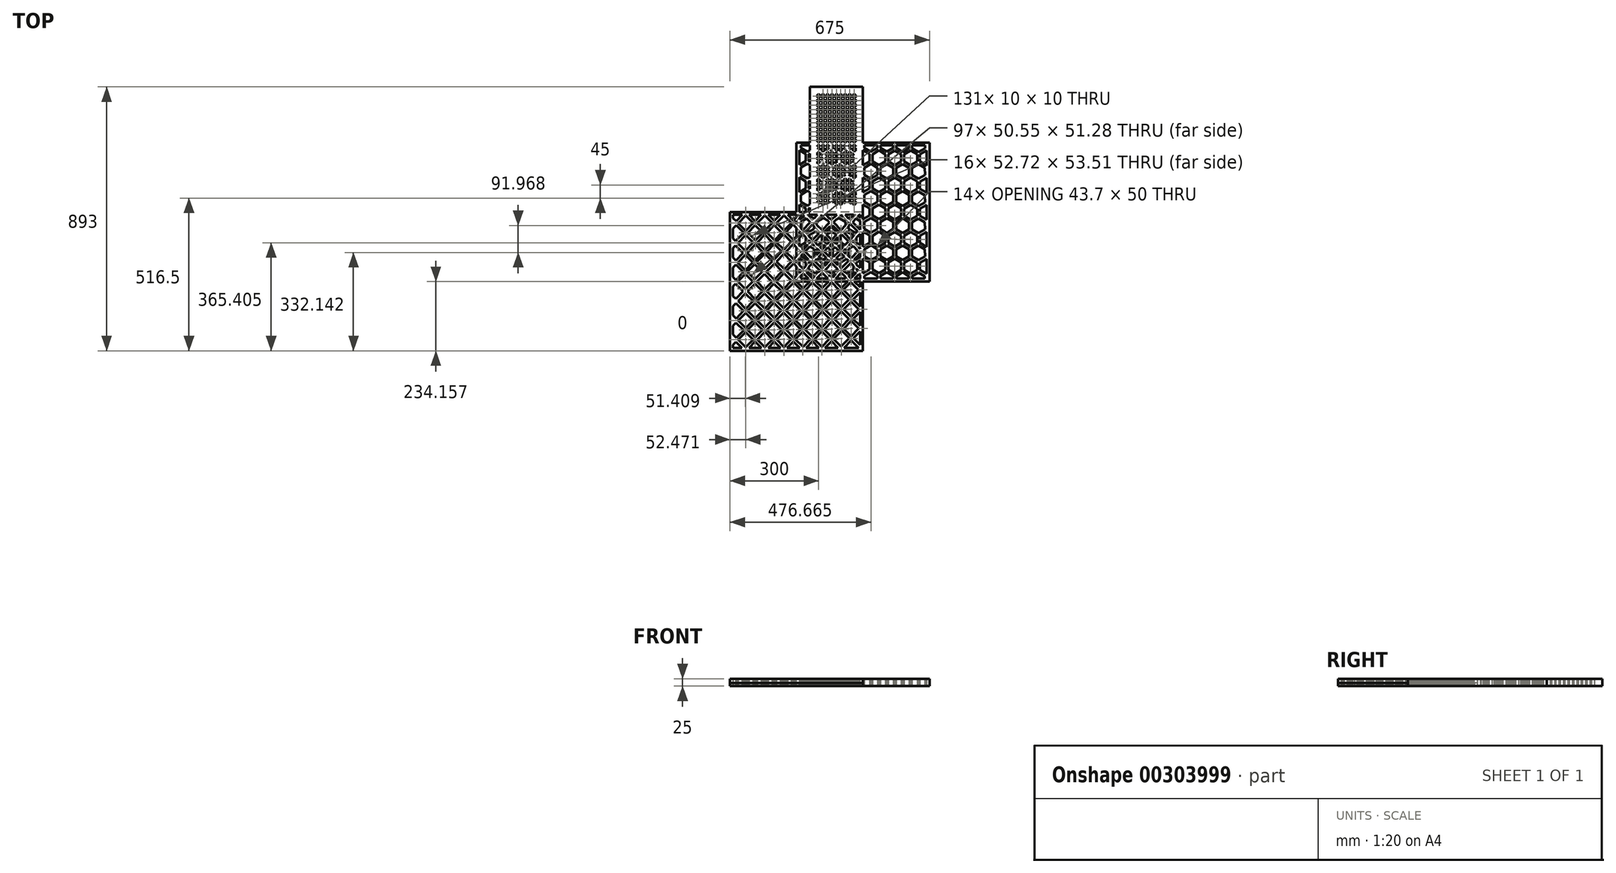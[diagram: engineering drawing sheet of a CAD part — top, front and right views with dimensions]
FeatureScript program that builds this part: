
annotation { "Feature Type Name" : "Feature", "Feature Type Description" : "" }
export const myFeature = defineFeature(function(context is Context, id is Id, definition is map)
    precondition{}
    {
        {
            var Q0;
            Q0=qCreatedBy(makeId("Top.planeOp"),FACE);
            var sketch = newSketch(context, id + "F0", { "sketchPlane" : qUnion([Q0])});
            skLineSegment(sketch, "E0.bottom", {"start": v(-180, 423) * mm, "end": v(0, 423) * mm});
            skLineSegment(sketch, "E0.top", {"start": v(-180, 0) * mm, "end": v(0, 0) * mm});
            skLineSegment(sketch, "E0.left", {"start": v(-180, 423) * mm, "end": v(-180, 0) * mm});
            skLineSegment(sketch, "E0.right", {"start": v(0, 423) * mm, "end": v(0, 0) * mm});
            skLineSegment(sketch, "E1", {"start": v(-153.5, 396.5) * mm, "end": v(-146.5, 396.5) * mm});
            skLineSegment(sketch, "E2", {"start": v(-155, 386.5) * mm, "end": v(-145, 386.5) * mm});
            skLineSegment(sketch, "E3", {"start": v(-145, 386.5) * mm, "end": v(-145, 395) * mm});
            skLineSegment(sketch, "E4.trimOffspring", {"start": v(-155, 386.5) * mm, "end": v(-155, 395) * mm});
            skLineSegment(sketch, "E5.0.1.0", {"start": v(-155, 371.5) * mm, "end": v(-155, 381.5) * mm});
            skLineSegment(sketch, "E5.0.1.1", {"start": v(-145, 371.5) * mm, "end": v(-145, 381.5) * mm});
            skLineSegment(sketch, "E5.0.1.2", {"start": v(-155, 371.5) * mm, "end": v(-145, 371.5) * mm});
            skLineSegment(sketch, "E5.0.1.3", {"start": v(-155, 381.5) * mm, "end": v(-145, 381.5) * mm});
            skLineSegment(sketch, "E5.0.2.0", {"start": v(-155, 356.5) * mm, "end": v(-155, 366.5) * mm});
            skLineSegment(sketch, "E5.0.2.1", {"start": v(-145, 356.5) * mm, "end": v(-145, 366.5) * mm});
            skLineSegment(sketch, "E5.0.2.2", {"start": v(-155, 356.5) * mm, "end": v(-145, 356.5) * mm});
            skLineSegment(sketch, "E5.0.2.3", {"start": v(-155, 366.5) * mm, "end": v(-145, 366.5) * mm});
            skLineSegment(sketch, "E5.0.3.0", {"start": v(-155, 341.5) * mm, "end": v(-155, 351.5) * mm});
            skLineSegment(sketch, "E5.0.3.1", {"start": v(-145, 341.5) * mm, "end": v(-145, 351.5) * mm});
            skLineSegment(sketch, "E5.0.3.2", {"start": v(-155, 341.5) * mm, "end": v(-145, 341.5) * mm});
            skLineSegment(sketch, "E5.0.3.3", {"start": v(-155, 351.5) * mm, "end": v(-145, 351.5) * mm});
            skLineSegment(sketch, "E5.0.4.0", {"start": v(-155, 326.5) * mm, "end": v(-155, 336.5) * mm});
            skLineSegment(sketch, "E5.0.4.1", {"start": v(-145, 326.5) * mm, "end": v(-145, 336.5) * mm});
            skLineSegment(sketch, "E5.0.4.2", {"start": v(-155, 326.5) * mm, "end": v(-145, 326.5) * mm});
            skLineSegment(sketch, "E5.0.4.3", {"start": v(-155, 336.5) * mm, "end": v(-145, 336.5) * mm});
            skLineSegment(sketch, "E5.0.5.0", {"start": v(-155, 311.5) * mm, "end": v(-155, 321.5) * mm});
            skLineSegment(sketch, "E5.0.5.1", {"start": v(-145, 311.5) * mm, "end": v(-145, 321.5) * mm});
            skLineSegment(sketch, "E5.0.5.2", {"start": v(-155, 311.5) * mm, "end": v(-145, 311.5) * mm});
            skLineSegment(sketch, "E5.0.5.3", {"start": v(-155, 321.5) * mm, "end": v(-145, 321.5) * mm});
            skLineSegment(sketch, "E5.0.6.0", {"start": v(-155, 296.5) * mm, "end": v(-155, 306.5) * mm});
            skLineSegment(sketch, "E5.0.6.1", {"start": v(-145, 296.5) * mm, "end": v(-145, 306.5) * mm});
            skLineSegment(sketch, "E5.0.6.2", {"start": v(-155, 296.5) * mm, "end": v(-145, 296.5) * mm});
            skLineSegment(sketch, "E5.0.6.3", {"start": v(-155, 306.5) * mm, "end": v(-145, 306.5) * mm});
            skLineSegment(sketch, "E5.0.7.0", {"start": v(-155, 281.5) * mm, "end": v(-155, 291.5) * mm});
            skLineSegment(sketch, "E5.0.7.1", {"start": v(-145, 281.5) * mm, "end": v(-145, 291.5) * mm});
            skLineSegment(sketch, "E5.0.7.2", {"start": v(-155, 281.5) * mm, "end": v(-145, 281.5) * mm});
            skLineSegment(sketch, "E5.0.7.3", {"start": v(-155, 291.5) * mm, "end": v(-145, 291.5) * mm});
            skLineSegment(sketch, "E5.0.8.0", {"start": v(-155, 266.5) * mm, "end": v(-155, 276.5) * mm});
            skLineSegment(sketch, "E5.0.8.1", {"start": v(-145, 266.5) * mm, "end": v(-145, 276.5) * mm});
            skLineSegment(sketch, "E5.0.8.2", {"start": v(-155, 266.5) * mm, "end": v(-145, 266.5) * mm});
            skLineSegment(sketch, "E5.0.8.3", {"start": v(-155, 276.5) * mm, "end": v(-145, 276.5) * mm});
            skLineSegment(sketch, "E5.0.9.0", {"start": v(-155, 251.5) * mm, "end": v(-155, 261.5) * mm});
            skLineSegment(sketch, "E5.0.9.1", {"start": v(-145, 251.5) * mm, "end": v(-145, 261.5) * mm});
            skLineSegment(sketch, "E5.0.9.2", {"start": v(-155, 251.5) * mm, "end": v(-145, 251.5) * mm});
            skLineSegment(sketch, "E5.0.9.3", {"start": v(-155, 261.5) * mm, "end": v(-145, 261.5) * mm});
            skLineSegment(sketch, "E5.0.10.0", {"start": v(-155, 236.5) * mm, "end": v(-155, 246.5) * mm});
            skLineSegment(sketch, "E5.0.10.1", {"start": v(-145, 236.5) * mm, "end": v(-145, 246.5) * mm});
            skLineSegment(sketch, "E5.0.10.2", {"start": v(-155, 236.5) * mm, "end": v(-145, 236.5) * mm});
            skLineSegment(sketch, "E5.0.10.3", {"start": v(-155, 246.5) * mm, "end": v(-145, 246.5) * mm});
            skLineSegment(sketch, "E5.0.11.0", {"start": v(-155, 221.5) * mm, "end": v(-155, 231.5) * mm});
            skLineSegment(sketch, "E5.0.11.1", {"start": v(-145, 221.5) * mm, "end": v(-145, 231.5) * mm});
            skLineSegment(sketch, "E5.0.11.2", {"start": v(-155, 221.5) * mm, "end": v(-145, 221.5) * mm});
            skLineSegment(sketch, "E5.0.11.3", {"start": v(-155, 231.5) * mm, "end": v(-145, 231.5) * mm});
            skLineSegment(sketch, "E5.0.12.0", {"start": v(-155, 206.5) * mm, "end": v(-155, 216.5) * mm});
            skLineSegment(sketch, "E5.0.12.1", {"start": v(-145, 206.5) * mm, "end": v(-145, 216.5) * mm});
            skLineSegment(sketch, "E5.0.12.2", {"start": v(-155, 206.5) * mm, "end": v(-145, 206.5) * mm});
            skLineSegment(sketch, "E5.0.12.3", {"start": v(-155, 216.5) * mm, "end": v(-145, 216.5) * mm});
            skLineSegment(sketch, "E5.0.13.0", {"start": v(-155, 191.5) * mm, "end": v(-155, 201.5) * mm});
            skLineSegment(sketch, "E5.0.13.1", {"start": v(-145, 191.5) * mm, "end": v(-145, 201.5) * mm});
            skLineSegment(sketch, "E5.0.13.2", {"start": v(-155, 191.5) * mm, "end": v(-145, 191.5) * mm});
            skLineSegment(sketch, "E5.0.13.3", {"start": v(-155, 201.5) * mm, "end": v(-145, 201.5) * mm});
            skLineSegment(sketch, "E5.0.14.0", {"start": v(-155, 176.5) * mm, "end": v(-155, 186.5) * mm});
            skLineSegment(sketch, "E5.0.14.1", {"start": v(-145, 176.5) * mm, "end": v(-145, 186.5) * mm});
            skLineSegment(sketch, "E5.0.14.2", {"start": v(-155, 176.5) * mm, "end": v(-145, 176.5) * mm});
            skLineSegment(sketch, "E5.0.14.3", {"start": v(-155, 186.5) * mm, "end": v(-145, 186.5) * mm});
            skLineSegment(sketch, "E5.0.15.0", {"start": v(-155, 161.5) * mm, "end": v(-155, 171.5) * mm});
            skLineSegment(sketch, "E5.0.15.1", {"start": v(-145, 161.5) * mm, "end": v(-145, 171.5) * mm});
            skLineSegment(sketch, "E5.0.15.2", {"start": v(-155, 161.5) * mm, "end": v(-145, 161.5) * mm});
            skLineSegment(sketch, "E5.0.15.3", {"start": v(-155, 171.5) * mm, "end": v(-145, 171.5) * mm});
            skLineSegment(sketch, "E5.0.16.0", {"start": v(-155, 146.5) * mm, "end": v(-155, 156.5) * mm});
            skLineSegment(sketch, "E5.0.16.1", {"start": v(-145, 146.5) * mm, "end": v(-145, 156.5) * mm});
            skLineSegment(sketch, "E5.0.16.2", {"start": v(-155, 146.5) * mm, "end": v(-145, 146.5) * mm});
            skLineSegment(sketch, "E5.0.16.3", {"start": v(-155, 156.5) * mm, "end": v(-145, 156.5) * mm});
            skLineSegment(sketch, "E5.0.17.0", {"start": v(-155, 131.5) * mm, "end": v(-155, 141.5) * mm});
            skLineSegment(sketch, "E5.0.17.1", {"start": v(-145, 131.5) * mm, "end": v(-145, 141.5) * mm});
            skLineSegment(sketch, "E5.0.17.2", {"start": v(-155, 131.5) * mm, "end": v(-145, 131.5) * mm});
            skLineSegment(sketch, "E5.0.17.3", {"start": v(-155, 141.5) * mm, "end": v(-145, 141.5) * mm});
            skLineSegment(sketch, "E5.0.18.0", {"start": v(-155, 116.5) * mm, "end": v(-155, 126.5) * mm});
            skLineSegment(sketch, "E5.0.18.1", {"start": v(-145, 116.5) * mm, "end": v(-145, 126.5) * mm});
            skLineSegment(sketch, "E5.0.18.2", {"start": v(-155, 116.5) * mm, "end": v(-145, 116.5) * mm});
            skLineSegment(sketch, "E5.0.18.3", {"start": v(-155, 126.5) * mm, "end": v(-145, 126.5) * mm});
            skLineSegment(sketch, "E5.0.19.0", {"start": v(-155, 101.5) * mm, "end": v(-155, 111.5) * mm});
            skLineSegment(sketch, "E5.0.19.1", {"start": v(-145, 101.5) * mm, "end": v(-145, 111.5) * mm});
            skLineSegment(sketch, "E5.0.19.2", {"start": v(-155, 101.5) * mm, "end": v(-145, 101.5) * mm});
            skLineSegment(sketch, "E5.0.19.3", {"start": v(-155, 111.5) * mm, "end": v(-145, 111.5) * mm});
            skLineSegment(sketch, "E5.0.20.0", {"start": v(-155, 86.5) * mm, "end": v(-155, 96.5) * mm});
            skLineSegment(sketch, "E5.0.20.1", {"start": v(-145, 86.5) * mm, "end": v(-145, 96.5) * mm});
            skLineSegment(sketch, "E5.0.20.2", {"start": v(-155, 86.5) * mm, "end": v(-145, 86.5) * mm});
            skLineSegment(sketch, "E5.0.20.3", {"start": v(-155, 96.5) * mm, "end": v(-145, 96.5) * mm});
            skLineSegment(sketch, "E5.0.21.0", {"start": v(-155, 71.5) * mm, "end": v(-155, 81.5) * mm});
            skLineSegment(sketch, "E5.0.21.1", {"start": v(-145, 71.5) * mm, "end": v(-145, 81.5) * mm});
            skLineSegment(sketch, "E5.0.21.2", {"start": v(-155, 71.5) * mm, "end": v(-145, 71.5) * mm});
            skLineSegment(sketch, "E5.0.21.3", {"start": v(-155, 81.5) * mm, "end": v(-145, 81.5) * mm});
            skLineSegment(sketch, "E5.0.22.0", {"start": v(-155, 56.5) * mm, "end": v(-155, 66.5) * mm});
            skLineSegment(sketch, "E5.0.22.1", {"start": v(-145, 56.5) * mm, "end": v(-145, 66.5) * mm});
            skLineSegment(sketch, "E5.0.22.2", {"start": v(-155, 56.5) * mm, "end": v(-145, 56.5) * mm});
            skLineSegment(sketch, "E5.0.22.3", {"start": v(-155, 66.5) * mm, "end": v(-145, 66.5) * mm});
            skLineSegment(sketch, "E5.0.23.0", {"start": v(-155, 41.5) * mm, "end": v(-155, 51.5) * mm});
            skLineSegment(sketch, "E5.0.23.1", {"start": v(-145, 41.5) * mm, "end": v(-145, 51.5) * mm});
            skLineSegment(sketch, "E5.0.23.2", {"start": v(-155, 41.5) * mm, "end": v(-145, 41.5) * mm});
            skLineSegment(sketch, "E5.0.23.3", {"start": v(-155, 51.5) * mm, "end": v(-145, 51.5) * mm});
            skLineSegment(sketch, "E5.0.24.0", {"start": v(-155, 26.5) * mm, "end": v(-155, 36.5) * mm});
            skLineSegment(sketch, "E5.0.24.1", {"start": v(-145, 26.5) * mm, "end": v(-145, 36.5) * mm});
            skLineSegment(sketch, "E5.0.24.2", {"start": v(-155, 26.5) * mm, "end": v(-145, 26.5) * mm});
            skLineSegment(sketch, "E5.0.24.3", {"start": v(-155, 36.5) * mm, "end": v(-145, 36.5) * mm});
            skLineSegment(sketch, "E5.1.0.0", {"start": v(-140, 386.5) * mm, "end": v(-140, 396.5) * mm});
            skLineSegment(sketch, "E5.1.0.1", {"start": v(-130, 386.5) * mm, "end": v(-130, 396.5) * mm});
            skLineSegment(sketch, "E5.1.0.2", {"start": v(-140, 386.5) * mm, "end": v(-130, 386.5) * mm});
            skLineSegment(sketch, "E5.1.0.3", {"start": v(-140, 396.5) * mm, "end": v(-130, 396.5) * mm});
            skLineSegment(sketch, "E5.1.1.0", {"start": v(-140, 371.5) * mm, "end": v(-140, 381.5) * mm});
            skLineSegment(sketch, "E5.1.1.1", {"start": v(-130, 371.5) * mm, "end": v(-130, 381.5) * mm});
            skLineSegment(sketch, "E5.1.1.2", {"start": v(-140, 371.5) * mm, "end": v(-130, 371.5) * mm});
            skLineSegment(sketch, "E5.1.1.3", {"start": v(-140, 381.5) * mm, "end": v(-130, 381.5) * mm});
            skLineSegment(sketch, "E5.1.2.0", {"start": v(-140, 356.5) * mm, "end": v(-140, 366.5) * mm});
            skLineSegment(sketch, "E5.1.2.1", {"start": v(-130, 356.5) * mm, "end": v(-130, 366.5) * mm});
            skLineSegment(sketch, "E5.1.2.2", {"start": v(-140, 356.5) * mm, "end": v(-130, 356.5) * mm});
            skLineSegment(sketch, "E5.1.2.3", {"start": v(-140, 366.5) * mm, "end": v(-130, 366.5) * mm});
            skLineSegment(sketch, "E5.1.3.0", {"start": v(-140, 341.5) * mm, "end": v(-140, 351.5) * mm});
            skLineSegment(sketch, "E5.1.3.1", {"start": v(-130, 341.5) * mm, "end": v(-130, 351.5) * mm});
            skLineSegment(sketch, "E5.1.3.2", {"start": v(-140, 341.5) * mm, "end": v(-130, 341.5) * mm});
            skLineSegment(sketch, "E5.1.3.3", {"start": v(-140, 351.5) * mm, "end": v(-130, 351.5) * mm});
            skLineSegment(sketch, "E5.1.4.0", {"start": v(-140, 326.5) * mm, "end": v(-140, 336.5) * mm});
            skLineSegment(sketch, "E5.1.4.1", {"start": v(-130, 326.5) * mm, "end": v(-130, 336.5) * mm});
            skLineSegment(sketch, "E5.1.4.2", {"start": v(-140, 326.5) * mm, "end": v(-130, 326.5) * mm});
            skLineSegment(sketch, "E5.1.4.3", {"start": v(-140, 336.5) * mm, "end": v(-130, 336.5) * mm});
            skLineSegment(sketch, "E5.1.5.0", {"start": v(-140, 311.5) * mm, "end": v(-140, 321.5) * mm});
            skLineSegment(sketch, "E5.1.5.1", {"start": v(-130, 311.5) * mm, "end": v(-130, 321.5) * mm});
            skLineSegment(sketch, "E5.1.5.2", {"start": v(-140, 311.5) * mm, "end": v(-130, 311.5) * mm});
            skLineSegment(sketch, "E5.1.5.3", {"start": v(-140, 321.5) * mm, "end": v(-130, 321.5) * mm});
            skLineSegment(sketch, "E5.1.6.0", {"start": v(-140, 296.5) * mm, "end": v(-140, 306.5) * mm});
            skLineSegment(sketch, "E5.1.6.1", {"start": v(-130, 296.5) * mm, "end": v(-130, 306.5) * mm});
            skLineSegment(sketch, "E5.1.6.2", {"start": v(-140, 296.5) * mm, "end": v(-130, 296.5) * mm});
            skLineSegment(sketch, "E5.1.6.3", {"start": v(-140, 306.5) * mm, "end": v(-130, 306.5) * mm});
            skLineSegment(sketch, "E5.1.7.0", {"start": v(-140, 281.5) * mm, "end": v(-140, 291.5) * mm});
            skLineSegment(sketch, "E5.1.7.1", {"start": v(-130, 281.5) * mm, "end": v(-130, 291.5) * mm});
            skLineSegment(sketch, "E5.1.7.2", {"start": v(-140, 281.5) * mm, "end": v(-130, 281.5) * mm});
            skLineSegment(sketch, "E5.1.7.3", {"start": v(-140, 291.5) * mm, "end": v(-130, 291.5) * mm});
            skLineSegment(sketch, "E5.1.8.0", {"start": v(-140, 266.5) * mm, "end": v(-140, 276.5) * mm});
            skLineSegment(sketch, "E5.1.8.1", {"start": v(-130, 266.5) * mm, "end": v(-130, 276.5) * mm});
            skLineSegment(sketch, "E5.1.8.2", {"start": v(-140, 266.5) * mm, "end": v(-130, 266.5) * mm});
            skLineSegment(sketch, "E5.1.8.3", {"start": v(-140, 276.5) * mm, "end": v(-130, 276.5) * mm});
            skLineSegment(sketch, "E5.1.9.0", {"start": v(-140, 251.5) * mm, "end": v(-140, 261.5) * mm});
            skLineSegment(sketch, "E5.1.9.1", {"start": v(-130, 251.5) * mm, "end": v(-130, 261.5) * mm});
            skLineSegment(sketch, "E5.1.9.2", {"start": v(-140, 251.5) * mm, "end": v(-130, 251.5) * mm});
            skLineSegment(sketch, "E5.1.9.3", {"start": v(-140, 261.5) * mm, "end": v(-130, 261.5) * mm});
            skLineSegment(sketch, "E5.1.10.0", {"start": v(-140, 236.5) * mm, "end": v(-140, 246.5) * mm});
            skLineSegment(sketch, "E5.1.10.1", {"start": v(-130, 236.5) * mm, "end": v(-130, 246.5) * mm});
            skLineSegment(sketch, "E5.1.10.2", {"start": v(-140, 236.5) * mm, "end": v(-130, 236.5) * mm});
            skLineSegment(sketch, "E5.1.10.3", {"start": v(-140, 246.5) * mm, "end": v(-130, 246.5) * mm});
            skLineSegment(sketch, "E5.1.11.0", {"start": v(-140, 221.5) * mm, "end": v(-140, 231.5) * mm});
            skLineSegment(sketch, "E5.1.11.1", {"start": v(-130, 221.5) * mm, "end": v(-130, 231.5) * mm});
            skLineSegment(sketch, "E5.1.11.2", {"start": v(-140, 221.5) * mm, "end": v(-130, 221.5) * mm});
            skLineSegment(sketch, "E5.1.11.3", {"start": v(-140, 231.5) * mm, "end": v(-130, 231.5) * mm});
            skLineSegment(sketch, "E5.1.12.0", {"start": v(-140, 206.5) * mm, "end": v(-140, 216.5) * mm});
            skLineSegment(sketch, "E5.1.12.1", {"start": v(-130, 206.5) * mm, "end": v(-130, 216.5) * mm});
            skLineSegment(sketch, "E5.1.12.2", {"start": v(-140, 206.5) * mm, "end": v(-130, 206.5) * mm});
            skLineSegment(sketch, "E5.1.12.3", {"start": v(-140, 216.5) * mm, "end": v(-130, 216.5) * mm});
            skLineSegment(sketch, "E5.1.13.0", {"start": v(-140, 191.5) * mm, "end": v(-140, 201.5) * mm});
            skLineSegment(sketch, "E5.1.13.1", {"start": v(-130, 191.5) * mm, "end": v(-130, 201.5) * mm});
            skLineSegment(sketch, "E5.1.13.2", {"start": v(-140, 191.5) * mm, "end": v(-130, 191.5) * mm});
            skLineSegment(sketch, "E5.1.13.3", {"start": v(-140, 201.5) * mm, "end": v(-130, 201.5) * mm});
            skLineSegment(sketch, "E5.1.14.0", {"start": v(-140, 176.5) * mm, "end": v(-140, 186.5) * mm});
            skLineSegment(sketch, "E5.1.14.1", {"start": v(-130, 176.5) * mm, "end": v(-130, 186.5) * mm});
            skLineSegment(sketch, "E5.1.14.2", {"start": v(-140, 176.5) * mm, "end": v(-130, 176.5) * mm});
            skLineSegment(sketch, "E5.1.14.3", {"start": v(-140, 186.5) * mm, "end": v(-130, 186.5) * mm});
            skLineSegment(sketch, "E5.1.15.0", {"start": v(-140, 161.5) * mm, "end": v(-140, 171.5) * mm});
            skLineSegment(sketch, "E5.1.15.1", {"start": v(-130, 161.5) * mm, "end": v(-130, 171.5) * mm});
            skLineSegment(sketch, "E5.1.15.2", {"start": v(-140, 161.5) * mm, "end": v(-130, 161.5) * mm});
            skLineSegment(sketch, "E5.1.15.3", {"start": v(-140, 171.5) * mm, "end": v(-130, 171.5) * mm});
            skLineSegment(sketch, "E5.1.16.0", {"start": v(-140, 146.5) * mm, "end": v(-140, 156.5) * mm});
            skLineSegment(sketch, "E5.1.16.1", {"start": v(-130, 146.5) * mm, "end": v(-130, 156.5) * mm});
            skLineSegment(sketch, "E5.1.16.2", {"start": v(-140, 146.5) * mm, "end": v(-130, 146.5) * mm});
            skLineSegment(sketch, "E5.1.16.3", {"start": v(-140, 156.5) * mm, "end": v(-130, 156.5) * mm});
            skLineSegment(sketch, "E5.1.17.0", {"start": v(-140, 131.5) * mm, "end": v(-140, 141.5) * mm});
            skLineSegment(sketch, "E5.1.17.1", {"start": v(-130, 131.5) * mm, "end": v(-130, 141.5) * mm});
            skLineSegment(sketch, "E5.1.17.2", {"start": v(-140, 131.5) * mm, "end": v(-130, 131.5) * mm});
            skLineSegment(sketch, "E5.1.17.3", {"start": v(-140, 141.5) * mm, "end": v(-130, 141.5) * mm});
            skLineSegment(sketch, "E5.1.18.0", {"start": v(-140, 116.5) * mm, "end": v(-140, 126.5) * mm});
            skLineSegment(sketch, "E5.1.18.1", {"start": v(-130, 116.5) * mm, "end": v(-130, 126.5) * mm});
            skLineSegment(sketch, "E5.1.18.2", {"start": v(-140, 116.5) * mm, "end": v(-130, 116.5) * mm});
            skLineSegment(sketch, "E5.1.18.3", {"start": v(-140, 126.5) * mm, "end": v(-130, 126.5) * mm});
            skLineSegment(sketch, "E5.1.19.0", {"start": v(-140, 101.5) * mm, "end": v(-140, 111.5) * mm});
            skLineSegment(sketch, "E5.1.19.1", {"start": v(-130, 101.5) * mm, "end": v(-130, 111.5) * mm});
            skLineSegment(sketch, "E5.1.19.2", {"start": v(-140, 101.5) * mm, "end": v(-130, 101.5) * mm});
            skLineSegment(sketch, "E5.1.19.3", {"start": v(-140, 111.5) * mm, "end": v(-130, 111.5) * mm});
            skLineSegment(sketch, "E5.1.20.0", {"start": v(-140, 86.5) * mm, "end": v(-140, 96.5) * mm});
            skLineSegment(sketch, "E5.1.20.1", {"start": v(-130, 86.5) * mm, "end": v(-130, 96.5) * mm});
            skLineSegment(sketch, "E5.1.20.2", {"start": v(-140, 86.5) * mm, "end": v(-130, 86.5) * mm});
            skLineSegment(sketch, "E5.1.20.3", {"start": v(-140, 96.5) * mm, "end": v(-130, 96.5) * mm});
            skLineSegment(sketch, "E5.1.21.0", {"start": v(-140, 71.5) * mm, "end": v(-140, 81.5) * mm});
            skLineSegment(sketch, "E5.1.21.1", {"start": v(-130, 71.5) * mm, "end": v(-130, 81.5) * mm});
            skLineSegment(sketch, "E5.1.21.2", {"start": v(-140, 71.5) * mm, "end": v(-130, 71.5) * mm});
            skLineSegment(sketch, "E5.1.21.3", {"start": v(-140, 81.5) * mm, "end": v(-130, 81.5) * mm});
            skLineSegment(sketch, "E5.1.22.0", {"start": v(-140, 56.5) * mm, "end": v(-140, 66.5) * mm});
            skLineSegment(sketch, "E5.1.22.1", {"start": v(-130, 56.5) * mm, "end": v(-130, 66.5) * mm});
            skLineSegment(sketch, "E5.1.22.2", {"start": v(-140, 56.5) * mm, "end": v(-130, 56.5) * mm});
            skLineSegment(sketch, "E5.1.22.3", {"start": v(-140, 66.5) * mm, "end": v(-130, 66.5) * mm});
            skLineSegment(sketch, "E5.1.23.0", {"start": v(-140, 41.5) * mm, "end": v(-140, 51.5) * mm});
            skLineSegment(sketch, "E5.1.23.1", {"start": v(-130, 41.5) * mm, "end": v(-130, 51.5) * mm});
            skLineSegment(sketch, "E5.1.23.2", {"start": v(-140, 41.5) * mm, "end": v(-130, 41.5) * mm});
            skLineSegment(sketch, "E5.1.23.3", {"start": v(-140, 51.5) * mm, "end": v(-130, 51.5) * mm});
            skLineSegment(sketch, "E5.1.24.0", {"start": v(-140, 26.5) * mm, "end": v(-140, 36.5) * mm});
            skLineSegment(sketch, "E5.1.24.1", {"start": v(-130, 26.5) * mm, "end": v(-130, 36.5) * mm});
            skLineSegment(sketch, "E5.1.24.2", {"start": v(-140, 26.5) * mm, "end": v(-130, 26.5) * mm});
            skLineSegment(sketch, "E5.1.24.3", {"start": v(-140, 36.5) * mm, "end": v(-130, 36.5) * mm});
            skLineSegment(sketch, "E5.2.0.0", {"start": v(-125, 386.5) * mm, "end": v(-125, 396.5) * mm});
            skLineSegment(sketch, "E5.2.0.1", {"start": v(-115, 386.5) * mm, "end": v(-115, 396.5) * mm});
            skLineSegment(sketch, "E5.2.0.2", {"start": v(-125, 386.5) * mm, "end": v(-115, 386.5) * mm});
            skLineSegment(sketch, "E5.2.0.3", {"start": v(-125, 396.5) * mm, "end": v(-115, 396.5) * mm});
            skLineSegment(sketch, "E5.2.1.0", {"start": v(-125, 371.5) * mm, "end": v(-125, 381.5) * mm});
            skLineSegment(sketch, "E5.2.1.1", {"start": v(-115, 371.5) * mm, "end": v(-115, 381.5) * mm});
            skLineSegment(sketch, "E5.2.1.2", {"start": v(-125, 371.5) * mm, "end": v(-115, 371.5) * mm});
            skLineSegment(sketch, "E5.2.1.3", {"start": v(-125, 381.5) * mm, "end": v(-115, 381.5) * mm});
            skLineSegment(sketch, "E5.2.2.0", {"start": v(-125, 356.5) * mm, "end": v(-125, 366.5) * mm});
            skLineSegment(sketch, "E5.2.2.1", {"start": v(-115, 356.5) * mm, "end": v(-115, 366.5) * mm});
            skLineSegment(sketch, "E5.2.2.2", {"start": v(-125, 356.5) * mm, "end": v(-115, 356.5) * mm});
            skLineSegment(sketch, "E5.2.2.3", {"start": v(-125, 366.5) * mm, "end": v(-115, 366.5) * mm});
            skLineSegment(sketch, "E5.2.3.0", {"start": v(-125, 341.5) * mm, "end": v(-125, 351.5) * mm});
            skLineSegment(sketch, "E5.2.3.1", {"start": v(-115, 341.5) * mm, "end": v(-115, 351.5) * mm});
            skLineSegment(sketch, "E5.2.3.2", {"start": v(-125, 341.5) * mm, "end": v(-115, 341.5) * mm});
            skLineSegment(sketch, "E5.2.3.3", {"start": v(-125, 351.5) * mm, "end": v(-115, 351.5) * mm});
            skLineSegment(sketch, "E5.2.4.0", {"start": v(-125, 326.5) * mm, "end": v(-125, 336.5) * mm});
            skLineSegment(sketch, "E5.2.4.1", {"start": v(-115, 326.5) * mm, "end": v(-115, 336.5) * mm});
            skLineSegment(sketch, "E5.2.4.2", {"start": v(-125, 326.5) * mm, "end": v(-115, 326.5) * mm});
            skLineSegment(sketch, "E5.2.4.3", {"start": v(-125, 336.5) * mm, "end": v(-115, 336.5) * mm});
            skLineSegment(sketch, "E5.2.5.0", {"start": v(-125, 311.5) * mm, "end": v(-125, 321.5) * mm});
            skLineSegment(sketch, "E5.2.5.1", {"start": v(-115, 311.5) * mm, "end": v(-115, 321.5) * mm});
            skLineSegment(sketch, "E5.2.5.2", {"start": v(-125, 311.5) * mm, "end": v(-115, 311.5) * mm});
            skLineSegment(sketch, "E5.2.5.3", {"start": v(-125, 321.5) * mm, "end": v(-115, 321.5) * mm});
            skLineSegment(sketch, "E5.2.6.0", {"start": v(-125, 296.5) * mm, "end": v(-125, 306.5) * mm});
            skLineSegment(sketch, "E5.2.6.1", {"start": v(-115, 296.5) * mm, "end": v(-115, 306.5) * mm});
            skLineSegment(sketch, "E5.2.6.2", {"start": v(-125, 296.5) * mm, "end": v(-115, 296.5) * mm});
            skLineSegment(sketch, "E5.2.6.3", {"start": v(-125, 306.5) * mm, "end": v(-115, 306.5) * mm});
            skLineSegment(sketch, "E5.2.7.0", {"start": v(-125, 281.5) * mm, "end": v(-125, 291.5) * mm});
            skLineSegment(sketch, "E5.2.7.1", {"start": v(-115, 281.5) * mm, "end": v(-115, 291.5) * mm});
            skLineSegment(sketch, "E5.2.7.2", {"start": v(-125, 281.5) * mm, "end": v(-115, 281.5) * mm});
            skLineSegment(sketch, "E5.2.7.3", {"start": v(-125, 291.5) * mm, "end": v(-115, 291.5) * mm});
            skLineSegment(sketch, "E5.2.8.0", {"start": v(-125, 266.5) * mm, "end": v(-125, 276.5) * mm});
            skLineSegment(sketch, "E5.2.8.1", {"start": v(-115, 266.5) * mm, "end": v(-115, 276.5) * mm});
            skLineSegment(sketch, "E5.2.8.2", {"start": v(-125, 266.5) * mm, "end": v(-115, 266.5) * mm});
            skLineSegment(sketch, "E5.2.8.3", {"start": v(-125, 276.5) * mm, "end": v(-115, 276.5) * mm});
            skLineSegment(sketch, "E5.2.9.0", {"start": v(-125, 251.5) * mm, "end": v(-125, 261.5) * mm});
            skLineSegment(sketch, "E5.2.9.1", {"start": v(-115, 251.5) * mm, "end": v(-115, 261.5) * mm});
            skLineSegment(sketch, "E5.2.9.2", {"start": v(-125, 251.5) * mm, "end": v(-115, 251.5) * mm});
            skLineSegment(sketch, "E5.2.9.3", {"start": v(-125, 261.5) * mm, "end": v(-115, 261.5) * mm});
            skLineSegment(sketch, "E5.2.10.0", {"start": v(-125, 236.5) * mm, "end": v(-125, 246.5) * mm});
            skLineSegment(sketch, "E5.2.10.1", {"start": v(-115, 236.5) * mm, "end": v(-115, 246.5) * mm});
            skLineSegment(sketch, "E5.2.10.2", {"start": v(-125, 236.5) * mm, "end": v(-115, 236.5) * mm});
            skLineSegment(sketch, "E5.2.10.3", {"start": v(-125, 246.5) * mm, "end": v(-115, 246.5) * mm});
            skLineSegment(sketch, "E5.2.11.0", {"start": v(-125, 221.5) * mm, "end": v(-125, 231.5) * mm});
            skLineSegment(sketch, "E5.2.11.1", {"start": v(-115, 221.5) * mm, "end": v(-115, 231.5) * mm});
            skLineSegment(sketch, "E5.2.11.2", {"start": v(-125, 221.5) * mm, "end": v(-115, 221.5) * mm});
            skLineSegment(sketch, "E5.2.11.3", {"start": v(-125, 231.5) * mm, "end": v(-115, 231.5) * mm});
            skLineSegment(sketch, "E5.2.12.0", {"start": v(-125, 206.5) * mm, "end": v(-125, 216.5) * mm});
            skLineSegment(sketch, "E5.2.12.1", {"start": v(-115, 206.5) * mm, "end": v(-115, 216.5) * mm});
            skLineSegment(sketch, "E5.2.12.2", {"start": v(-125, 206.5) * mm, "end": v(-115, 206.5) * mm});
            skLineSegment(sketch, "E5.2.12.3", {"start": v(-125, 216.5) * mm, "end": v(-115, 216.5) * mm});
            skLineSegment(sketch, "E5.2.13.0", {"start": v(-125, 191.5) * mm, "end": v(-125, 201.5) * mm});
            skLineSegment(sketch, "E5.2.13.1", {"start": v(-115, 191.5) * mm, "end": v(-115, 201.5) * mm});
            skLineSegment(sketch, "E5.2.13.2", {"start": v(-125, 191.5) * mm, "end": v(-115, 191.5) * mm});
            skLineSegment(sketch, "E5.2.13.3", {"start": v(-125, 201.5) * mm, "end": v(-115, 201.5) * mm});
            skLineSegment(sketch, "E5.2.14.0", {"start": v(-125, 176.5) * mm, "end": v(-125, 186.5) * mm});
            skLineSegment(sketch, "E5.2.14.1", {"start": v(-115, 176.5) * mm, "end": v(-115, 186.5) * mm});
            skLineSegment(sketch, "E5.2.14.2", {"start": v(-125, 176.5) * mm, "end": v(-115, 176.5) * mm});
            skLineSegment(sketch, "E5.2.14.3", {"start": v(-125, 186.5) * mm, "end": v(-115, 186.5) * mm});
            skLineSegment(sketch, "E5.2.15.0", {"start": v(-125, 161.5) * mm, "end": v(-125, 171.5) * mm});
            skLineSegment(sketch, "E5.2.15.1", {"start": v(-115, 161.5) * mm, "end": v(-115, 171.5) * mm});
            skLineSegment(sketch, "E5.2.15.2", {"start": v(-125, 161.5) * mm, "end": v(-115, 161.5) * mm});
            skLineSegment(sketch, "E5.2.15.3", {"start": v(-125, 171.5) * mm, "end": v(-115, 171.5) * mm});
            skLineSegment(sketch, "E5.2.16.0", {"start": v(-125, 146.5) * mm, "end": v(-125, 156.5) * mm});
            skLineSegment(sketch, "E5.2.16.1", {"start": v(-115, 146.5) * mm, "end": v(-115, 156.5) * mm});
            skLineSegment(sketch, "E5.2.16.2", {"start": v(-125, 146.5) * mm, "end": v(-115, 146.5) * mm});
            skLineSegment(sketch, "E5.2.16.3", {"start": v(-125, 156.5) * mm, "end": v(-115, 156.5) * mm});
            skLineSegment(sketch, "E5.2.17.0", {"start": v(-125, 131.5) * mm, "end": v(-125, 141.5) * mm});
            skLineSegment(sketch, "E5.2.17.1", {"start": v(-115, 131.5) * mm, "end": v(-115, 141.5) * mm});
            skLineSegment(sketch, "E5.2.17.2", {"start": v(-125, 131.5) * mm, "end": v(-115, 131.5) * mm});
            skLineSegment(sketch, "E5.2.17.3", {"start": v(-125, 141.5) * mm, "end": v(-115, 141.5) * mm});
            skLineSegment(sketch, "E5.2.18.0", {"start": v(-125, 116.5) * mm, "end": v(-125, 126.5) * mm});
            skLineSegment(sketch, "E5.2.18.1", {"start": v(-115, 116.5) * mm, "end": v(-115, 126.5) * mm});
            skLineSegment(sketch, "E5.2.18.2", {"start": v(-125, 116.5) * mm, "end": v(-115, 116.5) * mm});
            skLineSegment(sketch, "E5.2.18.3", {"start": v(-125, 126.5) * mm, "end": v(-115, 126.5) * mm});
            skLineSegment(sketch, "E5.2.19.0", {"start": v(-125, 101.5) * mm, "end": v(-125, 111.5) * mm});
            skLineSegment(sketch, "E5.2.19.1", {"start": v(-115, 101.5) * mm, "end": v(-115, 111.5) * mm});
            skLineSegment(sketch, "E5.2.19.2", {"start": v(-125, 101.5) * mm, "end": v(-115, 101.5) * mm});
            skLineSegment(sketch, "E5.2.19.3", {"start": v(-125, 111.5) * mm, "end": v(-115, 111.5) * mm});
            skLineSegment(sketch, "E5.2.20.0", {"start": v(-125, 86.5) * mm, "end": v(-125, 96.5) * mm});
            skLineSegment(sketch, "E5.2.20.1", {"start": v(-115, 86.5) * mm, "end": v(-115, 96.5) * mm});
            skLineSegment(sketch, "E5.2.20.2", {"start": v(-125, 86.5) * mm, "end": v(-115, 86.5) * mm});
            skLineSegment(sketch, "E5.2.20.3", {"start": v(-125, 96.5) * mm, "end": v(-115, 96.5) * mm});
            skLineSegment(sketch, "E5.2.21.0", {"start": v(-125, 71.5) * mm, "end": v(-125, 81.5) * mm});
            skLineSegment(sketch, "E5.2.21.1", {"start": v(-115, 71.5) * mm, "end": v(-115, 81.5) * mm});
            skLineSegment(sketch, "E5.2.21.2", {"start": v(-125, 71.5) * mm, "end": v(-115, 71.5) * mm});
            skLineSegment(sketch, "E5.2.21.3", {"start": v(-125, 81.5) * mm, "end": v(-115, 81.5) * mm});
            skLineSegment(sketch, "E5.2.22.0", {"start": v(-125, 56.5) * mm, "end": v(-125, 66.5) * mm});
            skLineSegment(sketch, "E5.2.22.1", {"start": v(-115, 56.5) * mm, "end": v(-115, 66.5) * mm});
            skLineSegment(sketch, "E5.2.22.2", {"start": v(-125, 56.5) * mm, "end": v(-115, 56.5) * mm});
            skLineSegment(sketch, "E5.2.22.3", {"start": v(-125, 66.5) * mm, "end": v(-115, 66.5) * mm});
            skLineSegment(sketch, "E5.2.23.0", {"start": v(-125, 41.5) * mm, "end": v(-125, 51.5) * mm});
            skLineSegment(sketch, "E5.2.23.1", {"start": v(-115, 41.5) * mm, "end": v(-115, 51.5) * mm});
            skLineSegment(sketch, "E5.2.23.2", {"start": v(-125, 41.5) * mm, "end": v(-115, 41.5) * mm});
            skLineSegment(sketch, "E5.2.23.3", {"start": v(-125, 51.5) * mm, "end": v(-115, 51.5) * mm});
            skLineSegment(sketch, "E5.2.24.0", {"start": v(-125, 26.5) * mm, "end": v(-125, 36.5) * mm});
            skLineSegment(sketch, "E5.2.24.1", {"start": v(-115, 26.5) * mm, "end": v(-115, 36.5) * mm});
            skLineSegment(sketch, "E5.2.24.2", {"start": v(-125, 26.5) * mm, "end": v(-115, 26.5) * mm});
            skLineSegment(sketch, "E5.2.24.3", {"start": v(-125, 36.5) * mm, "end": v(-115, 36.5) * mm});
            skLineSegment(sketch, "E5.3.0.0", {"start": v(-110, 386.5) * mm, "end": v(-110, 396.5) * mm});
            skLineSegment(sketch, "E5.3.0.1", {"start": v(-100, 386.5) * mm, "end": v(-100, 396.5) * mm});
            skLineSegment(sketch, "E5.3.0.2", {"start": v(-110, 386.5) * mm, "end": v(-100, 386.5) * mm});
            skLineSegment(sketch, "E5.3.0.3", {"start": v(-110, 396.5) * mm, "end": v(-100, 396.5) * mm});
            skLineSegment(sketch, "E5.3.1.0", {"start": v(-110, 371.5) * mm, "end": v(-110, 381.5) * mm});
            skLineSegment(sketch, "E5.3.1.1", {"start": v(-100, 371.5) * mm, "end": v(-100, 381.5) * mm});
            skLineSegment(sketch, "E5.3.1.2", {"start": v(-110, 371.5) * mm, "end": v(-100, 371.5) * mm});
            skLineSegment(sketch, "E5.3.1.3", {"start": v(-110, 381.5) * mm, "end": v(-100, 381.5) * mm});
            skLineSegment(sketch, "E5.3.2.0", {"start": v(-110, 356.5) * mm, "end": v(-110, 366.5) * mm});
            skLineSegment(sketch, "E5.3.2.1", {"start": v(-100, 356.5) * mm, "end": v(-100, 366.5) * mm});
            skLineSegment(sketch, "E5.3.2.2", {"start": v(-110, 356.5) * mm, "end": v(-100, 356.5) * mm});
            skLineSegment(sketch, "E5.3.2.3", {"start": v(-110, 366.5) * mm, "end": v(-100, 366.5) * mm});
            skLineSegment(sketch, "E5.3.3.0", {"start": v(-110, 341.5) * mm, "end": v(-110, 351.5) * mm});
            skLineSegment(sketch, "E5.3.3.1", {"start": v(-100, 341.5) * mm, "end": v(-100, 351.5) * mm});
            skLineSegment(sketch, "E5.3.3.2", {"start": v(-110, 341.5) * mm, "end": v(-100, 341.5) * mm});
            skLineSegment(sketch, "E5.3.3.3", {"start": v(-110, 351.5) * mm, "end": v(-100, 351.5) * mm});
            skLineSegment(sketch, "E5.3.4.0", {"start": v(-110, 326.5) * mm, "end": v(-110, 336.5) * mm});
            skLineSegment(sketch, "E5.3.4.1", {"start": v(-100, 326.5) * mm, "end": v(-100, 336.5) * mm});
            skLineSegment(sketch, "E5.3.4.2", {"start": v(-110, 326.5) * mm, "end": v(-100, 326.5) * mm});
            skLineSegment(sketch, "E5.3.4.3", {"start": v(-110, 336.5) * mm, "end": v(-100, 336.5) * mm});
            skLineSegment(sketch, "E5.3.5.0", {"start": v(-110, 311.5) * mm, "end": v(-110, 321.5) * mm});
            skLineSegment(sketch, "E5.3.5.1", {"start": v(-100, 311.5) * mm, "end": v(-100, 321.5) * mm});
            skLineSegment(sketch, "E5.3.5.2", {"start": v(-110, 311.5) * mm, "end": v(-100, 311.5) * mm});
            skLineSegment(sketch, "E5.3.5.3", {"start": v(-110, 321.5) * mm, "end": v(-100, 321.5) * mm});
            skLineSegment(sketch, "E5.3.6.0", {"start": v(-110, 296.5) * mm, "end": v(-110, 306.5) * mm});
            skLineSegment(sketch, "E5.3.6.1", {"start": v(-100, 296.5) * mm, "end": v(-100, 306.5) * mm});
            skLineSegment(sketch, "E5.3.6.2", {"start": v(-110, 296.5) * mm, "end": v(-100, 296.5) * mm});
            skLineSegment(sketch, "E5.3.6.3", {"start": v(-110, 306.5) * mm, "end": v(-100, 306.5) * mm});
            skLineSegment(sketch, "E5.3.7.0", {"start": v(-110, 281.5) * mm, "end": v(-110, 291.5) * mm});
            skLineSegment(sketch, "E5.3.7.1", {"start": v(-100, 281.5) * mm, "end": v(-100, 291.5) * mm});
            skLineSegment(sketch, "E5.3.7.2", {"start": v(-110, 281.5) * mm, "end": v(-100, 281.5) * mm});
            skLineSegment(sketch, "E5.3.7.3", {"start": v(-110, 291.5) * mm, "end": v(-100, 291.5) * mm});
            skLineSegment(sketch, "E5.3.8.0", {"start": v(-110, 266.5) * mm, "end": v(-110, 276.5) * mm});
            skLineSegment(sketch, "E5.3.8.1", {"start": v(-100, 266.5) * mm, "end": v(-100, 276.5) * mm});
            skLineSegment(sketch, "E5.3.8.2", {"start": v(-110, 266.5) * mm, "end": v(-100, 266.5) * mm});
            skLineSegment(sketch, "E5.3.8.3", {"start": v(-110, 276.5) * mm, "end": v(-100, 276.5) * mm});
            skLineSegment(sketch, "E5.3.9.0", {"start": v(-110, 251.5) * mm, "end": v(-110, 261.5) * mm});
            skLineSegment(sketch, "E5.3.9.1", {"start": v(-100, 251.5) * mm, "end": v(-100, 261.5) * mm});
            skLineSegment(sketch, "E5.3.9.2", {"start": v(-110, 251.5) * mm, "end": v(-100, 251.5) * mm});
            skLineSegment(sketch, "E5.3.9.3", {"start": v(-110, 261.5) * mm, "end": v(-100, 261.5) * mm});
            skLineSegment(sketch, "E5.3.10.0", {"start": v(-110, 236.5) * mm, "end": v(-110, 246.5) * mm});
            skLineSegment(sketch, "E5.3.10.1", {"start": v(-100, 236.5) * mm, "end": v(-100, 246.5) * mm});
            skLineSegment(sketch, "E5.3.10.2", {"start": v(-110, 236.5) * mm, "end": v(-100, 236.5) * mm});
            skLineSegment(sketch, "E5.3.10.3", {"start": v(-110, 246.5) * mm, "end": v(-100, 246.5) * mm});
            skLineSegment(sketch, "E5.3.11.0", {"start": v(-110, 221.5) * mm, "end": v(-110, 231.5) * mm});
            skLineSegment(sketch, "E5.3.11.1", {"start": v(-100, 221.5) * mm, "end": v(-100, 231.5) * mm});
            skLineSegment(sketch, "E5.3.11.2", {"start": v(-110, 221.5) * mm, "end": v(-100, 221.5) * mm});
            skLineSegment(sketch, "E5.3.11.3", {"start": v(-110, 231.5) * mm, "end": v(-100, 231.5) * mm});
            skLineSegment(sketch, "E5.3.12.0", {"start": v(-110, 206.5) * mm, "end": v(-110, 216.5) * mm});
            skLineSegment(sketch, "E5.3.12.1", {"start": v(-100, 206.5) * mm, "end": v(-100, 216.5) * mm});
            skLineSegment(sketch, "E5.3.12.2", {"start": v(-110, 206.5) * mm, "end": v(-100, 206.5) * mm});
            skLineSegment(sketch, "E5.3.12.3", {"start": v(-110, 216.5) * mm, "end": v(-100, 216.5) * mm});
            skLineSegment(sketch, "E5.3.13.0", {"start": v(-110, 191.5) * mm, "end": v(-110, 201.5) * mm});
            skLineSegment(sketch, "E5.3.13.1", {"start": v(-100, 191.5) * mm, "end": v(-100, 201.5) * mm});
            skLineSegment(sketch, "E5.3.13.2", {"start": v(-110, 191.5) * mm, "end": v(-100, 191.5) * mm});
            skLineSegment(sketch, "E5.3.13.3", {"start": v(-110, 201.5) * mm, "end": v(-100, 201.5) * mm});
            skLineSegment(sketch, "E5.3.14.0", {"start": v(-110, 176.5) * mm, "end": v(-110, 186.5) * mm});
            skLineSegment(sketch, "E5.3.14.1", {"start": v(-100, 176.5) * mm, "end": v(-100, 186.5) * mm});
            skLineSegment(sketch, "E5.3.14.2", {"start": v(-110, 176.5) * mm, "end": v(-100, 176.5) * mm});
            skLineSegment(sketch, "E5.3.14.3", {"start": v(-110, 186.5) * mm, "end": v(-100, 186.5) * mm});
            skLineSegment(sketch, "E5.3.15.0", {"start": v(-110, 161.5) * mm, "end": v(-110, 171.5) * mm});
            skLineSegment(sketch, "E5.3.15.1", {"start": v(-100, 161.5) * mm, "end": v(-100, 171.5) * mm});
            skLineSegment(sketch, "E5.3.15.2", {"start": v(-110, 161.5) * mm, "end": v(-100, 161.5) * mm});
            skLineSegment(sketch, "E5.3.15.3", {"start": v(-110, 171.5) * mm, "end": v(-100, 171.5) * mm});
            skLineSegment(sketch, "E5.3.16.0", {"start": v(-110, 146.5) * mm, "end": v(-110, 156.5) * mm});
            skLineSegment(sketch, "E5.3.16.1", {"start": v(-100, 146.5) * mm, "end": v(-100, 156.5) * mm});
            skLineSegment(sketch, "E5.3.16.2", {"start": v(-110, 146.5) * mm, "end": v(-100, 146.5) * mm});
            skLineSegment(sketch, "E5.3.16.3", {"start": v(-110, 156.5) * mm, "end": v(-100, 156.5) * mm});
            skLineSegment(sketch, "E5.3.17.0", {"start": v(-110, 131.5) * mm, "end": v(-110, 141.5) * mm});
            skLineSegment(sketch, "E5.3.17.1", {"start": v(-100, 131.5) * mm, "end": v(-100, 141.5) * mm});
            skLineSegment(sketch, "E5.3.17.2", {"start": v(-110, 131.5) * mm, "end": v(-100, 131.5) * mm});
            skLineSegment(sketch, "E5.3.17.3", {"start": v(-110, 141.5) * mm, "end": v(-100, 141.5) * mm});
            skLineSegment(sketch, "E5.3.18.0", {"start": v(-110, 116.5) * mm, "end": v(-110, 126.5) * mm});
            skLineSegment(sketch, "E5.3.18.1", {"start": v(-100, 116.5) * mm, "end": v(-100, 126.5) * mm});
            skLineSegment(sketch, "E5.3.18.2", {"start": v(-110, 116.5) * mm, "end": v(-100, 116.5) * mm});
            skLineSegment(sketch, "E5.3.18.3", {"start": v(-110, 126.5) * mm, "end": v(-100, 126.5) * mm});
            skLineSegment(sketch, "E5.3.19.0", {"start": v(-110, 101.5) * mm, "end": v(-110, 111.5) * mm});
            skLineSegment(sketch, "E5.3.19.1", {"start": v(-100, 101.5) * mm, "end": v(-100, 111.5) * mm});
            skLineSegment(sketch, "E5.3.19.2", {"start": v(-110, 101.5) * mm, "end": v(-100, 101.5) * mm});
            skLineSegment(sketch, "E5.3.19.3", {"start": v(-110, 111.5) * mm, "end": v(-100, 111.5) * mm});
            skLineSegment(sketch, "E5.3.20.0", {"start": v(-110, 86.5) * mm, "end": v(-110, 96.5) * mm});
            skLineSegment(sketch, "E5.3.20.1", {"start": v(-100, 86.5) * mm, "end": v(-100, 96.5) * mm});
            skLineSegment(sketch, "E5.3.20.2", {"start": v(-110, 86.5) * mm, "end": v(-100, 86.5) * mm});
            skLineSegment(sketch, "E5.3.20.3", {"start": v(-110, 96.5) * mm, "end": v(-100, 96.5) * mm});
            skLineSegment(sketch, "E5.3.21.0", {"start": v(-110, 71.5) * mm, "end": v(-110, 81.5) * mm});
            skLineSegment(sketch, "E5.3.21.1", {"start": v(-100, 71.5) * mm, "end": v(-100, 81.5) * mm});
            skLineSegment(sketch, "E5.3.21.2", {"start": v(-110, 71.5) * mm, "end": v(-100, 71.5) * mm});
            skLineSegment(sketch, "E5.3.21.3", {"start": v(-110, 81.5) * mm, "end": v(-100, 81.5) * mm});
            skLineSegment(sketch, "E5.3.22.0", {"start": v(-110, 56.5) * mm, "end": v(-110, 66.5) * mm});
            skLineSegment(sketch, "E5.3.22.1", {"start": v(-100, 56.5) * mm, "end": v(-100, 66.5) * mm});
            skLineSegment(sketch, "E5.3.22.2", {"start": v(-110, 56.5) * mm, "end": v(-100, 56.5) * mm});
            skLineSegment(sketch, "E5.3.22.3", {"start": v(-110, 66.5) * mm, "end": v(-100, 66.5) * mm});
            skLineSegment(sketch, "E5.3.23.0", {"start": v(-110, 41.5) * mm, "end": v(-110, 51.5) * mm});
            skLineSegment(sketch, "E5.3.23.1", {"start": v(-100, 41.5) * mm, "end": v(-100, 51.5) * mm});
            skLineSegment(sketch, "E5.3.23.2", {"start": v(-110, 41.5) * mm, "end": v(-100, 41.5) * mm});
            skLineSegment(sketch, "E5.3.23.3", {"start": v(-110, 51.5) * mm, "end": v(-100, 51.5) * mm});
            skLineSegment(sketch, "E5.3.24.0", {"start": v(-110, 26.5) * mm, "end": v(-110, 36.5) * mm});
            skLineSegment(sketch, "E5.3.24.1", {"start": v(-100, 26.5) * mm, "end": v(-100, 36.5) * mm});
            skLineSegment(sketch, "E5.3.24.2", {"start": v(-110, 26.5) * mm, "end": v(-100, 26.5) * mm});
            skLineSegment(sketch, "E5.3.24.3", {"start": v(-110, 36.5) * mm, "end": v(-100, 36.5) * mm});
            skLineSegment(sketch, "E5.4.0.0", {"start": v(-95, 386.5) * mm, "end": v(-95, 396.5) * mm});
            skLineSegment(sketch, "E5.4.0.1", {"start": v(-85, 386.5) * mm, "end": v(-85, 396.5) * mm});
            skLineSegment(sketch, "E5.4.0.2", {"start": v(-95, 386.5) * mm, "end": v(-85, 386.5) * mm});
            skLineSegment(sketch, "E5.4.0.3", {"start": v(-95, 396.5) * mm, "end": v(-85, 396.5) * mm});
            skLineSegment(sketch, "E5.4.1.0", {"start": v(-95, 371.5) * mm, "end": v(-95, 381.5) * mm});
            skLineSegment(sketch, "E5.4.1.1", {"start": v(-85, 371.5) * mm, "end": v(-85, 381.5) * mm});
            skLineSegment(sketch, "E5.4.1.2", {"start": v(-95, 371.5) * mm, "end": v(-85, 371.5) * mm});
            skLineSegment(sketch, "E5.4.1.3", {"start": v(-95, 381.5) * mm, "end": v(-85, 381.5) * mm});
            skLineSegment(sketch, "E5.4.2.0", {"start": v(-95, 356.5) * mm, "end": v(-95, 366.5) * mm});
            skLineSegment(sketch, "E5.4.2.1", {"start": v(-85, 356.5) * mm, "end": v(-85, 366.5) * mm});
            skLineSegment(sketch, "E5.4.2.2", {"start": v(-95, 356.5) * mm, "end": v(-85, 356.5) * mm});
            skLineSegment(sketch, "E5.4.2.3", {"start": v(-95, 366.5) * mm, "end": v(-85, 366.5) * mm});
            skLineSegment(sketch, "E5.4.3.0", {"start": v(-95, 341.5) * mm, "end": v(-95, 351.5) * mm});
            skLineSegment(sketch, "E5.4.3.1", {"start": v(-85, 341.5) * mm, "end": v(-85, 351.5) * mm});
            skLineSegment(sketch, "E5.4.3.2", {"start": v(-95, 341.5) * mm, "end": v(-85, 341.5) * mm});
            skLineSegment(sketch, "E5.4.3.3", {"start": v(-95, 351.5) * mm, "end": v(-85, 351.5) * mm});
            skLineSegment(sketch, "E5.4.4.0", {"start": v(-95, 326.5) * mm, "end": v(-95, 336.5) * mm});
            skLineSegment(sketch, "E5.4.4.1", {"start": v(-85, 326.5) * mm, "end": v(-85, 336.5) * mm});
            skLineSegment(sketch, "E5.4.4.2", {"start": v(-95, 326.5) * mm, "end": v(-85, 326.5) * mm});
            skLineSegment(sketch, "E5.4.4.3", {"start": v(-95, 336.5) * mm, "end": v(-85, 336.5) * mm});
            skLineSegment(sketch, "E5.4.5.0", {"start": v(-95, 311.5) * mm, "end": v(-95, 321.5) * mm});
            skLineSegment(sketch, "E5.4.5.1", {"start": v(-85, 311.5) * mm, "end": v(-85, 321.5) * mm});
            skLineSegment(sketch, "E5.4.5.2", {"start": v(-95, 311.5) * mm, "end": v(-85, 311.5) * mm});
            skLineSegment(sketch, "E5.4.5.3", {"start": v(-95, 321.5) * mm, "end": v(-85, 321.5) * mm});
            skLineSegment(sketch, "E5.4.6.0", {"start": v(-95, 296.5) * mm, "end": v(-95, 306.5) * mm});
            skLineSegment(sketch, "E5.4.6.1", {"start": v(-85, 296.5) * mm, "end": v(-85, 306.5) * mm});
            skLineSegment(sketch, "E5.4.6.2", {"start": v(-95, 296.5) * mm, "end": v(-85, 296.5) * mm});
            skLineSegment(sketch, "E5.4.6.3", {"start": v(-95, 306.5) * mm, "end": v(-85, 306.5) * mm});
            skLineSegment(sketch, "E5.4.7.0", {"start": v(-95, 281.5) * mm, "end": v(-95, 291.5) * mm});
            skLineSegment(sketch, "E5.4.7.1", {"start": v(-85, 281.5) * mm, "end": v(-85, 291.5) * mm});
            skLineSegment(sketch, "E5.4.7.2", {"start": v(-95, 281.5) * mm, "end": v(-85, 281.5) * mm});
            skLineSegment(sketch, "E5.4.7.3", {"start": v(-95, 291.5) * mm, "end": v(-85, 291.5) * mm});
            skLineSegment(sketch, "E5.4.8.0", {"start": v(-95, 266.5) * mm, "end": v(-95, 276.5) * mm});
            skLineSegment(sketch, "E5.4.8.1", {"start": v(-85, 266.5) * mm, "end": v(-85, 276.5) * mm});
            skLineSegment(sketch, "E5.4.8.2", {"start": v(-95, 266.5) * mm, "end": v(-85, 266.5) * mm});
            skLineSegment(sketch, "E5.4.8.3", {"start": v(-95, 276.5) * mm, "end": v(-85, 276.5) * mm});
            skLineSegment(sketch, "E5.4.9.0", {"start": v(-95, 251.5) * mm, "end": v(-95, 261.5) * mm});
            skLineSegment(sketch, "E5.4.9.1", {"start": v(-85, 251.5) * mm, "end": v(-85, 261.5) * mm});
            skLineSegment(sketch, "E5.4.9.2", {"start": v(-95, 251.5) * mm, "end": v(-85, 251.5) * mm});
            skLineSegment(sketch, "E5.4.9.3", {"start": v(-95, 261.5) * mm, "end": v(-85, 261.5) * mm});
            skLineSegment(sketch, "E5.4.10.0", {"start": v(-95, 236.5) * mm, "end": v(-95, 246.5) * mm});
            skLineSegment(sketch, "E5.4.10.1", {"start": v(-85, 236.5) * mm, "end": v(-85, 246.5) * mm});
            skLineSegment(sketch, "E5.4.10.2", {"start": v(-95, 236.5) * mm, "end": v(-85, 236.5) * mm});
            skLineSegment(sketch, "E5.4.10.3", {"start": v(-95, 246.5) * mm, "end": v(-85, 246.5) * mm});
            skLineSegment(sketch, "E5.4.11.0", {"start": v(-95, 221.5) * mm, "end": v(-95, 231.5) * mm});
            skLineSegment(sketch, "E5.4.11.1", {"start": v(-85, 221.5) * mm, "end": v(-85, 231.5) * mm});
            skLineSegment(sketch, "E5.4.11.2", {"start": v(-95, 221.5) * mm, "end": v(-85, 221.5) * mm});
            skLineSegment(sketch, "E5.4.11.3", {"start": v(-95, 231.5) * mm, "end": v(-85, 231.5) * mm});
            skLineSegment(sketch, "E5.4.12.0", {"start": v(-95, 206.5) * mm, "end": v(-95, 216.5) * mm});
            skLineSegment(sketch, "E5.4.12.1", {"start": v(-85, 206.5) * mm, "end": v(-85, 216.5) * mm});
            skLineSegment(sketch, "E5.4.12.2", {"start": v(-95, 206.5) * mm, "end": v(-85, 206.5) * mm});
            skLineSegment(sketch, "E5.4.12.3", {"start": v(-95, 216.5) * mm, "end": v(-85, 216.5) * mm});
            skLineSegment(sketch, "E5.4.13.0", {"start": v(-95, 191.5) * mm, "end": v(-95, 201.5) * mm});
            skLineSegment(sketch, "E5.4.13.1", {"start": v(-85, 191.5) * mm, "end": v(-85, 201.5) * mm});
            skLineSegment(sketch, "E5.4.13.2", {"start": v(-95, 191.5) * mm, "end": v(-85, 191.5) * mm});
            skLineSegment(sketch, "E5.4.13.3", {"start": v(-95, 201.5) * mm, "end": v(-85, 201.5) * mm});
            skLineSegment(sketch, "E5.4.14.0", {"start": v(-95, 176.5) * mm, "end": v(-95, 186.5) * mm});
            skLineSegment(sketch, "E5.4.14.1", {"start": v(-85, 176.5) * mm, "end": v(-85, 186.5) * mm});
            skLineSegment(sketch, "E5.4.14.2", {"start": v(-95, 176.5) * mm, "end": v(-85, 176.5) * mm});
            skLineSegment(sketch, "E5.4.14.3", {"start": v(-95, 186.5) * mm, "end": v(-85, 186.5) * mm});
            skLineSegment(sketch, "E5.4.15.0", {"start": v(-95, 161.5) * mm, "end": v(-95, 171.5) * mm});
            skLineSegment(sketch, "E5.4.15.1", {"start": v(-85, 161.5) * mm, "end": v(-85, 171.5) * mm});
            skLineSegment(sketch, "E5.4.15.2", {"start": v(-95, 161.5) * mm, "end": v(-85, 161.5) * mm});
            skLineSegment(sketch, "E5.4.15.3", {"start": v(-95, 171.5) * mm, "end": v(-85, 171.5) * mm});
            skLineSegment(sketch, "E5.4.16.0", {"start": v(-95, 146.5) * mm, "end": v(-95, 156.5) * mm});
            skLineSegment(sketch, "E5.4.16.1", {"start": v(-85, 146.5) * mm, "end": v(-85, 156.5) * mm});
            skLineSegment(sketch, "E5.4.16.2", {"start": v(-95, 146.5) * mm, "end": v(-85, 146.5) * mm});
            skLineSegment(sketch, "E5.4.16.3", {"start": v(-95, 156.5) * mm, "end": v(-85, 156.5) * mm});
            skLineSegment(sketch, "E5.4.17.0", {"start": v(-95, 131.5) * mm, "end": v(-95, 141.5) * mm});
            skLineSegment(sketch, "E5.4.17.1", {"start": v(-85, 131.5) * mm, "end": v(-85, 141.5) * mm});
            skLineSegment(sketch, "E5.4.17.2", {"start": v(-95, 131.5) * mm, "end": v(-85, 131.5) * mm});
            skLineSegment(sketch, "E5.4.17.3", {"start": v(-95, 141.5) * mm, "end": v(-85, 141.5) * mm});
            skLineSegment(sketch, "E5.4.18.0", {"start": v(-95, 116.5) * mm, "end": v(-95, 126.5) * mm});
            skLineSegment(sketch, "E5.4.18.1", {"start": v(-85, 116.5) * mm, "end": v(-85, 126.5) * mm});
            skLineSegment(sketch, "E5.4.18.2", {"start": v(-95, 116.5) * mm, "end": v(-85, 116.5) * mm});
            skLineSegment(sketch, "E5.4.18.3", {"start": v(-95, 126.5) * mm, "end": v(-85, 126.5) * mm});
            skLineSegment(sketch, "E5.4.19.0", {"start": v(-95, 101.5) * mm, "end": v(-95, 111.5) * mm});
            skLineSegment(sketch, "E5.4.19.1", {"start": v(-85, 101.5) * mm, "end": v(-85, 111.5) * mm});
            skLineSegment(sketch, "E5.4.19.2", {"start": v(-95, 101.5) * mm, "end": v(-85, 101.5) * mm});
            skLineSegment(sketch, "E5.4.19.3", {"start": v(-95, 111.5) * mm, "end": v(-85, 111.5) * mm});
            skLineSegment(sketch, "E5.4.20.0", {"start": v(-95, 86.5) * mm, "end": v(-95, 96.5) * mm});
            skLineSegment(sketch, "E5.4.20.1", {"start": v(-85, 86.5) * mm, "end": v(-85, 96.5) * mm});
            skLineSegment(sketch, "E5.4.20.2", {"start": v(-95, 86.5) * mm, "end": v(-85, 86.5) * mm});
            skLineSegment(sketch, "E5.4.20.3", {"start": v(-95, 96.5) * mm, "end": v(-85, 96.5) * mm});
            skLineSegment(sketch, "E5.4.21.0", {"start": v(-95, 71.5) * mm, "end": v(-95, 81.5) * mm});
            skLineSegment(sketch, "E5.4.21.1", {"start": v(-85, 71.5) * mm, "end": v(-85, 81.5) * mm});
            skLineSegment(sketch, "E5.4.21.2", {"start": v(-95, 71.5) * mm, "end": v(-85, 71.5) * mm});
            skLineSegment(sketch, "E5.4.21.3", {"start": v(-95, 81.5) * mm, "end": v(-85, 81.5) * mm});
            skLineSegment(sketch, "E5.4.22.0", {"start": v(-95, 56.5) * mm, "end": v(-95, 66.5) * mm});
            skLineSegment(sketch, "E5.4.22.1", {"start": v(-85, 56.5) * mm, "end": v(-85, 66.5) * mm});
            skLineSegment(sketch, "E5.4.22.2", {"start": v(-95, 56.5) * mm, "end": v(-85, 56.5) * mm});
            skLineSegment(sketch, "E5.4.22.3", {"start": v(-95, 66.5) * mm, "end": v(-85, 66.5) * mm});
            skLineSegment(sketch, "E5.4.23.0", {"start": v(-95, 41.5) * mm, "end": v(-95, 51.5) * mm});
            skLineSegment(sketch, "E5.4.23.1", {"start": v(-85, 41.5) * mm, "end": v(-85, 51.5) * mm});
            skLineSegment(sketch, "E5.4.23.2", {"start": v(-95, 41.5) * mm, "end": v(-85, 41.5) * mm});
            skLineSegment(sketch, "E5.4.23.3", {"start": v(-95, 51.5) * mm, "end": v(-85, 51.5) * mm});
            skLineSegment(sketch, "E5.4.24.0", {"start": v(-95, 26.5) * mm, "end": v(-95, 36.5) * mm});
            skLineSegment(sketch, "E5.4.24.1", {"start": v(-85, 26.5) * mm, "end": v(-85, 36.5) * mm});
            skLineSegment(sketch, "E5.4.24.2", {"start": v(-95, 26.5) * mm, "end": v(-85, 26.5) * mm});
            skLineSegment(sketch, "E5.4.24.3", {"start": v(-95, 36.5) * mm, "end": v(-85, 36.5) * mm});
            skLineSegment(sketch, "E5.5.0.0", {"start": v(-80, 386.5) * mm, "end": v(-80, 396.5) * mm});
            skLineSegment(sketch, "E5.5.0.1", {"start": v(-70, 386.5) * mm, "end": v(-70, 396.5) * mm});
            skLineSegment(sketch, "E5.5.0.2", {"start": v(-80, 386.5) * mm, "end": v(-70, 386.5) * mm});
            skLineSegment(sketch, "E5.5.0.3", {"start": v(-80, 396.5) * mm, "end": v(-70, 396.5) * mm});
            skLineSegment(sketch, "E5.5.1.0", {"start": v(-80, 371.5) * mm, "end": v(-80, 381.5) * mm});
            skLineSegment(sketch, "E5.5.1.1", {"start": v(-70, 371.5) * mm, "end": v(-70, 381.5) * mm});
            skLineSegment(sketch, "E5.5.1.2", {"start": v(-80, 371.5) * mm, "end": v(-70, 371.5) * mm});
            skLineSegment(sketch, "E5.5.1.3", {"start": v(-80, 381.5) * mm, "end": v(-70, 381.5) * mm});
            skLineSegment(sketch, "E5.5.2.0", {"start": v(-80, 356.5) * mm, "end": v(-80, 366.5) * mm});
            skLineSegment(sketch, "E5.5.2.1", {"start": v(-70, 356.5) * mm, "end": v(-70, 366.5) * mm});
            skLineSegment(sketch, "E5.5.2.2", {"start": v(-80, 356.5) * mm, "end": v(-70, 356.5) * mm});
            skLineSegment(sketch, "E5.5.2.3", {"start": v(-80, 366.5) * mm, "end": v(-70, 366.5) * mm});
            skLineSegment(sketch, "E5.5.3.0", {"start": v(-80, 341.5) * mm, "end": v(-80, 351.5) * mm});
            skLineSegment(sketch, "E5.5.3.1", {"start": v(-70, 341.5) * mm, "end": v(-70, 351.5) * mm});
            skLineSegment(sketch, "E5.5.3.2", {"start": v(-80, 341.5) * mm, "end": v(-70, 341.5) * mm});
            skLineSegment(sketch, "E5.5.3.3", {"start": v(-80, 351.5) * mm, "end": v(-70, 351.5) * mm});
            skLineSegment(sketch, "E5.5.4.0", {"start": v(-80, 326.5) * mm, "end": v(-80, 336.5) * mm});
            skLineSegment(sketch, "E5.5.4.1", {"start": v(-70, 326.5) * mm, "end": v(-70, 336.5) * mm});
            skLineSegment(sketch, "E5.5.4.2", {"start": v(-80, 326.5) * mm, "end": v(-70, 326.5) * mm});
            skLineSegment(sketch, "E5.5.4.3", {"start": v(-80, 336.5) * mm, "end": v(-70, 336.5) * mm});
            skLineSegment(sketch, "E5.5.5.0", {"start": v(-80, 311.5) * mm, "end": v(-80, 321.5) * mm});
            skLineSegment(sketch, "E5.5.5.1", {"start": v(-70, 311.5) * mm, "end": v(-70, 321.5) * mm});
            skLineSegment(sketch, "E5.5.5.2", {"start": v(-80, 311.5) * mm, "end": v(-70, 311.5) * mm});
            skLineSegment(sketch, "E5.5.5.3", {"start": v(-80, 321.5) * mm, "end": v(-70, 321.5) * mm});
            skLineSegment(sketch, "E5.5.6.0", {"start": v(-80, 296.5) * mm, "end": v(-80, 306.5) * mm});
            skLineSegment(sketch, "E5.5.6.1", {"start": v(-70, 296.5) * mm, "end": v(-70, 306.5) * mm});
            skLineSegment(sketch, "E5.5.6.2", {"start": v(-80, 296.5) * mm, "end": v(-70, 296.5) * mm});
            skLineSegment(sketch, "E5.5.6.3", {"start": v(-80, 306.5) * mm, "end": v(-70, 306.5) * mm});
            skLineSegment(sketch, "E5.5.7.0", {"start": v(-80, 281.5) * mm, "end": v(-80, 291.5) * mm});
            skLineSegment(sketch, "E5.5.7.1", {"start": v(-70, 281.5) * mm, "end": v(-70, 291.5) * mm});
            skLineSegment(sketch, "E5.5.7.2", {"start": v(-80, 281.5) * mm, "end": v(-70, 281.5) * mm});
            skLineSegment(sketch, "E5.5.7.3", {"start": v(-80, 291.5) * mm, "end": v(-70, 291.5) * mm});
            skLineSegment(sketch, "E5.5.8.0", {"start": v(-80, 266.5) * mm, "end": v(-80, 276.5) * mm});
            skLineSegment(sketch, "E5.5.8.1", {"start": v(-70, 266.5) * mm, "end": v(-70, 276.5) * mm});
            skLineSegment(sketch, "E5.5.8.2", {"start": v(-80, 266.5) * mm, "end": v(-70, 266.5) * mm});
            skLineSegment(sketch, "E5.5.8.3", {"start": v(-80, 276.5) * mm, "end": v(-70, 276.5) * mm});
            skLineSegment(sketch, "E5.5.9.0", {"start": v(-80, 251.5) * mm, "end": v(-80, 261.5) * mm});
            skLineSegment(sketch, "E5.5.9.1", {"start": v(-70, 251.5) * mm, "end": v(-70, 261.5) * mm});
            skLineSegment(sketch, "E5.5.9.2", {"start": v(-80, 251.5) * mm, "end": v(-70, 251.5) * mm});
            skLineSegment(sketch, "E5.5.9.3", {"start": v(-80, 261.5) * mm, "end": v(-70, 261.5) * mm});
            skLineSegment(sketch, "E5.5.10.0", {"start": v(-80, 236.5) * mm, "end": v(-80, 246.5) * mm});
            skLineSegment(sketch, "E5.5.10.1", {"start": v(-70, 236.5) * mm, "end": v(-70, 246.5) * mm});
            skLineSegment(sketch, "E5.5.10.2", {"start": v(-80, 236.5) * mm, "end": v(-70, 236.5) * mm});
            skLineSegment(sketch, "E5.5.10.3", {"start": v(-80, 246.5) * mm, "end": v(-70, 246.5) * mm});
            skLineSegment(sketch, "E5.5.11.0", {"start": v(-80, 221.5) * mm, "end": v(-80, 231.5) * mm});
            skLineSegment(sketch, "E5.5.11.1", {"start": v(-70, 221.5) * mm, "end": v(-70, 231.5) * mm});
            skLineSegment(sketch, "E5.5.11.2", {"start": v(-80, 221.5) * mm, "end": v(-70, 221.5) * mm});
            skLineSegment(sketch, "E5.5.11.3", {"start": v(-80, 231.5) * mm, "end": v(-70, 231.5) * mm});
            skLineSegment(sketch, "E5.5.12.0", {"start": v(-80, 206.5) * mm, "end": v(-80, 216.5) * mm});
            skLineSegment(sketch, "E5.5.12.1", {"start": v(-70, 206.5) * mm, "end": v(-70, 216.5) * mm});
            skLineSegment(sketch, "E5.5.12.2", {"start": v(-80, 206.5) * mm, "end": v(-70, 206.5) * mm});
            skLineSegment(sketch, "E5.5.12.3", {"start": v(-80, 216.5) * mm, "end": v(-70, 216.5) * mm});
            skLineSegment(sketch, "E5.5.13.0", {"start": v(-80, 191.5) * mm, "end": v(-80, 201.5) * mm});
            skLineSegment(sketch, "E5.5.13.1", {"start": v(-70, 191.5) * mm, "end": v(-70, 201.5) * mm});
            skLineSegment(sketch, "E5.5.13.2", {"start": v(-80, 191.5) * mm, "end": v(-70, 191.5) * mm});
            skLineSegment(sketch, "E5.5.13.3", {"start": v(-80, 201.5) * mm, "end": v(-70, 201.5) * mm});
            skLineSegment(sketch, "E5.5.14.0", {"start": v(-80, 176.5) * mm, "end": v(-80, 186.5) * mm});
            skLineSegment(sketch, "E5.5.14.1", {"start": v(-70, 176.5) * mm, "end": v(-70, 186.5) * mm});
            skLineSegment(sketch, "E5.5.14.2", {"start": v(-80, 176.5) * mm, "end": v(-70, 176.5) * mm});
            skLineSegment(sketch, "E5.5.14.3", {"start": v(-80, 186.5) * mm, "end": v(-70, 186.5) * mm});
            skLineSegment(sketch, "E5.5.15.0", {"start": v(-80, 161.5) * mm, "end": v(-80, 171.5) * mm});
            skLineSegment(sketch, "E5.5.15.1", {"start": v(-70, 161.5) * mm, "end": v(-70, 171.5) * mm});
            skLineSegment(sketch, "E5.5.15.2", {"start": v(-80, 161.5) * mm, "end": v(-70, 161.5) * mm});
            skLineSegment(sketch, "E5.5.15.3", {"start": v(-80, 171.5) * mm, "end": v(-70, 171.5) * mm});
            skLineSegment(sketch, "E5.5.16.0", {"start": v(-80, 146.5) * mm, "end": v(-80, 156.5) * mm});
            skLineSegment(sketch, "E5.5.16.1", {"start": v(-70, 146.5) * mm, "end": v(-70, 156.5) * mm});
            skLineSegment(sketch, "E5.5.16.2", {"start": v(-80, 146.5) * mm, "end": v(-70, 146.5) * mm});
            skLineSegment(sketch, "E5.5.16.3", {"start": v(-80, 156.5) * mm, "end": v(-70, 156.5) * mm});
            skLineSegment(sketch, "E5.5.17.0", {"start": v(-80, 131.5) * mm, "end": v(-80, 141.5) * mm});
            skLineSegment(sketch, "E5.5.17.1", {"start": v(-70, 131.5) * mm, "end": v(-70, 141.5) * mm});
            skLineSegment(sketch, "E5.5.17.2", {"start": v(-80, 131.5) * mm, "end": v(-70, 131.5) * mm});
            skLineSegment(sketch, "E5.5.17.3", {"start": v(-80, 141.5) * mm, "end": v(-70, 141.5) * mm});
            skLineSegment(sketch, "E5.5.18.0", {"start": v(-80, 116.5) * mm, "end": v(-80, 126.5) * mm});
            skLineSegment(sketch, "E5.5.18.1", {"start": v(-70, 116.5) * mm, "end": v(-70, 126.5) * mm});
            skLineSegment(sketch, "E5.5.18.2", {"start": v(-80, 116.5) * mm, "end": v(-70, 116.5) * mm});
            skLineSegment(sketch, "E5.5.18.3", {"start": v(-80, 126.5) * mm, "end": v(-70, 126.5) * mm});
            skLineSegment(sketch, "E5.5.19.0", {"start": v(-80, 101.5) * mm, "end": v(-80, 111.5) * mm});
            skLineSegment(sketch, "E5.5.19.1", {"start": v(-70, 101.5) * mm, "end": v(-70, 111.5) * mm});
            skLineSegment(sketch, "E5.5.19.2", {"start": v(-80, 101.5) * mm, "end": v(-70, 101.5) * mm});
            skLineSegment(sketch, "E5.5.19.3", {"start": v(-80, 111.5) * mm, "end": v(-70, 111.5) * mm});
            skLineSegment(sketch, "E5.5.20.0", {"start": v(-80, 86.5) * mm, "end": v(-80, 96.5) * mm});
            skLineSegment(sketch, "E5.5.20.1", {"start": v(-70, 86.5) * mm, "end": v(-70, 96.5) * mm});
            skLineSegment(sketch, "E5.5.20.2", {"start": v(-80, 86.5) * mm, "end": v(-70, 86.5) * mm});
            skLineSegment(sketch, "E5.5.20.3", {"start": v(-80, 96.5) * mm, "end": v(-70, 96.5) * mm});
            skLineSegment(sketch, "E5.5.21.0", {"start": v(-80, 71.5) * mm, "end": v(-80, 81.5) * mm});
            skLineSegment(sketch, "E5.5.21.1", {"start": v(-70, 71.5) * mm, "end": v(-70, 81.5) * mm});
            skLineSegment(sketch, "E5.5.21.2", {"start": v(-80, 71.5) * mm, "end": v(-70, 71.5) * mm});
            skLineSegment(sketch, "E5.5.21.3", {"start": v(-80, 81.5) * mm, "end": v(-70, 81.5) * mm});
            skLineSegment(sketch, "E5.5.22.0", {"start": v(-80, 56.5) * mm, "end": v(-80, 66.5) * mm});
            skLineSegment(sketch, "E5.5.22.1", {"start": v(-70, 56.5) * mm, "end": v(-70, 66.5) * mm});
            skLineSegment(sketch, "E5.5.22.2", {"start": v(-80, 56.5) * mm, "end": v(-70, 56.5) * mm});
            skLineSegment(sketch, "E5.5.22.3", {"start": v(-80, 66.5) * mm, "end": v(-70, 66.5) * mm});
            skLineSegment(sketch, "E5.5.23.0", {"start": v(-80, 41.5) * mm, "end": v(-80, 51.5) * mm});
            skLineSegment(sketch, "E5.5.23.1", {"start": v(-70, 41.5) * mm, "end": v(-70, 51.5) * mm});
            skLineSegment(sketch, "E5.5.23.2", {"start": v(-80, 41.5) * mm, "end": v(-70, 41.5) * mm});
            skLineSegment(sketch, "E5.5.23.3", {"start": v(-80, 51.5) * mm, "end": v(-70, 51.5) * mm});
            skLineSegment(sketch, "E5.5.24.0", {"start": v(-80, 26.5) * mm, "end": v(-80, 36.5) * mm});
            skLineSegment(sketch, "E5.5.24.1", {"start": v(-70, 26.5) * mm, "end": v(-70, 36.5) * mm});
            skLineSegment(sketch, "E5.5.24.2", {"start": v(-80, 26.5) * mm, "end": v(-70, 26.5) * mm});
            skLineSegment(sketch, "E5.5.24.3", {"start": v(-80, 36.5) * mm, "end": v(-70, 36.5) * mm});
            skLineSegment(sketch, "E5.6.0.0", {"start": v(-65, 386.5) * mm, "end": v(-65, 396.5) * mm});
            skLineSegment(sketch, "E5.6.0.1", {"start": v(-55, 386.5) * mm, "end": v(-55, 396.5) * mm});
            skLineSegment(sketch, "E5.6.0.2", {"start": v(-65, 386.5) * mm, "end": v(-55, 386.5) * mm});
            skLineSegment(sketch, "E5.6.0.3", {"start": v(-65, 396.5) * mm, "end": v(-55, 396.5) * mm});
            skLineSegment(sketch, "E5.6.1.0", {"start": v(-65, 371.5) * mm, "end": v(-65, 381.5) * mm});
            skLineSegment(sketch, "E5.6.1.1", {"start": v(-55, 371.5) * mm, "end": v(-55, 381.5) * mm});
            skLineSegment(sketch, "E5.6.1.2", {"start": v(-65, 371.5) * mm, "end": v(-55, 371.5) * mm});
            skLineSegment(sketch, "E5.6.1.3", {"start": v(-65, 381.5) * mm, "end": v(-55, 381.5) * mm});
            skLineSegment(sketch, "E5.6.2.0", {"start": v(-65, 356.5) * mm, "end": v(-65, 366.5) * mm});
            skLineSegment(sketch, "E5.6.2.1", {"start": v(-55, 356.5) * mm, "end": v(-55, 366.5) * mm});
            skLineSegment(sketch, "E5.6.2.2", {"start": v(-65, 356.5) * mm, "end": v(-55, 356.5) * mm});
            skLineSegment(sketch, "E5.6.2.3", {"start": v(-65, 366.5) * mm, "end": v(-55, 366.5) * mm});
            skLineSegment(sketch, "E5.6.3.0", {"start": v(-65, 341.5) * mm, "end": v(-65, 351.5) * mm});
            skLineSegment(sketch, "E5.6.3.1", {"start": v(-55, 341.5) * mm, "end": v(-55, 351.5) * mm});
            skLineSegment(sketch, "E5.6.3.2", {"start": v(-65, 341.5) * mm, "end": v(-55, 341.5) * mm});
            skLineSegment(sketch, "E5.6.3.3", {"start": v(-65, 351.5) * mm, "end": v(-55, 351.5) * mm});
            skLineSegment(sketch, "E5.6.4.0", {"start": v(-65, 326.5) * mm, "end": v(-65, 336.5) * mm});
            skLineSegment(sketch, "E5.6.4.1", {"start": v(-55, 326.5) * mm, "end": v(-55, 336.5) * mm});
            skLineSegment(sketch, "E5.6.4.2", {"start": v(-65, 326.5) * mm, "end": v(-55, 326.5) * mm});
            skLineSegment(sketch, "E5.6.4.3", {"start": v(-65, 336.5) * mm, "end": v(-55, 336.5) * mm});
            skLineSegment(sketch, "E5.6.5.0", {"start": v(-65, 311.5) * mm, "end": v(-65, 321.5) * mm});
            skLineSegment(sketch, "E5.6.5.1", {"start": v(-55, 311.5) * mm, "end": v(-55, 321.5) * mm});
            skLineSegment(sketch, "E5.6.5.2", {"start": v(-65, 311.5) * mm, "end": v(-55, 311.5) * mm});
            skLineSegment(sketch, "E5.6.5.3", {"start": v(-65, 321.5) * mm, "end": v(-55, 321.5) * mm});
            skLineSegment(sketch, "E5.6.6.0", {"start": v(-65, 296.5) * mm, "end": v(-65, 306.5) * mm});
            skLineSegment(sketch, "E5.6.6.1", {"start": v(-55, 296.5) * mm, "end": v(-55, 306.5) * mm});
            skLineSegment(sketch, "E5.6.6.2", {"start": v(-65, 296.5) * mm, "end": v(-55, 296.5) * mm});
            skLineSegment(sketch, "E5.6.6.3", {"start": v(-65, 306.5) * mm, "end": v(-55, 306.5) * mm});
            skLineSegment(sketch, "E5.6.7.0", {"start": v(-65, 281.5) * mm, "end": v(-65, 291.5) * mm});
            skLineSegment(sketch, "E5.6.7.1", {"start": v(-55, 281.5) * mm, "end": v(-55, 291.5) * mm});
            skLineSegment(sketch, "E5.6.7.2", {"start": v(-65, 281.5) * mm, "end": v(-55, 281.5) * mm});
            skLineSegment(sketch, "E5.6.7.3", {"start": v(-65, 291.5) * mm, "end": v(-55, 291.5) * mm});
            skLineSegment(sketch, "E5.6.8.0", {"start": v(-65, 266.5) * mm, "end": v(-65, 276.5) * mm});
            skLineSegment(sketch, "E5.6.8.1", {"start": v(-55, 266.5) * mm, "end": v(-55, 276.5) * mm});
            skLineSegment(sketch, "E5.6.8.2", {"start": v(-65, 266.5) * mm, "end": v(-55, 266.5) * mm});
            skLineSegment(sketch, "E5.6.8.3", {"start": v(-65, 276.5) * mm, "end": v(-55, 276.5) * mm});
            skLineSegment(sketch, "E5.6.9.0", {"start": v(-65, 251.5) * mm, "end": v(-65, 261.5) * mm});
            skLineSegment(sketch, "E5.6.9.1", {"start": v(-55, 251.5) * mm, "end": v(-55, 261.5) * mm});
            skLineSegment(sketch, "E5.6.9.2", {"start": v(-65, 251.5) * mm, "end": v(-55, 251.5) * mm});
            skLineSegment(sketch, "E5.6.9.3", {"start": v(-65, 261.5) * mm, "end": v(-55, 261.5) * mm});
            skLineSegment(sketch, "E5.6.10.0", {"start": v(-65, 236.5) * mm, "end": v(-65, 246.5) * mm});
            skLineSegment(sketch, "E5.6.10.1", {"start": v(-55, 236.5) * mm, "end": v(-55, 246.5) * mm});
            skLineSegment(sketch, "E5.6.10.2", {"start": v(-65, 236.5) * mm, "end": v(-55, 236.5) * mm});
            skLineSegment(sketch, "E5.6.10.3", {"start": v(-65, 246.5) * mm, "end": v(-55, 246.5) * mm});
            skLineSegment(sketch, "E5.6.11.0", {"start": v(-65, 221.5) * mm, "end": v(-65, 231.5) * mm});
            skLineSegment(sketch, "E5.6.11.1", {"start": v(-55, 221.5) * mm, "end": v(-55, 231.5) * mm});
            skLineSegment(sketch, "E5.6.11.2", {"start": v(-65, 221.5) * mm, "end": v(-55, 221.5) * mm});
            skLineSegment(sketch, "E5.6.11.3", {"start": v(-65, 231.5) * mm, "end": v(-55, 231.5) * mm});
            skLineSegment(sketch, "E5.6.12.0", {"start": v(-65, 206.5) * mm, "end": v(-65, 216.5) * mm});
            skLineSegment(sketch, "E5.6.12.1", {"start": v(-55, 206.5) * mm, "end": v(-55, 216.5) * mm});
            skLineSegment(sketch, "E5.6.12.2", {"start": v(-65, 206.5) * mm, "end": v(-55, 206.5) * mm});
            skLineSegment(sketch, "E5.6.12.3", {"start": v(-65, 216.5) * mm, "end": v(-55, 216.5) * mm});
            skLineSegment(sketch, "E5.6.13.0", {"start": v(-65, 191.5) * mm, "end": v(-65, 201.5) * mm});
            skLineSegment(sketch, "E5.6.13.1", {"start": v(-55, 191.5) * mm, "end": v(-55, 201.5) * mm});
            skLineSegment(sketch, "E5.6.13.2", {"start": v(-65, 191.5) * mm, "end": v(-55, 191.5) * mm});
            skLineSegment(sketch, "E5.6.13.3", {"start": v(-65, 201.5) * mm, "end": v(-55, 201.5) * mm});
            skLineSegment(sketch, "E5.6.14.0", {"start": v(-65, 176.5) * mm, "end": v(-65, 186.5) * mm});
            skLineSegment(sketch, "E5.6.14.1", {"start": v(-55, 176.5) * mm, "end": v(-55, 186.5) * mm});
            skLineSegment(sketch, "E5.6.14.2", {"start": v(-65, 176.5) * mm, "end": v(-55, 176.5) * mm});
            skLineSegment(sketch, "E5.6.14.3", {"start": v(-65, 186.5) * mm, "end": v(-55, 186.5) * mm});
            skLineSegment(sketch, "E5.6.15.0", {"start": v(-65, 161.5) * mm, "end": v(-65, 171.5) * mm});
            skLineSegment(sketch, "E5.6.15.1", {"start": v(-55, 161.5) * mm, "end": v(-55, 171.5) * mm});
            skLineSegment(sketch, "E5.6.15.2", {"start": v(-65, 161.5) * mm, "end": v(-55, 161.5) * mm});
            skLineSegment(sketch, "E5.6.15.3", {"start": v(-65, 171.5) * mm, "end": v(-55, 171.5) * mm});
            skLineSegment(sketch, "E5.6.16.0", {"start": v(-65, 146.5) * mm, "end": v(-65, 156.5) * mm});
            skLineSegment(sketch, "E5.6.16.1", {"start": v(-55, 146.5) * mm, "end": v(-55, 156.5) * mm});
            skLineSegment(sketch, "E5.6.16.2", {"start": v(-65, 146.5) * mm, "end": v(-55, 146.5) * mm});
            skLineSegment(sketch, "E5.6.16.3", {"start": v(-65, 156.5) * mm, "end": v(-55, 156.5) * mm});
            skLineSegment(sketch, "E5.6.17.0", {"start": v(-65, 131.5) * mm, "end": v(-65, 141.5) * mm});
            skLineSegment(sketch, "E5.6.17.1", {"start": v(-55, 131.5) * mm, "end": v(-55, 141.5) * mm});
            skLineSegment(sketch, "E5.6.17.2", {"start": v(-65, 131.5) * mm, "end": v(-55, 131.5) * mm});
            skLineSegment(sketch, "E5.6.17.3", {"start": v(-65, 141.5) * mm, "end": v(-55, 141.5) * mm});
            skLineSegment(sketch, "E5.6.18.0", {"start": v(-65, 116.5) * mm, "end": v(-65, 126.5) * mm});
            skLineSegment(sketch, "E5.6.18.1", {"start": v(-55, 116.5) * mm, "end": v(-55, 126.5) * mm});
            skLineSegment(sketch, "E5.6.18.2", {"start": v(-65, 116.5) * mm, "end": v(-55, 116.5) * mm});
            skLineSegment(sketch, "E5.6.18.3", {"start": v(-65, 126.5) * mm, "end": v(-55, 126.5) * mm});
            skLineSegment(sketch, "E5.6.19.0", {"start": v(-65, 101.5) * mm, "end": v(-65, 111.5) * mm});
            skLineSegment(sketch, "E5.6.19.1", {"start": v(-55, 101.5) * mm, "end": v(-55, 111.5) * mm});
            skLineSegment(sketch, "E5.6.19.2", {"start": v(-65, 101.5) * mm, "end": v(-55, 101.5) * mm});
            skLineSegment(sketch, "E5.6.19.3", {"start": v(-65, 111.5) * mm, "end": v(-55, 111.5) * mm});
            skLineSegment(sketch, "E5.6.20.0", {"start": v(-65, 86.5) * mm, "end": v(-65, 96.5) * mm});
            skLineSegment(sketch, "E5.6.20.1", {"start": v(-55, 86.5) * mm, "end": v(-55, 96.5) * mm});
            skLineSegment(sketch, "E5.6.20.2", {"start": v(-65, 86.5) * mm, "end": v(-55, 86.5) * mm});
            skLineSegment(sketch, "E5.6.20.3", {"start": v(-65, 96.5) * mm, "end": v(-55, 96.5) * mm});
            skLineSegment(sketch, "E5.6.21.0", {"start": v(-65, 71.5) * mm, "end": v(-65, 81.5) * mm});
            skLineSegment(sketch, "E5.6.21.1", {"start": v(-55, 71.5) * mm, "end": v(-55, 81.5) * mm});
            skLineSegment(sketch, "E5.6.21.2", {"start": v(-65, 71.5) * mm, "end": v(-55, 71.5) * mm});
            skLineSegment(sketch, "E5.6.21.3", {"start": v(-65, 81.5) * mm, "end": v(-55, 81.5) * mm});
            skLineSegment(sketch, "E5.6.22.0", {"start": v(-65, 56.5) * mm, "end": v(-65, 66.5) * mm});
            skLineSegment(sketch, "E5.6.22.1", {"start": v(-55, 56.5) * mm, "end": v(-55, 66.5) * mm});
            skLineSegment(sketch, "E5.6.22.2", {"start": v(-65, 56.5) * mm, "end": v(-55, 56.5) * mm});
            skLineSegment(sketch, "E5.6.22.3", {"start": v(-65, 66.5) * mm, "end": v(-55, 66.5) * mm});
            skLineSegment(sketch, "E5.6.23.0", {"start": v(-65, 41.5) * mm, "end": v(-65, 51.5) * mm});
            skLineSegment(sketch, "E5.6.23.1", {"start": v(-55, 41.5) * mm, "end": v(-55, 51.5) * mm});
            skLineSegment(sketch, "E5.6.23.2", {"start": v(-65, 41.5) * mm, "end": v(-55, 41.5) * mm});
            skLineSegment(sketch, "E5.6.23.3", {"start": v(-65, 51.5) * mm, "end": v(-55, 51.5) * mm});
            skLineSegment(sketch, "E5.6.24.0", {"start": v(-65, 26.5) * mm, "end": v(-65, 36.5) * mm});
            skLineSegment(sketch, "E5.6.24.1", {"start": v(-55, 26.5) * mm, "end": v(-55, 36.5) * mm});
            skLineSegment(sketch, "E5.6.24.2", {"start": v(-65, 26.5) * mm, "end": v(-55, 26.5) * mm});
            skLineSegment(sketch, "E5.6.24.3", {"start": v(-65, 36.5) * mm, "end": v(-55, 36.5) * mm});
            skLineSegment(sketch, "E5.7.0.0", {"start": v(-50, 386.5) * mm, "end": v(-50, 396.5) * mm});
            skLineSegment(sketch, "E5.7.0.1", {"start": v(-40, 386.5) * mm, "end": v(-40, 396.5) * mm});
            skLineSegment(sketch, "E5.7.0.2", {"start": v(-50, 386.5) * mm, "end": v(-40, 386.5) * mm});
            skLineSegment(sketch, "E5.7.0.3", {"start": v(-50, 396.5) * mm, "end": v(-40, 396.5) * mm});
            skLineSegment(sketch, "E5.7.1.0", {"start": v(-50, 371.5) * mm, "end": v(-50, 381.5) * mm});
            skLineSegment(sketch, "E5.7.1.1", {"start": v(-40, 371.5) * mm, "end": v(-40, 381.5) * mm});
            skLineSegment(sketch, "E5.7.1.2", {"start": v(-50, 371.5) * mm, "end": v(-40, 371.5) * mm});
            skLineSegment(sketch, "E5.7.1.3", {"start": v(-50, 381.5) * mm, "end": v(-40, 381.5) * mm});
            skLineSegment(sketch, "E5.7.2.0", {"start": v(-50, 356.5) * mm, "end": v(-50, 366.5) * mm});
            skLineSegment(sketch, "E5.7.2.1", {"start": v(-40, 356.5) * mm, "end": v(-40, 366.5) * mm});
            skLineSegment(sketch, "E5.7.2.2", {"start": v(-50, 356.5) * mm, "end": v(-40, 356.5) * mm});
            skLineSegment(sketch, "E5.7.2.3", {"start": v(-50, 366.5) * mm, "end": v(-40, 366.5) * mm});
            skLineSegment(sketch, "E5.7.3.0", {"start": v(-50, 341.5) * mm, "end": v(-50, 351.5) * mm});
            skLineSegment(sketch, "E5.7.3.1", {"start": v(-40, 341.5) * mm, "end": v(-40, 351.5) * mm});
            skLineSegment(sketch, "E5.7.3.2", {"start": v(-50, 341.5) * mm, "end": v(-40, 341.5) * mm});
            skLineSegment(sketch, "E5.7.3.3", {"start": v(-50, 351.5) * mm, "end": v(-40, 351.5) * mm});
            skLineSegment(sketch, "E5.7.4.0", {"start": v(-50, 326.5) * mm, "end": v(-50, 336.5) * mm});
            skLineSegment(sketch, "E5.7.4.1", {"start": v(-40, 326.5) * mm, "end": v(-40, 336.5) * mm});
            skLineSegment(sketch, "E5.7.4.2", {"start": v(-50, 326.5) * mm, "end": v(-40, 326.5) * mm});
            skLineSegment(sketch, "E5.7.4.3", {"start": v(-50, 336.5) * mm, "end": v(-40, 336.5) * mm});
            skLineSegment(sketch, "E5.7.5.0", {"start": v(-50, 311.5) * mm, "end": v(-50, 321.5) * mm});
            skLineSegment(sketch, "E5.7.5.1", {"start": v(-40, 311.5) * mm, "end": v(-40, 321.5) * mm});
            skLineSegment(sketch, "E5.7.5.2", {"start": v(-50, 311.5) * mm, "end": v(-40, 311.5) * mm});
            skLineSegment(sketch, "E5.7.5.3", {"start": v(-50, 321.5) * mm, "end": v(-40, 321.5) * mm});
            skLineSegment(sketch, "E5.7.6.0", {"start": v(-50, 296.5) * mm, "end": v(-50, 306.5) * mm});
            skLineSegment(sketch, "E5.7.6.1", {"start": v(-40, 296.5) * mm, "end": v(-40, 306.5) * mm});
            skLineSegment(sketch, "E5.7.6.2", {"start": v(-50, 296.5) * mm, "end": v(-40, 296.5) * mm});
            skLineSegment(sketch, "E5.7.6.3", {"start": v(-50, 306.5) * mm, "end": v(-40, 306.5) * mm});
            skLineSegment(sketch, "E5.7.7.0", {"start": v(-50, 281.5) * mm, "end": v(-50, 291.5) * mm});
            skLineSegment(sketch, "E5.7.7.1", {"start": v(-40, 281.5) * mm, "end": v(-40, 291.5) * mm});
            skLineSegment(sketch, "E5.7.7.2", {"start": v(-50, 281.5) * mm, "end": v(-40, 281.5) * mm});
            skLineSegment(sketch, "E5.7.7.3", {"start": v(-50, 291.5) * mm, "end": v(-40, 291.5) * mm});
            skLineSegment(sketch, "E5.7.8.0", {"start": v(-50, 266.5) * mm, "end": v(-50, 276.5) * mm});
            skLineSegment(sketch, "E5.7.8.1", {"start": v(-40, 266.5) * mm, "end": v(-40, 276.5) * mm});
            skLineSegment(sketch, "E5.7.8.2", {"start": v(-50, 266.5) * mm, "end": v(-40, 266.5) * mm});
            skLineSegment(sketch, "E5.7.8.3", {"start": v(-50, 276.5) * mm, "end": v(-40, 276.5) * mm});
            skLineSegment(sketch, "E5.7.9.0", {"start": v(-50, 251.5) * mm, "end": v(-50, 261.5) * mm});
            skLineSegment(sketch, "E5.7.9.1", {"start": v(-40, 251.5) * mm, "end": v(-40, 261.5) * mm});
            skLineSegment(sketch, "E5.7.9.2", {"start": v(-50, 251.5) * mm, "end": v(-40, 251.5) * mm});
            skLineSegment(sketch, "E5.7.9.3", {"start": v(-50, 261.5) * mm, "end": v(-40, 261.5) * mm});
            skLineSegment(sketch, "E5.7.10.0", {"start": v(-50, 236.5) * mm, "end": v(-50, 246.5) * mm});
            skLineSegment(sketch, "E5.7.10.1", {"start": v(-40, 236.5) * mm, "end": v(-40, 246.5) * mm});
            skLineSegment(sketch, "E5.7.10.2", {"start": v(-50, 236.5) * mm, "end": v(-40, 236.5) * mm});
            skLineSegment(sketch, "E5.7.10.3", {"start": v(-50, 246.5) * mm, "end": v(-40, 246.5) * mm});
            skLineSegment(sketch, "E5.7.11.0", {"start": v(-50, 221.5) * mm, "end": v(-50, 231.5) * mm});
            skLineSegment(sketch, "E5.7.11.1", {"start": v(-40, 221.5) * mm, "end": v(-40, 231.5) * mm});
            skLineSegment(sketch, "E5.7.11.2", {"start": v(-50, 221.5) * mm, "end": v(-40, 221.5) * mm});
            skLineSegment(sketch, "E5.7.11.3", {"start": v(-50, 231.5) * mm, "end": v(-40, 231.5) * mm});
            skLineSegment(sketch, "E5.7.12.0", {"start": v(-50, 206.5) * mm, "end": v(-50, 216.5) * mm});
            skLineSegment(sketch, "E5.7.12.1", {"start": v(-40, 206.5) * mm, "end": v(-40, 216.5) * mm});
            skLineSegment(sketch, "E5.7.12.2", {"start": v(-50, 206.5) * mm, "end": v(-40, 206.5) * mm});
            skLineSegment(sketch, "E5.7.12.3", {"start": v(-50, 216.5) * mm, "end": v(-40, 216.5) * mm});
            skLineSegment(sketch, "E5.7.13.0", {"start": v(-50, 191.5) * mm, "end": v(-50, 201.5) * mm});
            skLineSegment(sketch, "E5.7.13.1", {"start": v(-40, 191.5) * mm, "end": v(-40, 201.5) * mm});
            skLineSegment(sketch, "E5.7.13.2", {"start": v(-50, 191.5) * mm, "end": v(-40, 191.5) * mm});
            skLineSegment(sketch, "E5.7.13.3", {"start": v(-50, 201.5) * mm, "end": v(-40, 201.5) * mm});
            skLineSegment(sketch, "E5.7.14.0", {"start": v(-50, 176.5) * mm, "end": v(-50, 186.5) * mm});
            skLineSegment(sketch, "E5.7.14.1", {"start": v(-40, 176.5) * mm, "end": v(-40, 186.5) * mm});
            skLineSegment(sketch, "E5.7.14.2", {"start": v(-50, 176.5) * mm, "end": v(-40, 176.5) * mm});
            skLineSegment(sketch, "E5.7.14.3", {"start": v(-50, 186.5) * mm, "end": v(-40, 186.5) * mm});
            skLineSegment(sketch, "E5.7.15.0", {"start": v(-50, 161.5) * mm, "end": v(-50, 171.5) * mm});
            skLineSegment(sketch, "E5.7.15.1", {"start": v(-40, 161.5) * mm, "end": v(-40, 171.5) * mm});
            skLineSegment(sketch, "E5.7.15.2", {"start": v(-50, 161.5) * mm, "end": v(-40, 161.5) * mm});
            skLineSegment(sketch, "E5.7.15.3", {"start": v(-50, 171.5) * mm, "end": v(-40, 171.5) * mm});
            skLineSegment(sketch, "E5.7.16.0", {"start": v(-50, 146.5) * mm, "end": v(-50, 156.5) * mm});
            skLineSegment(sketch, "E5.7.16.1", {"start": v(-40, 146.5) * mm, "end": v(-40, 156.5) * mm});
            skLineSegment(sketch, "E5.7.16.2", {"start": v(-50, 146.5) * mm, "end": v(-40, 146.5) * mm});
            skLineSegment(sketch, "E5.7.16.3", {"start": v(-50, 156.5) * mm, "end": v(-40, 156.5) * mm});
            skLineSegment(sketch, "E5.7.17.0", {"start": v(-50, 131.5) * mm, "end": v(-50, 141.5) * mm});
            skLineSegment(sketch, "E5.7.17.1", {"start": v(-40, 131.5) * mm, "end": v(-40, 141.5) * mm});
            skLineSegment(sketch, "E5.7.17.2", {"start": v(-50, 131.5) * mm, "end": v(-40, 131.5) * mm});
            skLineSegment(sketch, "E5.7.17.3", {"start": v(-50, 141.5) * mm, "end": v(-40, 141.5) * mm});
            skLineSegment(sketch, "E5.7.18.0", {"start": v(-50, 116.5) * mm, "end": v(-50, 126.5) * mm});
            skLineSegment(sketch, "E5.7.18.1", {"start": v(-40, 116.5) * mm, "end": v(-40, 126.5) * mm});
            skLineSegment(sketch, "E5.7.18.2", {"start": v(-50, 116.5) * mm, "end": v(-40, 116.5) * mm});
            skLineSegment(sketch, "E5.7.18.3", {"start": v(-50, 126.5) * mm, "end": v(-40, 126.5) * mm});
            skLineSegment(sketch, "E5.7.19.0", {"start": v(-50, 101.5) * mm, "end": v(-50, 111.5) * mm});
            skLineSegment(sketch, "E5.7.19.1", {"start": v(-40, 101.5) * mm, "end": v(-40, 111.5) * mm});
            skLineSegment(sketch, "E5.7.19.2", {"start": v(-50, 101.5) * mm, "end": v(-40, 101.5) * mm});
            skLineSegment(sketch, "E5.7.19.3", {"start": v(-50, 111.5) * mm, "end": v(-40, 111.5) * mm});
            skLineSegment(sketch, "E5.7.20.0", {"start": v(-50, 86.5) * mm, "end": v(-50, 96.5) * mm});
            skLineSegment(sketch, "E5.7.20.1", {"start": v(-40, 86.5) * mm, "end": v(-40, 96.5) * mm});
            skLineSegment(sketch, "E5.7.20.2", {"start": v(-50, 86.5) * mm, "end": v(-40, 86.5) * mm});
            skLineSegment(sketch, "E5.7.20.3", {"start": v(-50, 96.5) * mm, "end": v(-40, 96.5) * mm});
            skLineSegment(sketch, "E5.7.21.0", {"start": v(-50, 71.5) * mm, "end": v(-50, 81.5) * mm});
            skLineSegment(sketch, "E5.7.21.1", {"start": v(-40, 71.5) * mm, "end": v(-40, 81.5) * mm});
            skLineSegment(sketch, "E5.7.21.2", {"start": v(-50, 71.5) * mm, "end": v(-40, 71.5) * mm});
            skLineSegment(sketch, "E5.7.21.3", {"start": v(-50, 81.5) * mm, "end": v(-40, 81.5) * mm});
            skLineSegment(sketch, "E5.7.22.0", {"start": v(-50, 56.5) * mm, "end": v(-50, 66.5) * mm});
            skLineSegment(sketch, "E5.7.22.1", {"start": v(-40, 56.5) * mm, "end": v(-40, 66.5) * mm});
            skLineSegment(sketch, "E5.7.22.2", {"start": v(-50, 56.5) * mm, "end": v(-40, 56.5) * mm});
            skLineSegment(sketch, "E5.7.22.3", {"start": v(-50, 66.5) * mm, "end": v(-40, 66.5) * mm});
            skLineSegment(sketch, "E5.7.23.0", {"start": v(-50, 41.5) * mm, "end": v(-50, 51.5) * mm});
            skLineSegment(sketch, "E5.7.23.1", {"start": v(-40, 41.5) * mm, "end": v(-40, 51.5) * mm});
            skLineSegment(sketch, "E5.7.23.2", {"start": v(-50, 41.5) * mm, "end": v(-40, 41.5) * mm});
            skLineSegment(sketch, "E5.7.23.3", {"start": v(-50, 51.5) * mm, "end": v(-40, 51.5) * mm});
            skLineSegment(sketch, "E5.7.24.0", {"start": v(-50, 26.5) * mm, "end": v(-50, 36.5) * mm});
            skLineSegment(sketch, "E5.7.24.1", {"start": v(-40, 26.5) * mm, "end": v(-40, 36.5) * mm});
            skLineSegment(sketch, "E5.7.24.2", {"start": v(-50, 26.5) * mm, "end": v(-40, 26.5) * mm});
            skLineSegment(sketch, "E5.7.24.3", {"start": v(-50, 36.5) * mm, "end": v(-40, 36.5) * mm});
            skLineSegment(sketch, "E5.8.0.0", {"start": v(-35, 386.5) * mm, "end": v(-35, 396.5) * mm});
            skLineSegment(sketch, "E5.8.0.1", {"start": v(-25, 386.5) * mm, "end": v(-25, 396.5) * mm});
            skLineSegment(sketch, "E5.8.0.2", {"start": v(-35, 386.5) * mm, "end": v(-25, 386.5) * mm});
            skLineSegment(sketch, "E5.8.0.3", {"start": v(-35, 396.5) * mm, "end": v(-25, 396.5) * mm});
            skLineSegment(sketch, "E5.8.1.0", {"start": v(-35, 371.5) * mm, "end": v(-35, 381.5) * mm});
            skLineSegment(sketch, "E5.8.1.1", {"start": v(-25, 371.5) * mm, "end": v(-25, 381.5) * mm});
            skLineSegment(sketch, "E5.8.1.2", {"start": v(-35, 371.5) * mm, "end": v(-25, 371.5) * mm});
            skLineSegment(sketch, "E5.8.1.3", {"start": v(-35, 381.5) * mm, "end": v(-25, 381.5) * mm});
            skLineSegment(sketch, "E5.8.2.0", {"start": v(-35, 356.5) * mm, "end": v(-35, 366.5) * mm});
            skLineSegment(sketch, "E5.8.2.1", {"start": v(-25, 356.5) * mm, "end": v(-25, 366.5) * mm});
            skLineSegment(sketch, "E5.8.2.2", {"start": v(-35, 356.5) * mm, "end": v(-25, 356.5) * mm});
            skLineSegment(sketch, "E5.8.2.3", {"start": v(-35, 366.5) * mm, "end": v(-25, 366.5) * mm});
            skLineSegment(sketch, "E5.8.3.0", {"start": v(-35, 341.5) * mm, "end": v(-35, 351.5) * mm});
            skLineSegment(sketch, "E5.8.3.1", {"start": v(-25, 341.5) * mm, "end": v(-25, 351.5) * mm});
            skLineSegment(sketch, "E5.8.3.2", {"start": v(-35, 341.5) * mm, "end": v(-25, 341.5) * mm});
            skLineSegment(sketch, "E5.8.3.3", {"start": v(-35, 351.5) * mm, "end": v(-25, 351.5) * mm});
            skLineSegment(sketch, "E5.8.4.0", {"start": v(-35, 326.5) * mm, "end": v(-35, 336.5) * mm});
            skLineSegment(sketch, "E5.8.4.1", {"start": v(-25, 326.5) * mm, "end": v(-25, 336.5) * mm});
            skLineSegment(sketch, "E5.8.4.2", {"start": v(-35, 326.5) * mm, "end": v(-25, 326.5) * mm});
            skLineSegment(sketch, "E5.8.4.3", {"start": v(-35, 336.5) * mm, "end": v(-25, 336.5) * mm});
            skLineSegment(sketch, "E5.8.5.0", {"start": v(-35, 311.5) * mm, "end": v(-35, 321.5) * mm});
            skLineSegment(sketch, "E5.8.5.1", {"start": v(-25, 311.5) * mm, "end": v(-25, 321.5) * mm});
            skLineSegment(sketch, "E5.8.5.2", {"start": v(-35, 311.5) * mm, "end": v(-25, 311.5) * mm});
            skLineSegment(sketch, "E5.8.5.3", {"start": v(-35, 321.5) * mm, "end": v(-25, 321.5) * mm});
            skLineSegment(sketch, "E5.8.6.0", {"start": v(-35, 296.5) * mm, "end": v(-35, 306.5) * mm});
            skLineSegment(sketch, "E5.8.6.1", {"start": v(-25, 296.5) * mm, "end": v(-25, 306.5) * mm});
            skLineSegment(sketch, "E5.8.6.2", {"start": v(-35, 296.5) * mm, "end": v(-25, 296.5) * mm});
            skLineSegment(sketch, "E5.8.6.3", {"start": v(-35, 306.5) * mm, "end": v(-25, 306.5) * mm});
            skLineSegment(sketch, "E5.8.7.0", {"start": v(-35, 281.5) * mm, "end": v(-35, 291.5) * mm});
            skLineSegment(sketch, "E5.8.7.1", {"start": v(-25, 281.5) * mm, "end": v(-25, 291.5) * mm});
            skLineSegment(sketch, "E5.8.7.2", {"start": v(-35, 281.5) * mm, "end": v(-25, 281.5) * mm});
            skLineSegment(sketch, "E5.8.7.3", {"start": v(-35, 291.5) * mm, "end": v(-25, 291.5) * mm});
            skLineSegment(sketch, "E5.8.8.0", {"start": v(-35, 266.5) * mm, "end": v(-35, 276.5) * mm});
            skLineSegment(sketch, "E5.8.8.1", {"start": v(-25, 266.5) * mm, "end": v(-25, 276.5) * mm});
            skLineSegment(sketch, "E5.8.8.2", {"start": v(-35, 266.5) * mm, "end": v(-25, 266.5) * mm});
            skLineSegment(sketch, "E5.8.8.3", {"start": v(-35, 276.5) * mm, "end": v(-25, 276.5) * mm});
            skLineSegment(sketch, "E5.8.9.0", {"start": v(-35, 251.5) * mm, "end": v(-35, 261.5) * mm});
            skLineSegment(sketch, "E5.8.9.1", {"start": v(-25, 251.5) * mm, "end": v(-25, 261.5) * mm});
            skLineSegment(sketch, "E5.8.9.2", {"start": v(-35, 251.5) * mm, "end": v(-25, 251.5) * mm});
            skLineSegment(sketch, "E5.8.9.3", {"start": v(-35, 261.5) * mm, "end": v(-25, 261.5) * mm});
            skLineSegment(sketch, "E5.8.10.0", {"start": v(-35, 236.5) * mm, "end": v(-35, 246.5) * mm});
            skLineSegment(sketch, "E5.8.10.1", {"start": v(-25, 236.5) * mm, "end": v(-25, 246.5) * mm});
            skLineSegment(sketch, "E5.8.10.2", {"start": v(-35, 236.5) * mm, "end": v(-25, 236.5) * mm});
            skLineSegment(sketch, "E5.8.10.3", {"start": v(-35, 246.5) * mm, "end": v(-25, 246.5) * mm});
            skLineSegment(sketch, "E5.8.11.0", {"start": v(-35, 221.5) * mm, "end": v(-35, 231.5) * mm});
            skLineSegment(sketch, "E5.8.11.1", {"start": v(-25, 221.5) * mm, "end": v(-25, 231.5) * mm});
            skLineSegment(sketch, "E5.8.11.2", {"start": v(-35, 221.5) * mm, "end": v(-25, 221.5) * mm});
            skLineSegment(sketch, "E5.8.11.3", {"start": v(-35, 231.5) * mm, "end": v(-25, 231.5) * mm});
            skLineSegment(sketch, "E5.8.12.0", {"start": v(-35, 206.5) * mm, "end": v(-35, 216.5) * mm});
            skLineSegment(sketch, "E5.8.12.1", {"start": v(-25, 206.5) * mm, "end": v(-25, 216.5) * mm});
            skLineSegment(sketch, "E5.8.12.2", {"start": v(-35, 206.5) * mm, "end": v(-25, 206.5) * mm});
            skLineSegment(sketch, "E5.8.12.3", {"start": v(-35, 216.5) * mm, "end": v(-25, 216.5) * mm});
            skLineSegment(sketch, "E5.8.13.0", {"start": v(-35, 191.5) * mm, "end": v(-35, 201.5) * mm});
            skLineSegment(sketch, "E5.8.13.1", {"start": v(-25, 191.5) * mm, "end": v(-25, 201.5) * mm});
            skLineSegment(sketch, "E5.8.13.2", {"start": v(-35, 191.5) * mm, "end": v(-25, 191.5) * mm});
            skLineSegment(sketch, "E5.8.13.3", {"start": v(-35, 201.5) * mm, "end": v(-25, 201.5) * mm});
            skLineSegment(sketch, "E5.8.14.0", {"start": v(-35, 176.5) * mm, "end": v(-35, 186.5) * mm});
            skLineSegment(sketch, "E5.8.14.1", {"start": v(-25, 176.5) * mm, "end": v(-25, 186.5) * mm});
            skLineSegment(sketch, "E5.8.14.2", {"start": v(-35, 176.5) * mm, "end": v(-25, 176.5) * mm});
            skLineSegment(sketch, "E5.8.14.3", {"start": v(-35, 186.5) * mm, "end": v(-25, 186.5) * mm});
            skLineSegment(sketch, "E5.8.15.0", {"start": v(-35, 161.5) * mm, "end": v(-35, 171.5) * mm});
            skLineSegment(sketch, "E5.8.15.1", {"start": v(-25, 161.5) * mm, "end": v(-25, 171.5) * mm});
            skLineSegment(sketch, "E5.8.15.2", {"start": v(-35, 161.5) * mm, "end": v(-25, 161.5) * mm});
            skLineSegment(sketch, "E5.8.15.3", {"start": v(-35, 171.5) * mm, "end": v(-25, 171.5) * mm});
            skLineSegment(sketch, "E5.8.16.0", {"start": v(-35, 146.5) * mm, "end": v(-35, 156.5) * mm});
            skLineSegment(sketch, "E5.8.16.1", {"start": v(-25, 146.5) * mm, "end": v(-25, 156.5) * mm});
            skLineSegment(sketch, "E5.8.16.2", {"start": v(-35, 146.5) * mm, "end": v(-25, 146.5) * mm});
            skLineSegment(sketch, "E5.8.16.3", {"start": v(-35, 156.5) * mm, "end": v(-25, 156.5) * mm});
            skLineSegment(sketch, "E5.8.17.0", {"start": v(-35, 131.5) * mm, "end": v(-35, 141.5) * mm});
            skLineSegment(sketch, "E5.8.17.1", {"start": v(-25, 131.5) * mm, "end": v(-25, 141.5) * mm});
            skLineSegment(sketch, "E5.8.17.2", {"start": v(-35, 131.5) * mm, "end": v(-25, 131.5) * mm});
            skLineSegment(sketch, "E5.8.17.3", {"start": v(-35, 141.5) * mm, "end": v(-25, 141.5) * mm});
            skLineSegment(sketch, "E5.8.18.0", {"start": v(-35, 116.5) * mm, "end": v(-35, 126.5) * mm});
            skLineSegment(sketch, "E5.8.18.1", {"start": v(-25, 116.5) * mm, "end": v(-25, 126.5) * mm});
            skLineSegment(sketch, "E5.8.18.2", {"start": v(-35, 116.5) * mm, "end": v(-25, 116.5) * mm});
            skLineSegment(sketch, "E5.8.18.3", {"start": v(-35, 126.5) * mm, "end": v(-25, 126.5) * mm});
            skLineSegment(sketch, "E5.8.19.0", {"start": v(-35, 101.5) * mm, "end": v(-35, 111.5) * mm});
            skLineSegment(sketch, "E5.8.19.1", {"start": v(-25, 101.5) * mm, "end": v(-25, 111.5) * mm});
            skLineSegment(sketch, "E5.8.19.2", {"start": v(-35, 101.5) * mm, "end": v(-25, 101.5) * mm});
            skLineSegment(sketch, "E5.8.19.3", {"start": v(-35, 111.5) * mm, "end": v(-25, 111.5) * mm});
            skLineSegment(sketch, "E5.8.20.0", {"start": v(-35, 86.5) * mm, "end": v(-35, 96.5) * mm});
            skLineSegment(sketch, "E5.8.20.1", {"start": v(-25, 86.5) * mm, "end": v(-25, 96.5) * mm});
            skLineSegment(sketch, "E5.8.20.2", {"start": v(-35, 86.5) * mm, "end": v(-25, 86.5) * mm});
            skLineSegment(sketch, "E5.8.20.3", {"start": v(-35, 96.5) * mm, "end": v(-25, 96.5) * mm});
            skLineSegment(sketch, "E5.8.21.0", {"start": v(-35, 71.5) * mm, "end": v(-35, 81.5) * mm});
            skLineSegment(sketch, "E5.8.21.1", {"start": v(-25, 71.5) * mm, "end": v(-25, 81.5) * mm});
            skLineSegment(sketch, "E5.8.21.2", {"start": v(-35, 71.5) * mm, "end": v(-25, 71.5) * mm});
            skLineSegment(sketch, "E5.8.21.3", {"start": v(-35, 81.5) * mm, "end": v(-25, 81.5) * mm});
            skLineSegment(sketch, "E5.8.22.0", {"start": v(-35, 56.5) * mm, "end": v(-35, 66.5) * mm});
            skLineSegment(sketch, "E5.8.22.1", {"start": v(-25, 56.5) * mm, "end": v(-25, 66.5) * mm});
            skLineSegment(sketch, "E5.8.22.2", {"start": v(-35, 56.5) * mm, "end": v(-25, 56.5) * mm});
            skLineSegment(sketch, "E5.8.22.3", {"start": v(-35, 66.5) * mm, "end": v(-25, 66.5) * mm});
            skLineSegment(sketch, "E5.8.23.0", {"start": v(-35, 41.5) * mm, "end": v(-35, 51.5) * mm});
            skLineSegment(sketch, "E5.8.23.1", {"start": v(-25, 41.5) * mm, "end": v(-25, 51.5) * mm});
            skLineSegment(sketch, "E5.8.23.2", {"start": v(-35, 41.5) * mm, "end": v(-25, 41.5) * mm});
            skLineSegment(sketch, "E5.8.23.3", {"start": v(-35, 51.5) * mm, "end": v(-25, 51.5) * mm});
            skLineSegment(sketch, "E5.8.24.0", {"start": v(-35, 26.5) * mm, "end": v(-35, 36.5) * mm});
            skLineSegment(sketch, "E5.8.24.1", {"start": v(-25, 26.5) * mm, "end": v(-25, 36.5) * mm});
            skLineSegment(sketch, "E5.8.24.2", {"start": v(-35, 26.5) * mm, "end": v(-25, 26.5) * mm});
            skLineSegment(sketch, "E5.8.24.3", {"start": v(-35, 36.5) * mm, "end": v(-25, 36.5) * mm});
            skLineSegment(sketch, "E5.direction1", {"start": v(-157, 385) * mm, "end": v(-142, 385) * mm, "construction": true});
            skLineSegment(sketch, "E5.direction2", {"start": v(-157, 385) * mm, "end": v(-157, 370) * mm, "construction": true});
            skPoint(sketch, "E6.visualSharp", {"position": v(-145, 396.5) * mm});
            skArc(sketch, "E6.filletArc", {"start": v(-145, 395) * mm, "mid": v(-145.44, 396.06) * mm, "end": v(-146.5, 396.5) * mm});
            skPoint(sketch, "E7.visualSharp", {"position": v(-155, 396.5) * mm});
            skArc(sketch, "E7.filletArc", {"start": v(-153.5, 396.5) * mm, "mid": v(-154.56, 396.06) * mm, "end": v(-155, 395) * mm});
            skSolve(sketch);
        }
        {
            var Q0;
            Q0=makeQuery(id+"F0.imprint","IMPRINT",FACE,{"disambiguationData":[TD([[makeQuery(id+"F0.imprint","IMPRINT",EDGE,{"derivedFrom":sQuery(id+"F0.wireOp",EDGE,"E0.bottom")}),-1.0]])]});
            extrude(context, id + "F1", {"entities" : qUnion([Q0]), "depth" : 25 * mm});
        }
        {
            var Q0;
            Q0 = qSketchRegion(id + "F0", true);
            extrude(context, id + "F2", {"entities" : qUnion([Q0]), "operationType" : NewBodyOperationType.ADD, "depth" : 25 * mm});
        }
        {
            var Q0;
            Q0=qCreatedBy(makeId("Top.planeOp"),FACE);
            var sketch = newSketch(context, id + "F3", { "sketchPlane" : qUnion([Q0])});
            skLineSegment(sketch, "E8.bottom", {"start": v(0, 0) * mm, "end": v(-450, 0) * mm});
            skLineSegment(sketch, "E8.top", {"start": v(0, -470) * mm, "end": v(-450, -470) * mm});
            skLineSegment(sketch, "E8.left", {"start": v(0, 0) * mm, "end": v(0, -470) * mm});
            skLineSegment(sketch, "E8.right", {"start": v(-450, 0) * mm, "end": v(-450, -470) * mm});
            skLineSegment(sketch, "E9", {"start": v(-440, -10) * mm, "end": v(-440, -20.32) * mm});
            skPoint(sketch, "E10", {"position": v(-440, -10) * mm});
            skLineSegment(sketch, "E11", {"start": v(-10, -10) * mm, "end": v(-10, -60) * mm});
            skLineSegment(sketch, "E12", {"start": v(-14.47, -460) * mm, "end": v(-64.23, -460) * mm});
            skLineSegment(sketch, "E13", {"start": v(-60, -10) * mm, "end": v(-41.72, -28.28) * mm});
            skLineSegment(sketch, "E14", {"start": v(-74.14, -10) * mm, "end": v(-48.69, -35.46) * mm});
            skLineSegment(sketch, "E15", {"start": v(-125.05, -10) * mm, "end": v(-106.27, -28.78) * mm});
            skLineSegment(sketch, "E16", {"start": v(-139.2, -10) * mm, "end": v(-113.24, -35.95) * mm});
            skLineSegment(sketch, "E17", {"start": v(-190.1, -10) * mm, "end": v(-171.82, -28.29) * mm});
            skLineSegment(sketch, "E18", {"start": v(-204.25, -10) * mm, "end": v(-178.79, -35.46) * mm});
            skPoint(sketch, "E19.MirrorP", {"position": v(-440.22, -460.75) * mm});
            skLineSegment(sketch, "E20", {"start": v(-74.14, -10) * mm, "end": v(-99.6, -35.46) * mm});
            skLineSegment(sketch, "E21", {"start": v(-74.14, -60.91) * mm, "end": v(-48.69, -35.46) * mm});
            skLineSegment(sketch, "E22", {"start": v(-88.03, -10) * mm, "end": v(-106.27, -28.78) * mm});
            skLineSegment(sketch, "E23", {"start": v(-106.57, -42.63) * mm, "end": v(-131.66, -68.45) * mm});
            skLineSegment(sketch, "E24", {"start": v(-41.72, -28.28) * mm, "end": v(-23.95, -10) * mm});
            skLineSegment(sketch, "E25", {"start": v(-81.11, -68.08) * mm, "end": v(-106.2, -93.9) * mm});
            skLineSegment(sketch, "E26", {"start": v(-67.63, -67.43) * mm, "end": v(-42.54, -41.6) * mm});
            skLineSegment(sketch, "E27", {"start": v(-74.6, -74.6) * mm, "end": v(-99.69, -100.42) * mm});
            skLineSegment(sketch, "E28", {"start": v(-139.2, -10) * mm, "end": v(-164.29, -35.82) * mm});
            skLineSegment(sketch, "E29", {"start": v(-154.05, -10) * mm, "end": v(-171.82, -28.29) * mm});
            skLineSegment(sketch, "E30", {"start": v(-204.25, -10) * mm, "end": v(-229.34, -35.82) * mm});
            skLineSegment(sketch, "E31", {"start": v(-216.38, -10) * mm, "end": v(-235.5, -29.67) * mm});
            skLineSegment(sketch, "E32", {"start": v(-267.92, -11.38) * mm, "end": v(-293, -37.2) * mm});
            skLineSegment(sketch, "E33", {"start": v(-280.52, -10) * mm, "end": v(-300.08, -30.13) * mm});
            skLineSegment(sketch, "E34", {"start": v(-332.5, -11.85) * mm, "end": v(-357.6, -37.67) * mm});
            skLineSegment(sketch, "E35", {"start": v(-344.66, -10) * mm, "end": v(-364.67, -30.6) * mm});
            skLineSegment(sketch, "E36", {"start": v(-397.1, -12.31) * mm, "end": v(-422.19, -38.13) * mm});
            skLineSegment(sketch, "E37", {"start": v(-408.8, -10) * mm, "end": v(-429.26, -31.06) * mm});
            skLineSegment(sketch, "E38", {"start": v(-10, -59.77) * mm, "end": v(-10.11, -59.89) * mm});
            skLineSegment(sketch, "E39", {"start": v(-10, -74.14) * mm, "end": v(-35.09, -99.96) * mm});
            skLineSegment(sketch, "E40", {"start": v(-16.6, -132.6) * mm, "end": v(-41.7, -158.42) * mm});
            skLineSegment(sketch, "E41", {"start": v(-10, -140.15) * mm, "end": v(-34.62, -165.49) * mm});
            skLineSegment(sketch, "E42", {"start": v(-16.13, -198.12) * mm, "end": v(-41.22, -223.94) * mm});
            skLineSegment(sketch, "E43", {"start": v(-10, -206.16) * mm, "end": v(-34.15, -231.01) * mm});
            skLineSegment(sketch, "E44", {"start": v(-15.66, -263.65) * mm, "end": v(-40.75, -289.47) * mm});
            skLineSegment(sketch, "E45", {"start": v(-10, -272.17) * mm, "end": v(-33.68, -296.54) * mm});
            skLineSegment(sketch, "E46", {"start": v(-15.19, -329.17) * mm, "end": v(-40.28, -355) * mm});
            skLineSegment(sketch, "E47", {"start": v(-10, -338.18) * mm, "end": v(-33.2, -362.06) * mm});
            skLineSegment(sketch, "E48", {"start": v(-14.72, -394.7) * mm, "end": v(-39.8, -420.52) * mm});
            skLineSegment(sketch, "E49", {"start": v(-10, -404.2) * mm, "end": v(-32.73, -427.59) * mm});
            skLineSegment(sketch, "E50", {"start": v(-255.16, -10) * mm, "end": v(-235.5, -29.67) * mm});
            skLineSegment(sketch, "E51", {"start": v(-267.92, -11.38) * mm, "end": v(-242.46, -36.84) * mm});
            skLineSegment(sketch, "E52", {"start": v(-320.22, -10) * mm, "end": v(-300.08, -30.13) * mm});
            skLineSegment(sketch, "E53", {"start": v(-332.5, -11.85) * mm, "end": v(-307.05, -37.3) * mm});
            skLineSegment(sketch, "E54", {"start": v(-385.27, -10) * mm, "end": v(-364.67, -30.6) * mm});
            skLineSegment(sketch, "E55", {"start": v(-397.1, -12.31) * mm, "end": v(-371.64, -37.77) * mm});
            skLineSegment(sketch, "E56", {"start": v(-440, -20.32) * mm, "end": v(-429.26, -31.06) * mm});
            skLineSegment(sketch, "E57.trimOffspring", {"start": v(-440, -460.75) * mm, "end": v(-440.22, -460.75) * mm});
            skLineSegment(sketch, "E58", {"start": v(-191.53, -459) * mm, "end": v(-192.5, -460) * mm});
            skLineSegment(sketch, "E59", {"start": v(-126.95, -458.54) * mm, "end": v(-128.37, -460) * mm});
            skLineSegment(sketch, "E60", {"start": v(-62.36, -458.08) * mm, "end": v(-64.23, -460) * mm});
            skLineSegment(sketch, "E61", {"start": v(-440, -89.78) * mm, "end": v(-430.96, -98.82) * mm});
            skLineSegment(sketch, "E62", {"start": v(-430.86, -113.07) * mm, "end": v(-405.4, -138.52) * mm});
            skLineSegment(sketch, "E63", {"start": v(-440, -154.84) * mm, "end": v(-430.49, -164.35) * mm});
            skLineSegment(sketch, "E64", {"start": v(-440, -219.89) * mm, "end": v(-430.02, -229.87) * mm});
            skLineSegment(sketch, "E65", {"start": v(-440, -284.94) * mm, "end": v(-430.46, -294.48) * mm});
            skLineSegment(sketch, "E66", {"start": v(-440, -350) * mm, "end": v(-429.04, -360.96) * mm});
            skLineSegment(sketch, "E67", {"start": v(-440, -415.05) * mm, "end": v(-428.96, -426.09) * mm});
            skLineSegment(sketch, "E68", {"start": v(-429.42, -439.77) * mm, "end": v(-409.2, -460) * mm});
            skLineSegment(sketch, "E69.trimOffspring", {"start": v(-429.16, -45.3) * mm, "end": v(-403.7, -70.77) * mm});
            skLineSegment(sketch, "E70.trimOffspring", {"start": v(-422.19, -38.13) * mm, "end": v(-396.73, -63.6) * mm});
            skLineSegment(sketch, "E71.trimOffspring", {"start": v(-429.16, -45.3) * mm, "end": v(-440, -56.47) * mm});
            skLineSegment(sketch, "E72.trimOffspring", {"start": v(-403.7, -70.77) * mm, "end": v(-430.96, -98.82) * mm});
            skLineSegment(sketch, "E73.trimOffspring", {"start": v(-389.66, -70.66) * mm, "end": v(-364.2, -96.12) * mm});
            skLineSegment(sketch, "E74.trimOffspring", {"start": v(-396.63, -77.84) * mm, "end": v(-371.17, -103.3) * mm});
            skLineSegment(sketch, "E75.trimOffspring", {"start": v(-396.63, -77.84) * mm, "end": v(-423.89, -105.9) * mm});
            skLineSegment(sketch, "E76.trimOffspring", {"start": v(-371.64, -37.77) * mm, "end": v(-396.73, -63.6) * mm});
            skLineSegment(sketch, "E77.trimOffspring", {"start": v(-364.57, -44.84) * mm, "end": v(-339.11, -70.3) * mm});
            skLineSegment(sketch, "E78.trimOffspring", {"start": v(-357.6, -37.67) * mm, "end": v(-332.14, -63.13) * mm});
            skLineSegment(sketch, "E79.trimOffspring", {"start": v(-364.57, -44.84) * mm, "end": v(-389.66, -70.66) * mm});
            skLineSegment(sketch, "E80.trimOffspring", {"start": v(-344.66, -10) * mm, "end": v(-385.27, -10) * mm});
            skLineSegment(sketch, "E81.trimOffspring", {"start": v(-408.8, -10) * mm, "end": v(-440, -10) * mm});
            skLineSegment(sketch, "E82.trimOffspring", {"start": v(-307.05, -37.3) * mm, "end": v(-332.14, -63.13) * mm});
            skLineSegment(sketch, "E83.trimOffspring", {"start": v(-299.98, -44.38) * mm, "end": v(-274.52, -69.84) * mm});
            skLineSegment(sketch, "E84.trimOffspring", {"start": v(-293, -37.2) * mm, "end": v(-267.55, -62.67) * mm});
            skLineSegment(sketch, "E85.trimOffspring", {"start": v(-299.98, -44.38) * mm, "end": v(-325.07, -70.2) * mm});
            skLineSegment(sketch, "E86.trimOffspring", {"start": v(-280.52, -10) * mm, "end": v(-320.22, -10) * mm});
            skLineSegment(sketch, "E87.trimOffspring", {"start": v(-216.38, -10) * mm, "end": v(-255.16, -10) * mm});
            skLineSegment(sketch, "E88.trimOffspring", {"start": v(-154.05, -10) * mm, "end": v(-190.1, -10) * mm});
            skLineSegment(sketch, "E89.trimOffspring", {"start": v(-164.29, -35.82) * mm, "end": v(-138.33, -61.77) * mm});
            skLineSegment(sketch, "E90.trimOffspring", {"start": v(-171.26, -43) * mm, "end": v(-145.3, -68.95) * mm});
            skLineSegment(sketch, "E91.trimOffspring", {"start": v(-178.79, -35.46) * mm, "end": v(-203.88, -61.28) * mm});
            skLineSegment(sketch, "E92.trimOffspring", {"start": v(-171.26, -43) * mm, "end": v(-196.34, -68.82) * mm});
            skLineSegment(sketch, "E93.trimOffspring", {"start": v(-196.34, -68.82) * mm, "end": v(-170.4, -94.77) * mm});
            skLineSegment(sketch, "E94.trimOffspring", {"start": v(-203.31, -75.99) * mm, "end": v(-177.36, -101.94) * mm});
            skLineSegment(sketch, "E95.trimOffspring", {"start": v(-203.31, -75.99) * mm, "end": v(-228.4, -101.81) * mm});
            skLineSegment(sketch, "E96.trimOffspring", {"start": v(-210.85, -68.45) * mm, "end": v(-235.94, -94.28) * mm});
            skLineSegment(sketch, "E97.trimOffspring", {"start": v(-236.3, -43) * mm, "end": v(-261.4, -68.82) * mm});
            skLineSegment(sketch, "E98.trimOffspring", {"start": v(-242.46, -36.84) * mm, "end": v(-267.55, -62.67) * mm});
            skLineSegment(sketch, "E99.trimOffspring", {"start": v(-236.3, -43) * mm, "end": v(-210.85, -68.45) * mm});
            skLineSegment(sketch, "E100.trimOffspring", {"start": v(-229.34, -35.82) * mm, "end": v(-203.88, -61.28) * mm});
            skLineSegment(sketch, "E101.trimOffspring", {"start": v(-423.89, -105.9) * mm, "end": v(-398.43, -131.35) * mm});
            skLineSegment(sketch, "E102.trimOffspring", {"start": v(-430.86, -113.07) * mm, "end": v(-440, -122.48) * mm});
            skLineSegment(sketch, "E103.trimOffspring", {"start": v(-364.1, -110.37) * mm, "end": v(-338.64, -135.83) * mm});
            skLineSegment(sketch, "E104.trimOffspring", {"start": v(-371.17, -103.3) * mm, "end": v(-398.43, -131.35) * mm});
            skLineSegment(sketch, "E105.trimOffspring", {"start": v(-364.1, -110.37) * mm, "end": v(-391.36, -138.42) * mm});
            skLineSegment(sketch, "E106.trimOffspring", {"start": v(-357.13, -103.2) * mm, "end": v(-331.67, -128.65) * mm});
            skLineSegment(sketch, "E107.trimOffspring", {"start": v(-300.43, -108.98) * mm, "end": v(-325.52, -134.8) * mm});
            skLineSegment(sketch, "E108.trimOffspring", {"start": v(-306.58, -102.83) * mm, "end": v(-331.67, -128.65) * mm});
            skLineSegment(sketch, "E109.trimOffspring", {"start": v(-300.43, -108.98) * mm, "end": v(-274.97, -134.44) * mm});
            skLineSegment(sketch, "E110.trimOffspring", {"start": v(-293.46, -101.81) * mm, "end": v(-268, -127.27) * mm});
            skLineSegment(sketch, "E111.trimOffspring", {"start": v(-113.24, -35.95) * mm, "end": v(-138.33, -61.77) * mm});
            skLineSegment(sketch, "E112.trimOffspring", {"start": v(-49.14, -100.06) * mm, "end": v(-74.23, -125.88) * mm});
            skLineSegment(sketch, "E113.trimOffspring", {"start": v(-42.06, -107.14) * mm, "end": v(-67.15, -132.96) * mm});
            skLineSegment(sketch, "E114.trimOffspring", {"start": v(-10, -140.15) * mm, "end": v(-10, -190.1) * mm});
            skLineSegment(sketch, "E115.trimOffspring", {"start": v(-10, -74.14) * mm, "end": v(-10, -125.05) * mm});
            skLineSegment(sketch, "E116.trimOffspring", {"start": v(-17.08, -67.06) * mm, "end": v(-42.17, -92.88) * mm});
            skLineSegment(sketch, "E117.trimOffspring", {"start": v(-35.57, -34.43) * mm, "end": v(-11.83, -10) * mm});
            skLineSegment(sketch, "E118.trimOffspring", {"start": v(-88.03, -10) * mm, "end": v(-125.05, -10) * mm});
            skLineSegment(sketch, "E119.trimOffspring", {"start": v(-99.6, -35.46) * mm, "end": v(-74.14, -60.91) * mm});
            skLineSegment(sketch, "E120.trimOffspring", {"start": v(-106.57, -42.63) * mm, "end": v(-81.11, -68.08) * mm});
            skLineSegment(sketch, "E121.trimOffspring", {"start": v(-131.66, -68.45) * mm, "end": v(-106.2, -93.9) * mm});
            skLineSegment(sketch, "E122.trimOffspring", {"start": v(-138.63, -75.62) * mm, "end": v(-113.17, -101.08) * mm});
            skLineSegment(sketch, "E123.trimOffspring", {"start": v(-145.3, -68.95) * mm, "end": v(-170.4, -94.77) * mm});
            skLineSegment(sketch, "E124.trimOffspring", {"start": v(-138.63, -75.62) * mm, "end": v(-163.72, -101.45) * mm});
            skLineSegment(sketch, "E125.trimOffspring", {"start": v(-74.6, -74.6) * mm, "end": v(-49.14, -100.06) * mm});
            skLineSegment(sketch, "E126.trimOffspring", {"start": v(-67.63, -67.43) * mm, "end": v(-42.17, -92.88) * mm});
            skLineSegment(sketch, "E127.trimOffspring", {"start": v(-42.54, -41.6) * mm, "end": v(-17.08, -67.06) * mm});
            skLineSegment(sketch, "E128.trimOffspring", {"start": v(-35.57, -34.43) * mm, "end": v(-10, -60) * mm});
            skLineSegment(sketch, "E129.trimOffspring", {"start": v(-23.95, -10) * mm, "end": v(-60, -10) * mm});
            skLineSegment(sketch, "E130", {"start": v(-11.83, -10) * mm, "end": v(-10, -10) * mm});
            skLineSegment(sketch, "E131.trimOffspring", {"start": v(-35.09, -99.96) * mm, "end": v(-10, -125.05) * mm});
            skLineSegment(sketch, "E132.trimOffspring", {"start": v(-42.06, -107.14) * mm, "end": v(-16.6, -132.6) * mm});
            skLineSegment(sketch, "E133.trimOffspring", {"start": v(-440, -56.47) * mm, "end": v(-440, -89.78) * mm});
            skLineSegment(sketch, "E134.trimOffspring", {"start": v(-423.42, -171.42) * mm, "end": v(-397.96, -196.88) * mm});
            skLineSegment(sketch, "E135.trimOffspring", {"start": v(-430.39, -178.6) * mm, "end": v(-404.93, -204.05) * mm});
            skLineSegment(sketch, "E136.trimOffspring", {"start": v(-440, -188.28) * mm, "end": v(-440, -219.89) * mm});
            skLineSegment(sketch, "E137.trimOffspring", {"start": v(-430.39, -178.6) * mm, "end": v(-440, -188.48) * mm});
            skLineSegment(sketch, "E138.trimOffspring", {"start": v(-398.33, -145.6) * mm, "end": v(-372.87, -171.06) * mm});
            skLineSegment(sketch, "E139.trimOffspring", {"start": v(-405.4, -138.52) * mm, "end": v(-430.49, -164.35) * mm});
            skLineSegment(sketch, "E140.trimOffspring", {"start": v(-391.36, -138.42) * mm, "end": v(-365.9, -163.88) * mm});
            skLineSegment(sketch, "E141.trimOffspring", {"start": v(-398.33, -145.6) * mm, "end": v(-423.42, -171.42) * mm});
            skLineSegment(sketch, "E142.trimOffspring", {"start": v(-338.64, -135.83) * mm, "end": v(-365.9, -163.88) * mm});
            skLineSegment(sketch, "E143.trimOffspring", {"start": v(-332.49, -141.98) * mm, "end": v(-359.75, -170.03) * mm});
            skLineSegment(sketch, "E144.trimOffspring", {"start": v(-325.52, -134.8) * mm, "end": v(-300.06, -160.27) * mm});
            skLineSegment(sketch, "E145.trimOffspring", {"start": v(-332.49, -141.98) * mm, "end": v(-307.03, -167.44) * mm});
            skLineSegment(sketch, "E146.trimOffspring", {"start": v(-274.97, -134.44) * mm, "end": v(-300.06, -160.27) * mm});
            skLineSegment(sketch, "E147.trimOffspring", {"start": v(-260.46, -134.8) * mm, "end": v(-234.51, -160.76) * mm});
            skLineSegment(sketch, "E148.trimOffspring", {"start": v(-267.43, -141.98) * mm, "end": v(-241.48, -167.93) * mm});
            skLineSegment(sketch, "E149.trimOffspring", {"start": v(-267.43, -141.98) * mm, "end": v(-292.52, -167.8) * mm});
            skLineSegment(sketch, "E150.trimOffspring", {"start": v(-209.42, -134.94) * mm, "end": v(-234.51, -160.76) * mm});
            skLineSegment(sketch, "E151.trimOffspring", {"start": v(-195.78, -134.44) * mm, "end": v(-170.32, -159.9) * mm});
            skLineSegment(sketch, "E152.trimOffspring", {"start": v(-202.74, -141.61) * mm, "end": v(-177.29, -167.07) * mm});
            skLineSegment(sketch, "E153.trimOffspring", {"start": v(-202.74, -141.61) * mm, "end": v(-227.83, -167.43) * mm});
            skLineSegment(sketch, "E154.trimOffspring", {"start": v(-145.23, -134.07) * mm, "end": v(-170.32, -159.9) * mm});
            skLineSegment(sketch, "E155.trimOffspring", {"start": v(-131.75, -133.41) * mm, "end": v(-106.29, -158.87) * mm});
            skLineSegment(sketch, "E156.trimOffspring", {"start": v(-138.72, -140.59) * mm, "end": v(-113.26, -166.05) * mm});
            skLineSegment(sketch, "E157.trimOffspring", {"start": v(-138.72, -140.59) * mm, "end": v(-163.8, -166.4) * mm});
            skLineSegment(sketch, "E158.trimOffspring", {"start": v(-81.2, -133.05) * mm, "end": v(-106.29, -158.87) * mm});
            skLineSegment(sketch, "E159.trimOffspring", {"start": v(-67.15, -132.96) * mm, "end": v(-41.7, -158.42) * mm});
            skLineSegment(sketch, "E160.trimOffspring", {"start": v(-74.12, -140.13) * mm, "end": v(-48.66, -165.59) * mm});
            skLineSegment(sketch, "E161.trimOffspring", {"start": v(-74.12, -140.13) * mm, "end": v(-99.2, -165.95) * mm});
            skLineSegment(sketch, "E162.trimOffspring", {"start": v(-48.66, -165.59) * mm, "end": v(-73.75, -191.41) * mm});
            skLineSegment(sketch, "E163.trimOffspring", {"start": v(-34.62, -165.49) * mm, "end": v(-10, -190.1) * mm});
            skLineSegment(sketch, "E164.trimOffspring", {"start": v(-41.59, -172.66) * mm, "end": v(-16.13, -198.12) * mm});
            skLineSegment(sketch, "E165.trimOffspring", {"start": v(-41.59, -172.66) * mm, "end": v(-66.68, -198.48) * mm});
            skLineSegment(sketch, "E166.trimOffspring", {"start": v(-99.2, -165.95) * mm, "end": v(-73.75, -191.41) * mm});
            skLineSegment(sketch, "E167.trimOffspring", {"start": v(-106.18, -173.13) * mm, "end": v(-80.72, -198.58) * mm});
            skLineSegment(sketch, "E168.trimOffspring", {"start": v(-113.26, -166.05) * mm, "end": v(-138.35, -191.87) * mm});
            skLineSegment(sketch, "E169.trimOffspring", {"start": v(-106.18, -173.13) * mm, "end": v(-131.27, -198.95) * mm});
            skLineSegment(sketch, "E170.trimOffspring", {"start": v(-163.8, -166.4) * mm, "end": v(-138.35, -191.87) * mm});
            skLineSegment(sketch, "E171.trimOffspring", {"start": v(-170.78, -173.58) * mm, "end": v(-145.32, -199.04) * mm});
            skLineSegment(sketch, "E172.trimOffspring", {"start": v(-177.29, -167.07) * mm, "end": v(-202.38, -192.9) * mm});
            skLineSegment(sketch, "E173.trimOffspring", {"start": v(-170.78, -173.58) * mm, "end": v(-195.87, -199.4) * mm});
            skLineSegment(sketch, "E174.trimOffspring", {"start": v(-359.75, -170.03) * mm, "end": v(-334.29, -195.5) * mm});
            skLineSegment(sketch, "E175.trimOffspring", {"start": v(-372.87, -171.06) * mm, "end": v(-397.96, -196.88) * mm});
            skLineSegment(sketch, "E176.trimOffspring", {"start": v(-366.72, -177.2) * mm, "end": v(-341.26, -202.67) * mm});
            skLineSegment(sketch, "E177.trimOffspring", {"start": v(-366.72, -177.2) * mm, "end": v(-391.8, -203.03) * mm});
            skLineSegment(sketch, "E178.trimOffspring", {"start": v(-404.93, -204.05) * mm, "end": v(-430.02, -229.87) * mm});
            skLineSegment(sketch, "E179.trimOffspring", {"start": v(-391.8, -203.03) * mm, "end": v(-366.35, -228.49) * mm});
            skLineSegment(sketch, "E180.trimOffspring", {"start": v(-398.78, -210.2) * mm, "end": v(-373.32, -235.66) * mm});
            skLineSegment(sketch, "E181.trimOffspring", {"start": v(-398.78, -210.2) * mm, "end": v(-423.87, -236.02) * mm});
            skLineSegment(sketch, "E182.trimOffspring", {"start": v(-341.26, -202.67) * mm, "end": v(-366.35, -228.49) * mm});
            skLineSegment(sketch, "E183.trimOffspring", {"start": v(-326.75, -203.03) * mm, "end": v(-300.8, -228.98) * mm});
            skLineSegment(sketch, "E184.trimOffspring", {"start": v(-333.72, -210.2) * mm, "end": v(-307.77, -236.15) * mm});
            skLineSegment(sketch, "E185.trimOffspring", {"start": v(-333.72, -210.2) * mm, "end": v(-358.81, -236.02) * mm});
            skLineSegment(sketch, "E186.trimOffspring", {"start": v(-266.86, -207.6) * mm, "end": v(-241.4, -233.06) * mm});
            skLineSegment(sketch, "E187.trimOffspring", {"start": v(-273.54, -200.92) * mm, "end": v(-300.8, -228.98) * mm});
            skLineSegment(sketch, "E188.trimOffspring", {"start": v(-259.9, -200.43) * mm, "end": v(-234.44, -225.88) * mm});
            skLineSegment(sketch, "E189.trimOffspring", {"start": v(-266.86, -207.6) * mm, "end": v(-294.12, -235.66) * mm});
            skLineSegment(sketch, "E190.trimOffspring", {"start": v(-202.83, -206.58) * mm, "end": v(-177.38, -232.04) * mm});
            skLineSegment(sketch, "E191.trimOffspring", {"start": v(-195.87, -199.4) * mm, "end": v(-170.4, -224.86) * mm});
            skLineSegment(sketch, "E192.trimOffspring", {"start": v(-202.83, -206.58) * mm, "end": v(-227.92, -232.4) * mm});
            skLineSegment(sketch, "E193.trimOffspring", {"start": v(-131.27, -198.95) * mm, "end": v(-105.8, -224.4) * mm});
            skLineSegment(sketch, "E194.trimOffspring", {"start": v(-138.24, -206.12) * mm, "end": v(-163.33, -231.94) * mm});
            skLineSegment(sketch, "E195.trimOffspring", {"start": v(-138.24, -206.12) * mm, "end": v(-112.78, -231.58) * mm});
            skLineSegment(sketch, "E196.trimOffspring", {"start": v(-145.32, -199.04) * mm, "end": v(-170.4, -224.86) * mm});
            skLineSegment(sketch, "E197.trimOffspring", {"start": v(-209.35, -200.06) * mm, "end": v(-234.44, -225.88) * mm});
            skLineSegment(sketch, "E198.trimOffspring", {"start": v(-241.48, -167.93) * mm, "end": v(-266.57, -193.75) * mm});
            skLineSegment(sketch, "E199.trimOffspring", {"start": v(-234.8, -174.6) * mm, "end": v(-259.9, -200.43) * mm});
            skLineSegment(sketch, "E200.trimOffspring", {"start": v(-227.83, -167.43) * mm, "end": v(-202.38, -192.9) * mm});
            skLineSegment(sketch, "E201.trimOffspring", {"start": v(-234.8, -174.6) * mm, "end": v(-209.35, -200.06) * mm});
            skLineSegment(sketch, "E202.trimOffspring", {"start": v(-292.52, -167.8) * mm, "end": v(-266.57, -193.75) * mm});
            skLineSegment(sketch, "E203.trimOffspring", {"start": v(-307.03, -167.44) * mm, "end": v(-334.29, -195.5) * mm});
            skLineSegment(sketch, "E204.trimOffspring", {"start": v(-299.5, -174.97) * mm, "end": v(-273.54, -200.92) * mm});
            skLineSegment(sketch, "E205.trimOffspring", {"start": v(-299.5, -174.97) * mm, "end": v(-326.75, -203.03) * mm});
            skLineSegment(sketch, "E206.trimOffspring", {"start": v(-80.72, -198.58) * mm, "end": v(-105.8, -224.4) * mm});
            skLineSegment(sketch, "E207.trimOffspring", {"start": v(-66.68, -198.48) * mm, "end": v(-41.22, -223.94) * mm});
            skLineSegment(sketch, "E208.trimOffspring", {"start": v(-73.65, -205.66) * mm, "end": v(-98.74, -231.48) * mm});
            skLineSegment(sketch, "E209.trimOffspring", {"start": v(-73.65, -205.66) * mm, "end": v(-48.19, -231.11) * mm});
            skLineSegment(sketch, "E210.trimOffspring", {"start": v(-10, -206.16) * mm, "end": v(-10, -255.16) * mm});
            skLineSegment(sketch, "E211.trimOffspring", {"start": v(-34.15, -231.01) * mm, "end": v(-10, -255.16) * mm});
            skLineSegment(sketch, "E212.trimOffspring", {"start": v(-48.19, -231.11) * mm, "end": v(-73.28, -256.94) * mm});
            skLineSegment(sketch, "E213.trimOffspring", {"start": v(-41.12, -238.19) * mm, "end": v(-15.66, -263.65) * mm});
            skLineSegment(sketch, "E214.trimOffspring", {"start": v(-41.12, -238.19) * mm, "end": v(-66.2, -264) * mm});
            skLineSegment(sketch, "E215.trimOffspring", {"start": v(-98.74, -231.48) * mm, "end": v(-73.28, -256.94) * mm});
            skLineSegment(sketch, "E216.trimOffspring", {"start": v(-112.78, -231.58) * mm, "end": v(-137.87, -257.4) * mm});
            skLineSegment(sketch, "E217.trimOffspring", {"start": v(-105.7, -238.65) * mm, "end": v(-80.25, -264.1) * mm});
            skLineSegment(sketch, "E218.trimOffspring", {"start": v(-105.7, -238.65) * mm, "end": v(-130.8, -264.47) * mm});
            skLineSegment(sketch, "E219.trimOffspring", {"start": v(-163.33, -231.94) * mm, "end": v(-137.87, -257.4) * mm});
            skLineSegment(sketch, "E220.trimOffspring", {"start": v(-177.38, -232.04) * mm, "end": v(-202.47, -257.86) * mm});
            skLineSegment(sketch, "E221.trimOffspring", {"start": v(-170.3, -239.12) * mm, "end": v(-144.84, -264.57) * mm});
            skLineSegment(sketch, "E222.trimOffspring", {"start": v(-170.3, -239.12) * mm, "end": v(-195.39, -264.94) * mm});
            skLineSegment(sketch, "E223.trimOffspring", {"start": v(-227.92, -232.4) * mm, "end": v(-202.47, -257.86) * mm});
            skLineSegment(sketch, "E224.trimOffspring", {"start": v(-241.4, -233.06) * mm, "end": v(-268.67, -261.11) * mm});
            skLineSegment(sketch, "E225.trimOffspring", {"start": v(-234.9, -239.57) * mm, "end": v(-209.44, -265.03) * mm});
            skLineSegment(sketch, "E226.trimOffspring", {"start": v(-234.9, -239.57) * mm, "end": v(-262.15, -267.63) * mm});
            skLineSegment(sketch, "E227.trimOffspring", {"start": v(-294.12, -235.66) * mm, "end": v(-268.67, -261.11) * mm});
            skLineSegment(sketch, "E228.trimOffspring", {"start": v(-307.77, -236.15) * mm, "end": v(-332.86, -261.98) * mm});
            skLineSegment(sketch, "E229.trimOffspring", {"start": v(-301.1, -242.83) * mm, "end": v(-275.64, -268.29) * mm});
            skLineSegment(sketch, "E230.trimOffspring", {"start": v(-301.1, -242.83) * mm, "end": v(-326.18, -268.65) * mm});
            skLineSegment(sketch, "E231.trimOffspring", {"start": v(-358.81, -236.02) * mm, "end": v(-332.86, -261.98) * mm});
            skLineSegment(sketch, "E232.trimOffspring", {"start": v(-373.32, -235.66) * mm, "end": v(-398.4, -261.48) * mm});
            skLineSegment(sketch, "E233.trimOffspring", {"start": v(-365.78, -243.2) * mm, "end": v(-339.83, -269.15) * mm});
            skLineSegment(sketch, "E234.trimOffspring", {"start": v(-365.78, -243.2) * mm, "end": v(-390.87, -269.02) * mm});
            skLineSegment(sketch, "E235.trimOffspring", {"start": v(-423.87, -236.02) * mm, "end": v(-398.4, -261.48) * mm});
            skLineSegment(sketch, "E236.trimOffspring", {"start": v(-430.84, -243.2) * mm, "end": v(-405.38, -268.66) * mm});
            skLineSegment(sketch, "E237.trimOffspring", {"start": v(-430.84, -243.2) * mm, "end": v(-440, -252.63) * mm});
            skLineSegment(sketch, "E238.trimOffspring", {"start": v(-440, -252.63) * mm, "end": v(-440, -284.94) * mm});
            skLineSegment(sketch, "E239.trimOffspring", {"start": v(-405.38, -268.66) * mm, "end": v(-430.46, -294.48) * mm});
            skLineSegment(sketch, "E240.trimOffspring", {"start": v(-397.84, -276.2) * mm, "end": v(-371.89, -302.14) * mm});
            skLineSegment(sketch, "E241.trimOffspring", {"start": v(-390.87, -269.02) * mm, "end": v(-364.92, -294.97) * mm});
            skLineSegment(sketch, "E242.trimOffspring", {"start": v(-397.84, -276.2) * mm, "end": v(-422.93, -302.01) * mm});
            skLineSegment(sketch, "E243.trimOffspring", {"start": v(-339.83, -269.15) * mm, "end": v(-364.92, -294.97) * mm});
            skLineSegment(sketch, "E244.trimOffspring", {"start": v(-326.18, -268.65) * mm, "end": v(-300.73, -294.1) * mm});
            skLineSegment(sketch, "E245.trimOffspring", {"start": v(-333.15, -275.83) * mm, "end": v(-358.24, -301.65) * mm});
            skLineSegment(sketch, "E246.trimOffspring", {"start": v(-333.15, -275.83) * mm, "end": v(-307.7, -301.28) * mm});
            skLineSegment(sketch, "E247.trimOffspring", {"start": v(-269.12, -274.8) * mm, "end": v(-243.67, -300.26) * mm});
            skLineSegment(sketch, "E248.trimOffspring", {"start": v(-275.64, -268.29) * mm, "end": v(-300.73, -294.1) * mm});
            skLineSegment(sketch, "E249.trimOffspring", {"start": v(-262.15, -267.63) * mm, "end": v(-236.7, -293.09) * mm});
            skLineSegment(sketch, "E250.trimOffspring", {"start": v(-269.12, -274.8) * mm, "end": v(-294.21, -300.62) * mm});
            skLineSegment(sketch, "E251.trimOffspring", {"start": v(-209.44, -265.03) * mm, "end": v(-236.7, -293.09) * mm});
            skLineSegment(sketch, "E252.trimOffspring", {"start": v(-202.36, -272.1) * mm, "end": v(-176.9, -297.57) * mm});
            skLineSegment(sketch, "E253.trimOffspring", {"start": v(-195.39, -264.94) * mm, "end": v(-169.93, -290.4) * mm});
            skLineSegment(sketch, "E254.trimOffspring", {"start": v(-202.36, -272.1) * mm, "end": v(-229.62, -300.17) * mm});
            skLineSegment(sketch, "E255.trimOffspring", {"start": v(-137.77, -271.65) * mm, "end": v(-112.3, -297.1) * mm});
            skLineSegment(sketch, "E256.trimOffspring", {"start": v(-144.84, -264.57) * mm, "end": v(-169.93, -290.4) * mm});
            skLineSegment(sketch, "E257.trimOffspring", {"start": v(-130.8, -264.47) * mm, "end": v(-105.34, -289.93) * mm});
            skLineSegment(sketch, "E258.trimOffspring", {"start": v(-137.77, -271.65) * mm, "end": v(-162.86, -297.47) * mm});
            skLineSegment(sketch, "E259.trimOffspring", {"start": v(-73.18, -271.18) * mm, "end": v(-47.72, -296.64) * mm});
            skLineSegment(sketch, "E260.trimOffspring", {"start": v(-80.25, -264.1) * mm, "end": v(-105.34, -289.93) * mm});
            skLineSegment(sketch, "E261.trimOffspring", {"start": v(-66.2, -264) * mm, "end": v(-40.75, -289.47) * mm});
            skLineSegment(sketch, "E262.trimOffspring", {"start": v(-73.18, -271.18) * mm, "end": v(-98.27, -297) * mm});
            skLineSegment(sketch, "E263.trimOffspring", {"start": v(-10, -272.17) * mm, "end": v(-10, -320.22) * mm});
            skLineSegment(sketch, "E264.trimOffspring", {"start": v(-33.68, -296.54) * mm, "end": v(-10, -320.22) * mm});
            skLineSegment(sketch, "E265.trimOffspring", {"start": v(-47.72, -296.64) * mm, "end": v(-72.8, -322.46) * mm});
            skLineSegment(sketch, "E266.trimOffspring", {"start": v(-40.65, -303.71) * mm, "end": v(-15.19, -329.17) * mm});
            skLineSegment(sketch, "E267.trimOffspring", {"start": v(-40.65, -303.71) * mm, "end": v(-65.74, -329.53) * mm});
            skLineSegment(sketch, "E268.trimOffspring", {"start": v(-98.27, -297) * mm, "end": v(-72.8, -322.46) * mm});
            skLineSegment(sketch, "E269.trimOffspring", {"start": v(-112.3, -297.1) * mm, "end": v(-137.4, -322.93) * mm});
            skLineSegment(sketch, "E270.trimOffspring", {"start": v(-105.24, -304.18) * mm, "end": v(-79.78, -329.63) * mm});
            skLineSegment(sketch, "E271.trimOffspring", {"start": v(-105.24, -304.18) * mm, "end": v(-130.33, -330) * mm});
            skLineSegment(sketch, "E272.trimOffspring", {"start": v(-162.86, -297.47) * mm, "end": v(-137.4, -322.93) * mm});
            skLineSegment(sketch, "E273.trimOffspring", {"start": v(-176.9, -297.57) * mm, "end": v(-204.16, -325.62) * mm});
            skLineSegment(sketch, "E274.trimOffspring", {"start": v(-169.82, -304.64) * mm, "end": v(-144.37, -330.1) * mm});
            skLineSegment(sketch, "E275.trimOffspring", {"start": v(-169.82, -304.64) * mm, "end": v(-197.09, -332.7) * mm});
            skLineSegment(sketch, "E276.trimOffspring", {"start": v(-229.62, -300.17) * mm, "end": v(-204.16, -325.62) * mm});
            skLineSegment(sketch, "E277.trimOffspring", {"start": v(-243.67, -300.26) * mm, "end": v(-268.76, -326.08) * mm});
            skLineSegment(sketch, "E278.trimOffspring", {"start": v(-236.59, -307.34) * mm, "end": v(-211.13, -332.8) * mm});
            skLineSegment(sketch, "E279.trimOffspring", {"start": v(-236.59, -307.34) * mm, "end": v(-261.68, -333.16) * mm});
            skLineSegment(sketch, "E280.trimOffspring", {"start": v(-294.21, -300.62) * mm, "end": v(-268.76, -326.08) * mm});
            skLineSegment(sketch, "E281.trimOffspring", {"start": v(-307.7, -301.28) * mm, "end": v(-332.79, -327.1) * mm});
            skLineSegment(sketch, "E282.trimOffspring", {"start": v(-301.18, -307.8) * mm, "end": v(-275.72, -333.25) * mm});
            skLineSegment(sketch, "E283.trimOffspring", {"start": v(-301.18, -307.8) * mm, "end": v(-326.27, -333.62) * mm});
            skLineSegment(sketch, "E284.trimOffspring", {"start": v(-358.24, -301.65) * mm, "end": v(-332.79, -327.1) * mm});
            skLineSegment(sketch, "E285.trimOffspring", {"start": v(-365.21, -308.82) * mm, "end": v(-339.76, -334.28) * mm});
            skLineSegment(sketch, "E286.trimOffspring", {"start": v(-365.21, -308.82) * mm, "end": v(-390.3, -334.64) * mm});
            skLineSegment(sketch, "E287.trimOffspring", {"start": v(-371.89, -302.14) * mm, "end": v(-396.98, -327.97) * mm});
            skLineSegment(sketch, "E288.trimOffspring", {"start": v(-422.93, -302.01) * mm, "end": v(-396.98, -327.97) * mm});
            skLineSegment(sketch, "E289.trimOffspring", {"start": v(-429.9, -309.19) * mm, "end": v(-403.95, -335.14) * mm});
            skLineSegment(sketch, "E290.trimOffspring", {"start": v(-429.9, -309.19) * mm, "end": v(-440, -319.58) * mm});
            skLineSegment(sketch, "E291.trimOffspring", {"start": v(-440, -319.58) * mm, "end": v(-440, -350) * mm});
            skLineSegment(sketch, "E292.trimOffspring", {"start": v(-422.36, -367.64) * mm, "end": v(-396.9, -393.1) * mm});
            skLineSegment(sketch, "E293.trimOffspring", {"start": v(-429.33, -374.8) * mm, "end": v(-403.87, -400.27) * mm});
            skLineSegment(sketch, "E294.trimOffspring", {"start": v(-429.33, -374.8) * mm, "end": v(-440, -385.8) * mm});
            skLineSegment(sketch, "E295.trimOffspring", {"start": v(-440, -385.8) * mm, "end": v(-440, -415.05) * mm});
            skLineSegment(sketch, "E296.trimOffspring", {"start": v(-371.82, -367.27) * mm, "end": v(-396.9, -393.1) * mm});
            skLineSegment(sketch, "E297.trimOffspring", {"start": v(-358.33, -366.61) * mm, "end": v(-332.87, -392.07) * mm});
            skLineSegment(sketch, "E298.trimOffspring", {"start": v(-365.3, -373.78) * mm, "end": v(-339.84, -399.24) * mm});
            skLineSegment(sketch, "E299.trimOffspring", {"start": v(-365.3, -373.78) * mm, "end": v(-390.4, -399.6) * mm});
            skLineSegment(sketch, "E300.trimOffspring", {"start": v(-390.3, -334.64) * mm, "end": v(-364.85, -360.1) * mm});
            skLineSegment(sketch, "E301.trimOffspring", {"start": v(-397.27, -341.81) * mm, "end": v(-371.82, -367.27) * mm});
            skLineSegment(sketch, "E302.trimOffspring", {"start": v(-403.95, -335.14) * mm, "end": v(-429.04, -360.96) * mm});
            skLineSegment(sketch, "E303.trimOffspring", {"start": v(-397.27, -341.81) * mm, "end": v(-422.36, -367.64) * mm});
            skLineSegment(sketch, "E304.trimOffspring", {"start": v(-333.24, -340.79) * mm, "end": v(-307.78, -366.25) * mm});
            skLineSegment(sketch, "E305.trimOffspring", {"start": v(-326.27, -333.62) * mm, "end": v(-300.81, -359.08) * mm});
            skLineSegment(sketch, "E306.trimOffspring", {"start": v(-339.76, -334.28) * mm, "end": v(-364.85, -360.1) * mm});
            skLineSegment(sketch, "E307.trimOffspring", {"start": v(-333.24, -340.79) * mm, "end": v(-358.33, -366.61) * mm});
            skLineSegment(sketch, "E308.trimOffspring", {"start": v(-268.64, -340.33) * mm, "end": v(-243.19, -365.8) * mm});
            skLineSegment(sketch, "E309.trimOffspring", {"start": v(-261.68, -333.16) * mm, "end": v(-236.22, -358.62) * mm});
            skLineSegment(sketch, "E310.trimOffspring", {"start": v(-275.72, -333.25) * mm, "end": v(-300.81, -359.08) * mm});
            skLineSegment(sketch, "E311.trimOffspring", {"start": v(-268.64, -340.33) * mm, "end": v(-293.73, -366.16) * mm});
            skLineSegment(sketch, "E312.trimOffspring", {"start": v(-204.05, -339.87) * mm, "end": v(-178.6, -365.33) * mm});
            skLineSegment(sketch, "E313.trimOffspring", {"start": v(-197.09, -332.7) * mm, "end": v(-171.63, -358.15) * mm});
            skLineSegment(sketch, "E314.trimOffspring", {"start": v(-211.13, -332.8) * mm, "end": v(-236.22, -358.62) * mm});
            skLineSegment(sketch, "E315.trimOffspring", {"start": v(-204.05, -339.87) * mm, "end": v(-229.14, -365.7) * mm});
            skLineSegment(sketch, "E316.trimOffspring", {"start": v(-130.33, -330) * mm, "end": v(-104.87, -355.46) * mm});
            skLineSegment(sketch, "E317.trimOffspring", {"start": v(-144.37, -330.1) * mm, "end": v(-171.63, -358.15) * mm});
            skLineSegment(sketch, "E318.trimOffspring", {"start": v(-137.3, -337.17) * mm, "end": v(-164.56, -365.23) * mm});
            skLineSegment(sketch, "E319.trimOffspring", {"start": v(-72.7, -336.7) * mm, "end": v(-47.25, -362.16) * mm});
            skLineSegment(sketch, "E320.trimOffspring", {"start": v(-65.74, -329.53) * mm, "end": v(-40.28, -355) * mm});
            skLineSegment(sketch, "E321.trimOffspring", {"start": v(-79.78, -329.63) * mm, "end": v(-104.87, -355.46) * mm});
            skLineSegment(sketch, "E322.trimOffspring", {"start": v(-72.7, -336.7) * mm, "end": v(-97.8, -362.53) * mm});
            skLineSegment(sketch, "E323.trimOffspring", {"start": v(-10, -338.18) * mm, "end": v(-10, -385.27) * mm});
            skLineSegment(sketch, "E324.trimOffspring", {"start": v(-33.2, -362.06) * mm, "end": v(-10, -385.27) * mm});
            skLineSegment(sketch, "E325.trimOffspring", {"start": v(-40.17, -369.24) * mm, "end": v(-14.72, -394.7) * mm});
            skLineSegment(sketch, "E326.trimOffspring", {"start": v(-47.25, -362.16) * mm, "end": v(-72.34, -387.99) * mm});
            skLineSegment(sketch, "E327.trimOffspring", {"start": v(-40.17, -369.24) * mm, "end": v(-65.26, -395.06) * mm});
            skLineSegment(sketch, "E328.trimOffspring", {"start": v(-97.8, -362.53) * mm, "end": v(-72.34, -387.99) * mm});
            skLineSegment(sketch, "E329.trimOffspring", {"start": v(-104.76, -369.7) * mm, "end": v(-79.3, -395.16) * mm});
            skLineSegment(sketch, "E330.trimOffspring", {"start": v(-111.84, -362.63) * mm, "end": v(-139.1, -390.69) * mm});
            skLineSegment(sketch, "E331.trimOffspring", {"start": v(-104.76, -369.7) * mm, "end": v(-132.03, -397.76) * mm});
            skLineSegment(sketch, "E332.trimOffspring", {"start": v(-164.56, -365.23) * mm, "end": v(-139.1, -390.69) * mm});
            skLineSegment(sketch, "E333.trimOffspring", {"start": v(-171.52, -372.4) * mm, "end": v(-146.07, -397.86) * mm});
            skLineSegment(sketch, "E334.trimOffspring", {"start": v(-178.6, -365.33) * mm, "end": v(-203.69, -391.15) * mm});
            skLineSegment(sketch, "E335.trimOffspring", {"start": v(-171.52, -372.4) * mm, "end": v(-196.61, -398.22) * mm});
            skLineSegment(sketch, "E336.trimOffspring", {"start": v(-229.14, -365.7) * mm, "end": v(-203.69, -391.15) * mm});
            skLineSegment(sketch, "E337.trimOffspring", {"start": v(-236.11, -372.86) * mm, "end": v(-210.66, -398.32) * mm});
            skLineSegment(sketch, "E338.trimOffspring", {"start": v(-243.19, -365.8) * mm, "end": v(-268.28, -391.61) * mm});
            skLineSegment(sketch, "E339.trimOffspring", {"start": v(-236.11, -372.86) * mm, "end": v(-261.2, -398.69) * mm});
            skLineSegment(sketch, "E340.trimOffspring", {"start": v(-293.73, -366.16) * mm, "end": v(-268.28, -391.61) * mm});
            skLineSegment(sketch, "E341.trimOffspring", {"start": v(-300.7, -373.33) * mm, "end": v(-275.25, -398.79) * mm});
            skLineSegment(sketch, "E342.trimOffspring", {"start": v(-307.78, -366.25) * mm, "end": v(-332.87, -392.07) * mm});
            skLineSegment(sketch, "E343.trimOffspring", {"start": v(-300.7, -373.33) * mm, "end": v(-325.8, -399.15) * mm});
            skLineSegment(sketch, "E344.trimOffspring", {"start": v(-440, -450.66) * mm, "end": v(-440, -460.75) * mm});
            skLineSegment(sketch, "E345.trimOffspring", {"start": v(-422.45, -432.6) * mm, "end": v(-397, -458.06) * mm});
            skLineSegment(sketch, "E346.trimOffspring", {"start": v(-429.42, -439.77) * mm, "end": v(-440, -450.66) * mm});
            skLineSegment(sketch, "E347.trimOffspring", {"start": v(-403.87, -400.27) * mm, "end": v(-428.96, -426.09) * mm});
            skLineSegment(sketch, "E348.trimOffspring", {"start": v(-397.36, -406.78) * mm, "end": v(-422.45, -432.6) * mm});
            skLineSegment(sketch, "E349.trimOffspring", {"start": v(-390.4, -399.6) * mm, "end": v(-364.93, -425.06) * mm});
            skLineSegment(sketch, "E350.trimOffspring", {"start": v(-397.36, -406.78) * mm, "end": v(-371.9, -432.24) * mm});
            skLineSegment(sketch, "E351.trimOffspring", {"start": v(-332.76, -406.32) * mm, "end": v(-307.3, -431.78) * mm});
            skLineSegment(sketch, "E352.trimOffspring", {"start": v(-325.8, -399.15) * mm, "end": v(-300.33, -424.6) * mm});
            skLineSegment(sketch, "E353.trimOffspring", {"start": v(-339.84, -399.24) * mm, "end": v(-364.93, -425.06) * mm});
            skLineSegment(sketch, "E354.trimOffspring", {"start": v(-332.76, -406.32) * mm, "end": v(-357.85, -432.14) * mm});
            skLineSegment(sketch, "E355.trimOffspring", {"start": v(-268.17, -405.86) * mm, "end": v(-242.71, -431.32) * mm});
            skLineSegment(sketch, "E356.trimOffspring", {"start": v(-261.2, -398.69) * mm, "end": v(-235.75, -424.14) * mm});
            skLineSegment(sketch, "E357.trimOffspring", {"start": v(-275.25, -398.79) * mm, "end": v(-300.33, -424.6) * mm});
            skLineSegment(sketch, "E358.trimOffspring", {"start": v(-268.17, -405.86) * mm, "end": v(-293.26, -431.68) * mm});
            skLineSegment(sketch, "E359.trimOffspring", {"start": v(-203.58, -405.4) * mm, "end": v(-178.13, -430.85) * mm});
            skLineSegment(sketch, "E360.trimOffspring", {"start": v(-210.66, -398.32) * mm, "end": v(-235.75, -424.14) * mm});
            skLineSegment(sketch, "E361.trimOffspring", {"start": v(-203.58, -405.4) * mm, "end": v(-228.67, -431.22) * mm});
            skLineSegment(sketch, "E362.trimOffspring", {"start": v(-132.03, -397.76) * mm, "end": v(-106.57, -423.22) * mm});
            skLineSegment(sketch, "E363.trimOffspring", {"start": v(-146.07, -397.86) * mm, "end": v(-171.16, -423.68) * mm});
            skLineSegment(sketch, "E364.trimOffspring", {"start": v(-139, -404.93) * mm, "end": v(-164.08, -430.75) * mm});
            skLineSegment(sketch, "E365.trimOffspring", {"start": v(-65.26, -395.06) * mm, "end": v(-39.8, -420.52) * mm});
            skLineSegment(sketch, "E366.trimOffspring", {"start": v(-72.23, -402.23) * mm, "end": v(-99.5, -430.29) * mm});
            skLineSegment(sketch, "E367.trimOffspring", {"start": v(-10, -404.2) * mm, "end": v(-10, -450.32) * mm});
            skLineSegment(sketch, "E368.trimOffspring", {"start": v(-72.23, -402.23) * mm, "end": v(-46.78, -427.69) * mm});
            skLineSegment(sketch, "E369.trimOffspring", {"start": v(-139, -404.93) * mm, "end": v(-113.54, -430.39) * mm});
            skLineSegment(sketch, "E370.trimOffspring", {"start": v(-409.2, -460) * mm, "end": v(-440, -460) * mm});
            skLineSegment(sketch, "E371.trimOffspring", {"start": v(-364.82, -439.32) * mm, "end": v(-344.14, -460) * mm});
            skLineSegment(sketch, "E372.trimOffspring", {"start": v(-357.85, -432.14) * mm, "end": v(-332.4, -457.6) * mm});
            skLineSegment(sketch, "E373.trimOffspring", {"start": v(-371.9, -432.24) * mm, "end": v(-397, -458.06) * mm});
            skLineSegment(sketch, "E374.trimOffspring", {"start": v(-364.82, -439.32) * mm, "end": v(-384.92, -460) * mm});
            skLineSegment(sketch, "E375.trimOffspring", {"start": v(-344.14, -460) * mm, "end": v(-384.92, -460) * mm});
            skLineSegment(sketch, "E376.trimOffspring", {"start": v(-300.23, -438.85) * mm, "end": v(-279.09, -460) * mm});
            skLineSegment(sketch, "E377.trimOffspring", {"start": v(-293.26, -431.68) * mm, "end": v(-267.8, -457.14) * mm});
            skLineSegment(sketch, "E378.trimOffspring", {"start": v(-307.3, -431.78) * mm, "end": v(-332.4, -457.6) * mm});
            skLineSegment(sketch, "E379.trimOffspring", {"start": v(-300.23, -438.85) * mm, "end": v(-320.78, -460) * mm});
            skLineSegment(sketch, "E380.trimOffspring", {"start": v(-279.09, -460) * mm, "end": v(-320.78, -460) * mm});
            skLineSegment(sketch, "E381.trimOffspring", {"start": v(-235.64, -438.39) * mm, "end": v(-214.03, -460) * mm});
            skLineSegment(sketch, "E382.trimOffspring", {"start": v(-228.67, -431.22) * mm, "end": v(-203.22, -456.67) * mm});
            skLineSegment(sketch, "E383.trimOffspring", {"start": v(-235.64, -438.39) * mm, "end": v(-256.65, -460) * mm});
            skLineSegment(sketch, "E384.trimOffspring", {"start": v(-242.71, -431.32) * mm, "end": v(-267.8, -457.14) * mm});
            skLineSegment(sketch, "E385.trimOffspring", {"start": v(-214.03, -460) * mm, "end": v(-256.64, -460) * mm});
            skLineSegment(sketch, "E386.trimOffspring", {"start": v(-171.05, -437.92) * mm, "end": v(-148.98, -460) * mm});
            skLineSegment(sketch, "E387.trimOffspring", {"start": v(-178.13, -430.85) * mm, "end": v(-203.22, -456.67) * mm});
            skLineSegment(sketch, "E388.trimOffspring", {"start": v(-164.08, -430.75) * mm, "end": v(-138.63, -456.21) * mm});
            skLineSegment(sketch, "E389.trimOffspring", {"start": v(-171.05, -437.92) * mm, "end": v(-191.53, -459) * mm});
            skLineSegment(sketch, "E390.trimOffspring", {"start": v(-148.98, -460) * mm, "end": v(-192.5, -460) * mm});
            skLineSegment(sketch, "E391.trimOffspring", {"start": v(-106.46, -437.46) * mm, "end": v(-83.92, -460) * mm});
            skLineSegment(sketch, "E392.trimOffspring", {"start": v(-113.54, -430.39) * mm, "end": v(-138.63, -456.21) * mm});
            skLineSegment(sketch, "E393.trimOffspring", {"start": v(-99.5, -430.29) * mm, "end": v(-74.04, -455.75) * mm});
            skLineSegment(sketch, "E394.trimOffspring", {"start": v(-106.46, -437.46) * mm, "end": v(-126.95, -458.54) * mm});
            skLineSegment(sketch, "E395.trimOffspring", {"start": v(-83.92, -460) * mm, "end": v(-128.37, -460) * mm});
            skLineSegment(sketch, "E396.trimOffspring", {"start": v(-39.7, -434.76) * mm, "end": v(-14.47, -460) * mm});
            skLineSegment(sketch, "E397.trimOffspring", {"start": v(-46.78, -427.69) * mm, "end": v(-74.04, -455.75) * mm});
            skLineSegment(sketch, "E398.trimOffspring", {"start": v(-32.73, -427.59) * mm, "end": v(-10, -450.32) * mm});
            skLineSegment(sketch, "E399.trimOffspring", {"start": v(-39.7, -434.76) * mm, "end": v(-62.36, -458.08) * mm});
            skLineSegment(sketch, "E400.trimOffspring", {"start": v(-440, -122.48) * mm, "end": v(-440, -154.84) * mm});
            skLineSegment(sketch, "E401.trimOffspring", {"start": v(-325.07, -70.2) * mm, "end": v(-299.6, -95.66) * mm});
            skLineSegment(sketch, "E402.trimOffspring", {"start": v(-332.04, -77.37) * mm, "end": v(-306.58, -102.83) * mm});
            skLineSegment(sketch, "E403.trimOffspring", {"start": v(-339.11, -70.3) * mm, "end": v(-364.2, -96.12) * mm});
            skLineSegment(sketch, "E404.trimOffspring", {"start": v(-332.04, -77.37) * mm, "end": v(-357.13, -103.2) * mm});
            skLineSegment(sketch, "E405.trimOffspring", {"start": v(-274.52, -69.84) * mm, "end": v(-299.6, -95.66) * mm});
            skLineSegment(sketch, "E406.trimOffspring", {"start": v(-261.4, -68.82) * mm, "end": v(-235.94, -94.28) * mm});
            skLineSegment(sketch, "E407.trimOffspring", {"start": v(-268.37, -75.99) * mm, "end": v(-242.9, -101.45) * mm});
            skLineSegment(sketch, "E408.trimOffspring", {"start": v(-268.37, -75.99) * mm, "end": v(-293.46, -101.81) * mm});
            skLineSegment(sketch, "E409.trimOffspring", {"start": v(-242.9, -101.45) * mm, "end": v(-268, -127.27) * mm});
            skLineSegment(sketch, "E410.trimOffspring", {"start": v(-228.4, -101.81) * mm, "end": v(-202.45, -127.76) * mm});
            skLineSegment(sketch, "E411.trimOffspring", {"start": v(-235.37, -108.98) * mm, "end": v(-209.42, -134.94) * mm});
            skLineSegment(sketch, "E412.trimOffspring", {"start": v(-235.37, -108.98) * mm, "end": v(-260.46, -134.8) * mm});
            skLineSegment(sketch, "E413.trimOffspring", {"start": v(-177.36, -101.94) * mm, "end": v(-202.45, -127.76) * mm});
            skLineSegment(sketch, "E414.trimOffspring", {"start": v(-170.69, -108.62) * mm, "end": v(-145.23, -134.07) * mm});
            skLineSegment(sketch, "E415.trimOffspring", {"start": v(-163.72, -101.45) * mm, "end": v(-138.26, -126.9) * mm});
            skLineSegment(sketch, "E416.trimOffspring", {"start": v(-170.69, -108.62) * mm, "end": v(-195.78, -134.44) * mm});
            skLineSegment(sketch, "E417.trimOffspring", {"start": v(-106.66, -107.6) * mm, "end": v(-81.2, -133.05) * mm});
            skLineSegment(sketch, "E418.trimOffspring", {"start": v(-113.17, -101.08) * mm, "end": v(-138.26, -126.9) * mm});
            skLineSegment(sketch, "E419.trimOffspring", {"start": v(-99.69, -100.42) * mm, "end": v(-74.23, -125.88) * mm});
            skLineSegment(sketch, "E420.trimOffspring", {"start": v(-106.66, -107.6) * mm, "end": v(-131.75, -133.41) * mm});
            skLineSegment(sketch, "E421.trimOffspring", {"start": v(-79.3, -395.16) * mm, "end": v(-106.57, -423.22) * mm});
            skLineSegment(sketch, "E422.trimOffspring", {"start": v(-137.3, -337.17) * mm, "end": v(-111.84, -362.63) * mm});
            skLineSegment(sketch, "E423.trimOffspring", {"start": v(-196.61, -398.22) * mm, "end": v(-171.16, -423.68) * mm});
            skSolve(sketch);
        }
        {
            var Q0;
            Q0 = qSketchRegion(id + "F3", true);
            extrude(context, id + "F4", {"entities" : qUnion([Q0]), "depth" : 25 * mm, "offsetDistance" : 25 * mm});
        }
        {
            var Q0;
            Q0 = qSketchRegion(id + "F3", true);
            extrude(context, id + "F5", {"entities" : qUnion([Q0]), "operationType" : NewBodyOperationType.ADD, "depth" : 25 * mm, "offsetDistance" : 25 * mm});
        }
        {
            var Q0;
            Q0=qCreatedBy(makeId("Top.planeOp"),FACE);
            var sketch = newSketch(context, id + "F6", { "sketchPlane" : qUnion([Q0])});
            skLineSegment(sketch, "E424", {"start": v(0, 25) * mm, "end": v(-21.85, 12.15) * mm});
            skLineSegment(sketch, "E425", {"start": v(-21.85, 12.15) * mm, "end": v(-21.85, -12.15) * mm});
            skLineSegment(sketch, "E426", {"start": v(-21.85, -12.15) * mm, "end": v(0, -25) * mm});
            skLineSegment(sketch, "E427", {"start": v(0, -25) * mm, "end": v(21.85, -12.15) * mm});
            skLineSegment(sketch, "E428", {"start": v(21.85, -12.15) * mm, "end": v(21.85, 12.15) * mm});
            skLineSegment(sketch, "E429", {"start": v(21.85, 12.15) * mm, "end": v(0, 25) * mm});
            skLineSegment(sketch, "E430.MirrorCS", {"start": v(-75.58, -11.86) * mm, "end": v(-75.58, 12.44) * mm});
            skLineSegment(sketch, "E431.MirrorCS", {"start": v(-31.85, 12.44) * mm, "end": v(-31.85, -11.87) * mm});
            skLineSegment(sketch, "E432.MirrorCS", {"start": v(-53.72, -24.7) * mm, "end": v(-75.58, -11.86) * mm});
            skLineSegment(sketch, "E433.MirrorCS", {"start": v(-75.58, 12.44) * mm, "end": v(-53.73, 25.3) * mm});
            skLineSegment(sketch, "E434.MirrorCS", {"start": v(-31.85, -11.87) * mm, "end": v(-53.72, -24.7) * mm});
            skLineSegment(sketch, "E435.MirrorCS", {"start": v(-53.73, 25.3) * mm, "end": v(-31.85, 12.44) * mm});
            skLineSegment(sketch, "E436.MirrorCS", {"start": v(-129.48, -11.79) * mm, "end": v(-107.53, -24.7) * mm});
            skLineSegment(sketch, "E437.MirrorCS", {"start": v(-107.62, 25.36) * mm, "end": v(-129.48, 12.5) * mm});
            skLineSegment(sketch, "E438.MirrorCS", {"start": v(-183.18, 12.53) * mm, "end": v(-161.33, 25.38) * mm});
            skLineSegment(sketch, "E439.MirrorCS", {"start": v(-139.48, -11.77) * mm, "end": v(-161.33, -24.62) * mm});
            skLineSegment(sketch, "E440.MirrorCS", {"start": v(-161.33, -24.62) * mm, "end": v(-183.18, -11.77) * mm});
            skLineSegment(sketch, "E441.MirrorCS", {"start": v(-107.53, -24.7) * mm, "end": v(-85.58, -11.79) * mm});
            skLineSegment(sketch, "E442.MirrorCS", {"start": v(-139.48, 12.53) * mm, "end": v(-139.48, -11.77) * mm});
            skLineSegment(sketch, "E443.MirrorCS", {"start": v(-85.58, 12.5) * mm, "end": v(-107.62, 25.36) * mm});
            skLineSegment(sketch, "E444.MirrorCS", {"start": v(-129.48, 12.5) * mm, "end": v(-129.48, -11.79) * mm});
            skLineSegment(sketch, "E445.MirrorCS", {"start": v(-183.18, -11.77) * mm, "end": v(-183.18, 12.53) * mm});
            skLineSegment(sketch, "E446.MirrorCS", {"start": v(-161.33, 25.38) * mm, "end": v(-139.48, 12.53) * mm});
            skLineSegment(sketch, "E447.MirrorCS", {"start": v(-85.58, -11.79) * mm, "end": v(-85.58, 12.5) * mm});
            skLineSegment(sketch, "E448.MirrorCS", {"start": v(192.93, -13.27) * mm, "end": v(214.78, -26.12) * mm});
            skLineSegment(sketch, "E449.MirrorCS", {"start": v(161.08, -25.81) * mm, "end": v(139.23, -12.96) * mm});
            skLineSegment(sketch, "E450.MirrorCS", {"start": v(214.78, 23.88) * mm, "end": v(192.93, 11.03) * mm});
            skLineSegment(sketch, "E451.MirrorCS", {"start": v(85.53, -12.66) * mm, "end": v(107.38, -25.5) * mm});
            skLineSegment(sketch, "E452.MirrorCS", {"start": v(182.93, 11.33) * mm, "end": v(182.93, -12.96) * mm});
            skLineSegment(sketch, "E453.MirrorCS", {"start": v(139.23, -12.96) * mm, "end": v(139.23, 11.33) * mm});
            skLineSegment(sketch, "E454.MirrorCS", {"start": v(107.38, -25.5) * mm, "end": v(129.23, -12.66) * mm});
            skLineSegment(sketch, "E455.MirrorCS", {"start": v(139.23, 11.33) * mm, "end": v(161.08, 24.19) * mm});
            skLineSegment(sketch, "E456.MirrorCS", {"start": v(192.93, 11.03) * mm, "end": v(192.93, -13.27) * mm});
            skLineSegment(sketch, "E457.MirrorCS", {"start": v(129.23, 11.64) * mm, "end": v(107.38, 24.5) * mm});
            skLineSegment(sketch, "E458.MirrorCS", {"start": v(129.23, -12.66) * mm, "end": v(129.23, 11.64) * mm});
            skLineSegment(sketch, "E459.MirrorCS", {"start": v(85.53, 11.64) * mm, "end": v(85.53, -12.66) * mm});
            skLineSegment(sketch, "E460.MirrorCS", {"start": v(53.68, -25.2) * mm, "end": v(31.85, -12.3) * mm});
            skLineSegment(sketch, "E461.MirrorCS", {"start": v(31.85, -12.3) * mm, "end": v(31.85, 11.99) * mm});
            skLineSegment(sketch, "E462.MirrorCS", {"start": v(31.85, 11.99) * mm, "end": v(53.7, 24.84) * mm});
            skLineSegment(sketch, "E463.MirrorCS", {"start": v(53.7, 24.84) * mm, "end": v(75.53, 11.99) * mm});
            skLineSegment(sketch, "E464.MirrorCS", {"start": v(107.38, 24.5) * mm, "end": v(85.53, 11.64) * mm});
            skLineSegment(sketch, "E465.MirrorCS", {"start": v(182.93, -12.96) * mm, "end": v(161.08, -25.81) * mm});
            skLineSegment(sketch, "E466.MirrorCS", {"start": v(161.08, 24.19) * mm, "end": v(182.93, 11.33) * mm});
            skLineSegment(sketch, "E467.MirrorCS", {"start": v(75.53, -12.35) * mm, "end": v(53.68, -25.2) * mm});
            skLineSegment(sketch, "E468.MirrorCS", {"start": v(75.53, 11.99) * mm, "end": v(75.53, -12.35) * mm});
            skLineSegment(sketch, "E469.MirrorCS", {"start": v(-215.03, -24.62) * mm, "end": v(-193.18, -11.77) * mm});
            skLineSegment(sketch, "E470.MirrorCS", {"start": v(-193.18, 12.53) * mm, "end": v(-215.03, 25.38) * mm});
            skLineSegment(sketch, "E471.MirrorCS", {"start": v(-193.18, -11.77) * mm, "end": v(-193.18, 12.53) * mm});
            skLineSegment(sketch, "E472", {"start": v(26.71, -20.89) * mm, "end": v(4.82, -33.77) * mm});
            skLineSegment(sketch, "E473", {"start": v(4.82, -33.77) * mm, "end": v(4.82, -58.2) * mm});
            skLineSegment(sketch, "E474", {"start": v(4.82, -58.2) * mm, "end": v(26.5, -70.89) * mm});
            skLineSegment(sketch, "E475", {"start": v(26.5, -70.89) * mm, "end": v(48.52, -58.2) * mm});
            skLineSegment(sketch, "E476", {"start": v(48.52, -58.2) * mm, "end": v(48.52, -33.77) * mm});
            skLineSegment(sketch, "E477", {"start": v(48.52, -33.77) * mm, "end": v(26.71, -20.89) * mm});
            skLineSegment(sketch, "E478.MirrorCS", {"start": v(-48.88, -57.76) * mm, "end": v(-48.88, -33.46) * mm});
            skLineSegment(sketch, "E479.MirrorCS", {"start": v(-5.33, -33.46) * mm, "end": v(-5.18, -57.76) * mm});
            skLineSegment(sketch, "E480.MirrorCS", {"start": v(-27.03, -70.61) * mm, "end": v(-48.88, -57.76) * mm});
            skLineSegment(sketch, "E481.MirrorCS", {"start": v(-48.88, -33.46) * mm, "end": v(-27.09, -20.67) * mm});
            skLineSegment(sketch, "E482.MirrorCS", {"start": v(-5.18, -57.76) * mm, "end": v(-27.03, -70.61) * mm});
            skLineSegment(sketch, "E483.MirrorCS", {"start": v(-27.09, -20.67) * mm, "end": v(-5.33, -33.46) * mm});
            skLineSegment(sketch, "E484.MirrorCS", {"start": v(-102.47, -57.62) * mm, "end": v(-80.62, -70.47) * mm});
            skLineSegment(sketch, "E485.MirrorCS", {"start": v(-80.64, -20.48) * mm, "end": v(-102.47, -33.32) * mm});
            skLineSegment(sketch, "E486.MirrorCS", {"start": v(-156.33, -33.29) * mm, "end": v(-134.49, -20.44) * mm});
            skLineSegment(sketch, "E487.MirrorCS", {"start": v(-112.63, -57.58) * mm, "end": v(-134.48, -70.44) * mm});
            skLineSegment(sketch, "E488.MirrorCS", {"start": v(-134.48, -70.44) * mm, "end": v(-156.33, -57.58) * mm});
            skLineSegment(sketch, "E489.MirrorCS", {"start": v(-80.62, -70.47) * mm, "end": v(-58.77, -57.62) * mm});
            skLineSegment(sketch, "E490.MirrorCS", {"start": v(-112.64, -33.29) * mm, "end": v(-112.63, -57.58) * mm});
            skLineSegment(sketch, "E491.MirrorCS", {"start": v(-58.8, -33.32) * mm, "end": v(-80.64, -20.48) * mm});
            skLineSegment(sketch, "E492.MirrorCS", {"start": v(-102.47, -33.32) * mm, "end": v(-102.47, -57.62) * mm});
            skLineSegment(sketch, "E493.MirrorCS", {"start": v(-156.33, -57.58) * mm, "end": v(-156.33, -33.29) * mm});
            skLineSegment(sketch, "E494.MirrorCS", {"start": v(-134.49, -20.44) * mm, "end": v(-112.64, -33.29) * mm});
            skLineSegment(sketch, "E495.MirrorCS", {"start": v(-58.77, -57.62) * mm, "end": v(-58.8, -33.32) * mm});
            skLineSegment(sketch, "E496.MirrorCS", {"start": v(187.74, -71.73) * mm, "end": v(165.9, -58.88) * mm});
            skLineSegment(sketch, "E497.MirrorCS", {"start": v(112.2, -58.57) * mm, "end": v(134.04, -71.43) * mm});
            skLineSegment(sketch, "E498.MirrorCS", {"start": v(209.44, -34.58) * mm, "end": v(209.6, -58.88) * mm});
            skLineSegment(sketch, "E499.MirrorCS", {"start": v(165.9, -58.88) * mm, "end": v(165.9, -34.58) * mm});
            skLineSegment(sketch, "E500.MirrorCS", {"start": v(134.04, -71.43) * mm, "end": v(155.9, -58.57) * mm});
            skLineSegment(sketch, "E501.MirrorCS", {"start": v(165.9, -34.58) * mm, "end": v(187.67, -21.78) * mm});
            skLineSegment(sketch, "E502.MirrorCS", {"start": v(155.74, -34.28) * mm, "end": v(133.97, -21.47) * mm});
            skLineSegment(sketch, "E503.MirrorCS", {"start": v(155.9, -58.57) * mm, "end": v(155.74, -34.28) * mm});
            skLineSegment(sketch, "E504.MirrorCS", {"start": v(112.2, -34.28) * mm, "end": v(112.2, -58.57) * mm});
            skLineSegment(sketch, "E505.MirrorCS", {"start": v(80.34, -71.12) * mm, "end": v(58.5, -58.27) * mm});
            skLineSegment(sketch, "E506.MirrorCS", {"start": v(58.5, -58.27) * mm, "end": v(58.5, -33.97) * mm});
            skLineSegment(sketch, "E507.MirrorCS", {"start": v(58.5, -33.97) * mm, "end": v(80.27, -21.16) * mm});
            skLineSegment(sketch, "E508.MirrorCS", {"start": v(80.27, -21.16) * mm, "end": v(102.04, -33.97) * mm});
            skLineSegment(sketch, "E509.MirrorCS", {"start": v(133.97, -21.47) * mm, "end": v(112.2, -34.28) * mm});
            skLineSegment(sketch, "E510.MirrorCS", {"start": v(209.6, -58.88) * mm, "end": v(187.74, -71.73) * mm});
            skLineSegment(sketch, "E511.MirrorCS", {"start": v(187.67, -21.78) * mm, "end": v(209.44, -34.58) * mm});
            skLineSegment(sketch, "E512.MirrorCS", {"start": v(102.2, -58.27) * mm, "end": v(80.34, -71.12) * mm});
            skLineSegment(sketch, "E513.MirrorCS", {"start": v(102.04, -33.97) * mm, "end": v(102.2, -58.27) * mm});
            skLineSegment(sketch, "E514.MirrorCS", {"start": v(-188.18, -20.43) * mm, "end": v(-210.03, -33.28) * mm});
            skLineSegment(sketch, "E515.MirrorCS", {"start": v(-188.18, -70.43) * mm, "end": v(-166.33, -57.58) * mm});
            skLineSegment(sketch, "E516.MirrorCS", {"start": v(-166.33, -33.28) * mm, "end": v(-188.18, -20.43) * mm});
            skLineSegment(sketch, "E517.MirrorCS", {"start": v(-166.33, -57.58) * mm, "end": v(-166.33, -33.28) * mm});
            skLineSegment(sketch, "E518.MirrorCS", {"start": v(-210.03, -33.28) * mm, "end": v(-210.03, -57.58) * mm});
            skLineSegment(sketch, "E519.MirrorCS", {"start": v(-210.03, -57.58) * mm, "end": v(-188.18, -70.43) * mm});
            skLineSegment(sketch, "E520", {"start": v(0, -66.97) * mm, "end": v(-21.85, -79.82) * mm});
            skLineSegment(sketch, "E521", {"start": v(-21.85, -79.82) * mm, "end": v(-21.85, -104.12) * mm});
            skLineSegment(sketch, "E522", {"start": v(-21.85, -104.12) * mm, "end": v(0, -116.97) * mm});
            skLineSegment(sketch, "E523", {"start": v(0, -116.97) * mm, "end": v(21.85, -104.12) * mm});
            skLineSegment(sketch, "E524", {"start": v(21.85, -104.12) * mm, "end": v(21.85, -79.82) * mm});
            skLineSegment(sketch, "E525", {"start": v(21.85, -79.82) * mm, "end": v(0, -66.97) * mm});
            skLineSegment(sketch, "E526.MirrorCS", {"start": v(-75.58, -103.82) * mm, "end": v(-75.58, -79.53) * mm});
            skLineSegment(sketch, "E527.MirrorCS", {"start": v(-31.85, -79.53) * mm, "end": v(-31.85, -103.84) * mm});
            skLineSegment(sketch, "E528.MirrorCS", {"start": v(-53.72, -116.68) * mm, "end": v(-75.58, -103.82) * mm});
            skLineSegment(sketch, "E529.MirrorCS", {"start": v(-75.58, -79.53) * mm, "end": v(-53.73, -66.68) * mm});
            skLineSegment(sketch, "E530.MirrorCS", {"start": v(-31.85, -103.84) * mm, "end": v(-53.72, -116.68) * mm});
            skLineSegment(sketch, "E531.MirrorCS", {"start": v(-53.73, -66.68) * mm, "end": v(-31.85, -79.53) * mm});
            skLineSegment(sketch, "E532.MirrorCS", {"start": v(-129.48, -103.76) * mm, "end": v(-107.53, -116.66) * mm});
            skLineSegment(sketch, "E533.MirrorCS", {"start": v(-107.62, -66.6) * mm, "end": v(-129.48, -79.46) * mm});
            skLineSegment(sketch, "E534.MirrorCS", {"start": v(-183.18, -79.44) * mm, "end": v(-161.33, -66.6) * mm});
            skLineSegment(sketch, "E535.MirrorCS", {"start": v(-139.48, -103.74) * mm, "end": v(-161.33, -116.6) * mm});
            skLineSegment(sketch, "E536.MirrorCS", {"start": v(-161.33, -116.6) * mm, "end": v(-183.18, -103.74) * mm});
            skLineSegment(sketch, "E537.MirrorCS", {"start": v(-107.53, -116.66) * mm, "end": v(-85.58, -103.76) * mm});
            skLineSegment(sketch, "E538.MirrorCS", {"start": v(-139.48, -79.44) * mm, "end": v(-139.48, -103.74) * mm});
            skLineSegment(sketch, "E539.MirrorCS", {"start": v(-85.58, -79.46) * mm, "end": v(-107.62, -66.6) * mm});
            skLineSegment(sketch, "E540.MirrorCS", {"start": v(-129.48, -79.46) * mm, "end": v(-129.48, -103.76) * mm});
            skLineSegment(sketch, "E541.MirrorCS", {"start": v(-183.18, -103.74) * mm, "end": v(-183.18, -79.44) * mm});
            skLineSegment(sketch, "E542.MirrorCS", {"start": v(-161.33, -66.6) * mm, "end": v(-139.48, -79.44) * mm});
            skLineSegment(sketch, "E543.MirrorCS", {"start": v(-85.58, -103.76) * mm, "end": v(-85.58, -79.46) * mm});
            skLineSegment(sketch, "E544.MirrorCS", {"start": v(192.93, -105.24) * mm, "end": v(214.78, -118.09) * mm});
            skLineSegment(sketch, "E545.MirrorCS", {"start": v(161.08, -117.78) * mm, "end": v(139.23, -104.93) * mm});
            skLineSegment(sketch, "E546.MirrorCS", {"start": v(214.78, -68.09) * mm, "end": v(192.93, -80.94) * mm});
            skLineSegment(sketch, "E547.MirrorCS", {"start": v(85.53, -104.62) * mm, "end": v(107.38, -117.48) * mm});
            skLineSegment(sketch, "E548.MirrorCS", {"start": v(182.93, -80.63) * mm, "end": v(182.93, -104.93) * mm});
            skLineSegment(sketch, "E549.MirrorCS", {"start": v(139.23, -104.93) * mm, "end": v(139.23, -80.63) * mm});
            skLineSegment(sketch, "E550.MirrorCS", {"start": v(107.38, -117.48) * mm, "end": v(129.23, -104.62) * mm});
            skLineSegment(sketch, "E551.MirrorCS", {"start": v(139.23, -80.63) * mm, "end": v(161.08, -67.78) * mm});
            skLineSegment(sketch, "E552.MirrorCS", {"start": v(192.93, -80.94) * mm, "end": v(192.93, -105.24) * mm});
            skLineSegment(sketch, "E553.MirrorCS", {"start": v(129.23, -80.33) * mm, "end": v(107.38, -67.48) * mm});
            skLineSegment(sketch, "E554.MirrorCS", {"start": v(129.23, -104.62) * mm, "end": v(129.23, -80.33) * mm});
            skLineSegment(sketch, "E555.MirrorCS", {"start": v(85.53, -80.33) * mm, "end": v(85.53, -104.62) * mm});
            skLineSegment(sketch, "E556.MirrorCS", {"start": v(53.68, -117.17) * mm, "end": v(31.85, -104.28) * mm});
            skLineSegment(sketch, "E557.MirrorCS", {"start": v(31.85, -104.28) * mm, "end": v(31.85, -79.98) * mm});
            skLineSegment(sketch, "E558.MirrorCS", {"start": v(31.85, -79.98) * mm, "end": v(53.7, -67.13) * mm});
            skLineSegment(sketch, "E559.MirrorCS", {"start": v(53.7, -67.13) * mm, "end": v(75.53, -79.98) * mm});
            skLineSegment(sketch, "E560.MirrorCS", {"start": v(107.38, -67.48) * mm, "end": v(85.53, -80.33) * mm});
            skLineSegment(sketch, "E561.MirrorCS", {"start": v(182.93, -104.93) * mm, "end": v(161.08, -117.78) * mm});
            skLineSegment(sketch, "E562.MirrorCS", {"start": v(161.08, -67.78) * mm, "end": v(182.93, -80.63) * mm});
            skLineSegment(sketch, "E563.MirrorCS", {"start": v(75.53, -104.32) * mm, "end": v(53.68, -117.17) * mm});
            skLineSegment(sketch, "E564.MirrorCS", {"start": v(75.53, -79.98) * mm, "end": v(75.53, -104.32) * mm});
            skLineSegment(sketch, "E565.MirrorCS", {"start": v(-215.03, -116.59) * mm, "end": v(-193.18, -103.74) * mm});
            skLineSegment(sketch, "E566.MirrorCS", {"start": v(-193.18, -79.44) * mm, "end": v(-215.03, -66.59) * mm});
            skLineSegment(sketch, "E567.MirrorCS", {"start": v(-193.18, -103.74) * mm, "end": v(-193.18, -79.44) * mm});
            skLineSegment(sketch, "E568", {"start": v(26.71, -112.86) * mm, "end": v(4.82, -125.74) * mm});
            skLineSegment(sketch, "E569", {"start": v(4.82, -125.74) * mm, "end": v(4.82, -150.03) * mm});
            skLineSegment(sketch, "E570", {"start": v(4.82, -150.03) * mm, "end": v(26.5, -162.86) * mm});
            skLineSegment(sketch, "E571", {"start": v(26.5, -162.86) * mm, "end": v(48.52, -150.03) * mm});
            skLineSegment(sketch, "E572", {"start": v(48.52, -150.03) * mm, "end": v(48.52, -125.74) * mm});
            skLineSegment(sketch, "E573", {"start": v(48.52, -125.74) * mm, "end": v(26.71, -112.86) * mm});
            skLineSegment(sketch, "E574.MirrorCS", {"start": v(-48.88, -149.73) * mm, "end": v(-48.88, -125.43) * mm});
            skLineSegment(sketch, "E575.MirrorCS", {"start": v(-5.33, -125.43) * mm, "end": v(-5.18, -149.73) * mm});
            skLineSegment(sketch, "E576.MirrorCS", {"start": v(-27.03, -162.58) * mm, "end": v(-48.88, -149.73) * mm});
            skLineSegment(sketch, "E577.MirrorCS", {"start": v(-48.88, -125.43) * mm, "end": v(-27.09, -112.64) * mm});
            skLineSegment(sketch, "E578.MirrorCS", {"start": v(-5.18, -149.73) * mm, "end": v(-27.03, -162.58) * mm});
            skLineSegment(sketch, "E579.MirrorCS", {"start": v(-27.09, -112.64) * mm, "end": v(-5.33, -125.43) * mm});
            skLineSegment(sketch, "E580.MirrorCS", {"start": v(-102.47, -149.59) * mm, "end": v(-80.62, -162.44) * mm});
            skLineSegment(sketch, "E581.MirrorCS", {"start": v(-80.64, -112.45) * mm, "end": v(-102.47, -125.3) * mm});
            skLineSegment(sketch, "E582.MirrorCS", {"start": v(-156.33, -125.26) * mm, "end": v(-134.49, -112.4) * mm});
            skLineSegment(sketch, "E583.MirrorCS", {"start": v(-112.63, -149.55) * mm, "end": v(-134.48, -162.4) * mm});
            skLineSegment(sketch, "E584.MirrorCS", {"start": v(-134.48, -162.4) * mm, "end": v(-156.33, -149.55) * mm});
            skLineSegment(sketch, "E585.MirrorCS", {"start": v(-80.62, -162.44) * mm, "end": v(-58.77, -149.59) * mm});
            skLineSegment(sketch, "E586.MirrorCS", {"start": v(-112.64, -125.26) * mm, "end": v(-112.63, -149.55) * mm});
            skLineSegment(sketch, "E587.MirrorCS", {"start": v(-58.8, -125.29) * mm, "end": v(-80.64, -112.45) * mm});
            skLineSegment(sketch, "E588.MirrorCS", {"start": v(-102.47, -125.3) * mm, "end": v(-102.47, -149.59) * mm});
            skLineSegment(sketch, "E589.MirrorCS", {"start": v(-156.33, -149.55) * mm, "end": v(-156.33, -125.26) * mm});
            skLineSegment(sketch, "E590.MirrorCS", {"start": v(-134.49, -112.4) * mm, "end": v(-112.64, -125.26) * mm});
            skLineSegment(sketch, "E591.MirrorCS", {"start": v(-58.77, -149.59) * mm, "end": v(-58.8, -125.29) * mm});
            skLineSegment(sketch, "E592.MirrorCS", {"start": v(187.74, -163.7) * mm, "end": v(165.9, -150.85) * mm});
            skLineSegment(sketch, "E593.MirrorCS", {"start": v(112.2, -150.54) * mm, "end": v(134.04, -163.4) * mm});
            skLineSegment(sketch, "E594.MirrorCS", {"start": v(209.44, -126.55) * mm, "end": v(209.6, -150.85) * mm});
            skLineSegment(sketch, "E595.MirrorCS", {"start": v(165.9, -150.85) * mm, "end": v(165.9, -126.55) * mm});
            skLineSegment(sketch, "E596.MirrorCS", {"start": v(134.04, -163.4) * mm, "end": v(155.9, -150.54) * mm});
            skLineSegment(sketch, "E597.MirrorCS", {"start": v(165.9, -126.55) * mm, "end": v(187.67, -113.74) * mm});
            skLineSegment(sketch, "E598.MirrorCS", {"start": v(155.74, -126.25) * mm, "end": v(133.97, -113.44) * mm});
            skLineSegment(sketch, "E599.MirrorCS", {"start": v(155.9, -150.54) * mm, "end": v(155.74, -126.25) * mm});
            skLineSegment(sketch, "E600.MirrorCS", {"start": v(112.2, -126.25) * mm, "end": v(112.2, -150.54) * mm});
            skLineSegment(sketch, "E601.MirrorCS", {"start": v(80.34, -163.09) * mm, "end": v(58.5, -150.24) * mm});
            skLineSegment(sketch, "E602.MirrorCS", {"start": v(58.5, -150.24) * mm, "end": v(58.5, -125.94) * mm});
            skLineSegment(sketch, "E603.MirrorCS", {"start": v(58.5, -125.94) * mm, "end": v(80.27, -113.13) * mm});
            skLineSegment(sketch, "E604.MirrorCS", {"start": v(80.27, -113.13) * mm, "end": v(102.04, -125.94) * mm});
            skLineSegment(sketch, "E605.MirrorCS", {"start": v(133.97, -113.44) * mm, "end": v(112.2, -126.25) * mm});
            skLineSegment(sketch, "E606.MirrorCS", {"start": v(209.6, -150.85) * mm, "end": v(187.74, -163.7) * mm});
            skLineSegment(sketch, "E607.MirrorCS", {"start": v(187.67, -113.74) * mm, "end": v(209.44, -126.55) * mm});
            skLineSegment(sketch, "E608.MirrorCS", {"start": v(102.2, -150.24) * mm, "end": v(80.34, -163.09) * mm});
            skLineSegment(sketch, "E609.MirrorCS", {"start": v(102.04, -125.94) * mm, "end": v(102.2, -150.24) * mm});
            skLineSegment(sketch, "E610.MirrorCS", {"start": v(-188.18, -112.4) * mm, "end": v(-210.03, -125.25) * mm});
            skLineSegment(sketch, "E611.MirrorCS", {"start": v(-188.18, -162.4) * mm, "end": v(-166.33, -149.55) * mm});
            skLineSegment(sketch, "E612.MirrorCS", {"start": v(-166.33, -125.25) * mm, "end": v(-188.18, -112.4) * mm});
            skLineSegment(sketch, "E613.MirrorCS", {"start": v(-166.33, -149.55) * mm, "end": v(-166.33, -125.25) * mm});
            skLineSegment(sketch, "E614.MirrorCS", {"start": v(-210.03, -125.25) * mm, "end": v(-210.03, -149.55) * mm});
            skLineSegment(sketch, "E615.MirrorCS", {"start": v(-210.03, -149.55) * mm, "end": v(-188.18, -162.4) * mm});
            skLineSegment(sketch, "E616", {"start": v(0, 208.63) * mm, "end": v(-21.85, 195.78) * mm});
            skLineSegment(sketch, "E617", {"start": v(-21.85, 195.78) * mm, "end": v(-21.85, 171.49) * mm});
            skLineSegment(sketch, "E618", {"start": v(-21.85, 171.49) * mm, "end": v(0, 158.63) * mm});
            skLineSegment(sketch, "E619", {"start": v(0, 158.63) * mm, "end": v(21.85, 171.49) * mm});
            skLineSegment(sketch, "E620", {"start": v(21.85, 171.49) * mm, "end": v(21.85, 195.78) * mm});
            skLineSegment(sketch, "E621", {"start": v(21.85, 195.78) * mm, "end": v(0, 208.63) * mm});
            skLineSegment(sketch, "E622.MirrorCS", {"start": v(-75.58, 171.78) * mm, "end": v(-75.58, 196.08) * mm});
            skLineSegment(sketch, "E623.MirrorCS", {"start": v(-31.85, 196.08) * mm, "end": v(-31.85, 171.77) * mm});
            skLineSegment(sketch, "E624.MirrorCS", {"start": v(-53.72, 158.93) * mm, "end": v(-75.58, 171.78) * mm});
            skLineSegment(sketch, "E625.MirrorCS", {"start": v(-75.58, 196.08) * mm, "end": v(-53.73, 208.93) * mm});
            skLineSegment(sketch, "E626.MirrorCS", {"start": v(-31.85, 171.77) * mm, "end": v(-53.72, 158.93) * mm});
            skLineSegment(sketch, "E627.MirrorCS", {"start": v(-53.73, 208.93) * mm, "end": v(-31.85, 196.08) * mm});
            skLineSegment(sketch, "E628.MirrorCS", {"start": v(-129.48, 171.85) * mm, "end": v(-107.53, 158.94) * mm});
            skLineSegment(sketch, "E629.MirrorCS", {"start": v(-107.62, 209) * mm, "end": v(-129.48, 196.14) * mm});
            skLineSegment(sketch, "E630.MirrorCS", {"start": v(-183.18, 196.16) * mm, "end": v(-161.33, 209.01) * mm});
            skLineSegment(sketch, "E631.MirrorCS", {"start": v(-139.48, 171.86) * mm, "end": v(-161.33, 159.01) * mm});
            skLineSegment(sketch, "E632.MirrorCS", {"start": v(-161.33, 159.01) * mm, "end": v(-183.18, 171.86) * mm});
            skLineSegment(sketch, "E633.MirrorCS", {"start": v(-107.53, 158.94) * mm, "end": v(-85.58, 171.85) * mm});
            skLineSegment(sketch, "E634.MirrorCS", {"start": v(-139.48, 196.16) * mm, "end": v(-139.48, 171.86) * mm});
            skLineSegment(sketch, "E635.MirrorCS", {"start": v(-85.58, 196.14) * mm, "end": v(-107.62, 209) * mm});
            skLineSegment(sketch, "E636.MirrorCS", {"start": v(-129.48, 196.14) * mm, "end": v(-129.48, 171.85) * mm});
            skLineSegment(sketch, "E637.MirrorCS", {"start": v(-183.18, 171.86) * mm, "end": v(-183.18, 196.16) * mm});
            skLineSegment(sketch, "E638.MirrorCS", {"start": v(-161.33, 209.01) * mm, "end": v(-139.48, 196.16) * mm});
            skLineSegment(sketch, "E639.MirrorCS", {"start": v(-85.58, 171.85) * mm, "end": v(-85.58, 196.14) * mm});
            skLineSegment(sketch, "E640.MirrorCS", {"start": v(192.93, 170.37) * mm, "end": v(214.78, 157.52) * mm});
            skLineSegment(sketch, "E641.MirrorCS", {"start": v(161.08, 157.82) * mm, "end": v(139.23, 170.67) * mm});
            skLineSegment(sketch, "E642.MirrorCS", {"start": v(214.78, 207.52) * mm, "end": v(192.93, 194.66) * mm});
            skLineSegment(sketch, "E643.MirrorCS", {"start": v(85.53, 170.98) * mm, "end": v(107.38, 158.13) * mm});
            skLineSegment(sketch, "E644.MirrorCS", {"start": v(182.93, 194.97) * mm, "end": v(182.93, 170.67) * mm});
            skLineSegment(sketch, "E645.MirrorCS", {"start": v(139.23, 170.67) * mm, "end": v(139.23, 194.97) * mm});
            skLineSegment(sketch, "E646.MirrorCS", {"start": v(107.38, 158.13) * mm, "end": v(129.23, 170.98) * mm});
            skLineSegment(sketch, "E647.MirrorCS", {"start": v(139.23, 194.97) * mm, "end": v(161.08, 207.82) * mm});
            skLineSegment(sketch, "E648.MirrorCS", {"start": v(192.93, 194.66) * mm, "end": v(192.93, 170.37) * mm});
            skLineSegment(sketch, "E649.MirrorCS", {"start": v(129.23, 195.27) * mm, "end": v(107.38, 208.13) * mm});
            skLineSegment(sketch, "E650.MirrorCS", {"start": v(129.23, 170.98) * mm, "end": v(129.23, 195.27) * mm});
            skLineSegment(sketch, "E651.MirrorCS", {"start": v(85.53, 195.27) * mm, "end": v(85.53, 170.98) * mm});
            skLineSegment(sketch, "E652.MirrorCS", {"start": v(53.68, 158.43) * mm, "end": v(31.85, 171.33) * mm});
            skLineSegment(sketch, "E653.MirrorCS", {"start": v(31.85, 171.33) * mm, "end": v(31.85, 195.62) * mm});
            skLineSegment(sketch, "E654.MirrorCS", {"start": v(31.85, 195.62) * mm, "end": v(53.7, 208.47) * mm});
            skLineSegment(sketch, "E655.MirrorCS", {"start": v(53.7, 208.47) * mm, "end": v(75.53, 195.62) * mm});
            skLineSegment(sketch, "E656.MirrorCS", {"start": v(107.38, 208.13) * mm, "end": v(85.53, 195.27) * mm});
            skLineSegment(sketch, "E657.MirrorCS", {"start": v(182.93, 170.67) * mm, "end": v(161.08, 157.82) * mm});
            skLineSegment(sketch, "E658.MirrorCS", {"start": v(161.08, 207.82) * mm, "end": v(182.93, 194.97) * mm});
            skLineSegment(sketch, "E659.MirrorCS", {"start": v(75.53, 171.28) * mm, "end": v(53.68, 158.43) * mm});
            skLineSegment(sketch, "E660.MirrorCS", {"start": v(75.53, 195.62) * mm, "end": v(75.53, 171.28) * mm});
            skLineSegment(sketch, "E661.MirrorCS", {"start": v(-215.03, 159.02) * mm, "end": v(-193.18, 171.87) * mm});
            skLineSegment(sketch, "E662.MirrorCS", {"start": v(-193.18, 196.16) * mm, "end": v(-215.03, 209.02) * mm});
            skLineSegment(sketch, "E663.MirrorCS", {"start": v(-193.18, 171.87) * mm, "end": v(-193.18, 196.16) * mm});
            skLineSegment(sketch, "E664", {"start": v(26.71, 162.75) * mm, "end": v(4.82, 149.87) * mm});
            skLineSegment(sketch, "E665", {"start": v(4.82, 149.87) * mm, "end": v(4.82, 125.44) * mm});
            skLineSegment(sketch, "E666", {"start": v(4.82, 125.44) * mm, "end": v(26.5, 112.75) * mm});
            skLineSegment(sketch, "E667", {"start": v(26.5, 112.75) * mm, "end": v(48.52, 125.44) * mm});
            skLineSegment(sketch, "E668", {"start": v(48.52, 125.44) * mm, "end": v(48.52, 149.87) * mm});
            skLineSegment(sketch, "E669", {"start": v(48.52, 149.87) * mm, "end": v(26.71, 162.75) * mm});
            skLineSegment(sketch, "E670.MirrorCS", {"start": v(-48.88, 125.88) * mm, "end": v(-48.88, 150.17) * mm});
            skLineSegment(sketch, "E671.MirrorCS", {"start": v(-5.33, 150.17) * mm, "end": v(-5.18, 125.88) * mm});
            skLineSegment(sketch, "E672.MirrorCS", {"start": v(-27.03, 113.02) * mm, "end": v(-48.88, 125.88) * mm});
            skLineSegment(sketch, "E673.MirrorCS", {"start": v(-48.88, 150.17) * mm, "end": v(-27.09, 162.97) * mm});
            skLineSegment(sketch, "E674.MirrorCS", {"start": v(-5.18, 125.88) * mm, "end": v(-27.03, 113.02) * mm});
            skLineSegment(sketch, "E675.MirrorCS", {"start": v(-27.09, 162.97) * mm, "end": v(-5.33, 150.17) * mm});
            skLineSegment(sketch, "E676.MirrorCS", {"start": v(-102.47, 126.02) * mm, "end": v(-80.62, 113.16) * mm});
            skLineSegment(sketch, "E677.MirrorCS", {"start": v(-80.64, 163.15) * mm, "end": v(-102.47, 150.31) * mm});
            skLineSegment(sketch, "E678.MirrorCS", {"start": v(-156.33, 150.35) * mm, "end": v(-134.49, 163.2) * mm});
            skLineSegment(sketch, "E679.MirrorCS", {"start": v(-112.63, 126.05) * mm, "end": v(-134.48, 113.2) * mm});
            skLineSegment(sketch, "E680.MirrorCS", {"start": v(-134.48, 113.2) * mm, "end": v(-156.33, 126.05) * mm});
            skLineSegment(sketch, "E681.MirrorCS", {"start": v(-80.62, 113.16) * mm, "end": v(-58.77, 126.02) * mm});
            skLineSegment(sketch, "E682.MirrorCS", {"start": v(-112.64, 150.35) * mm, "end": v(-112.63, 126.05) * mm});
            skLineSegment(sketch, "E683.MirrorCS", {"start": v(-58.8, 150.32) * mm, "end": v(-80.64, 163.15) * mm});
            skLineSegment(sketch, "E684.MirrorCS", {"start": v(-102.47, 150.31) * mm, "end": v(-102.47, 126.02) * mm});
            skLineSegment(sketch, "E685.MirrorCS", {"start": v(-156.33, 126.05) * mm, "end": v(-156.33, 150.35) * mm});
            skLineSegment(sketch, "E686.MirrorCS", {"start": v(-134.49, 163.2) * mm, "end": v(-112.64, 150.35) * mm});
            skLineSegment(sketch, "E687.MirrorCS", {"start": v(-58.77, 126.02) * mm, "end": v(-58.8, 150.32) * mm});
            skLineSegment(sketch, "E688.MirrorCS", {"start": v(187.74, 111.9) * mm, "end": v(165.9, 124.76) * mm});
            skLineSegment(sketch, "E689.MirrorCS", {"start": v(112.2, 125.06) * mm, "end": v(134.04, 112.2) * mm});
            skLineSegment(sketch, "E690.MirrorCS", {"start": v(209.44, 149.05) * mm, "end": v(209.6, 124.76) * mm});
            skLineSegment(sketch, "E691.MirrorCS", {"start": v(165.9, 124.76) * mm, "end": v(165.9, 149.05) * mm});
            skLineSegment(sketch, "E692.MirrorCS", {"start": v(134.04, 112.2) * mm, "end": v(155.9, 125.06) * mm});
            skLineSegment(sketch, "E693.MirrorCS", {"start": v(165.9, 149.05) * mm, "end": v(187.67, 161.86) * mm});
            skLineSegment(sketch, "E694.MirrorCS", {"start": v(155.74, 149.36) * mm, "end": v(133.97, 162.17) * mm});
            skLineSegment(sketch, "E695.MirrorCS", {"start": v(155.9, 125.06) * mm, "end": v(155.74, 149.36) * mm});
            skLineSegment(sketch, "E696.MirrorCS", {"start": v(112.2, 149.36) * mm, "end": v(112.2, 125.06) * mm});
            skLineSegment(sketch, "E697.MirrorCS", {"start": v(80.34, 112.51) * mm, "end": v(58.5, 125.37) * mm});
            skLineSegment(sketch, "E698.MirrorCS", {"start": v(58.5, 125.37) * mm, "end": v(58.5, 149.66) * mm});
            skLineSegment(sketch, "E699.MirrorCS", {"start": v(58.5, 149.66) * mm, "end": v(80.27, 162.47) * mm});
            skLineSegment(sketch, "E700.MirrorCS", {"start": v(80.27, 162.47) * mm, "end": v(102.04, 149.66) * mm});
            skLineSegment(sketch, "E701.MirrorCS", {"start": v(133.97, 162.17) * mm, "end": v(112.2, 149.36) * mm});
            skLineSegment(sketch, "E702.MirrorCS", {"start": v(209.6, 124.76) * mm, "end": v(187.74, 111.9) * mm});
            skLineSegment(sketch, "E703.MirrorCS", {"start": v(187.67, 161.86) * mm, "end": v(209.44, 149.05) * mm});
            skLineSegment(sketch, "E704.MirrorCS", {"start": v(102.2, 125.37) * mm, "end": v(80.34, 112.51) * mm});
            skLineSegment(sketch, "E705.MirrorCS", {"start": v(102.04, 149.66) * mm, "end": v(102.2, 125.37) * mm});
            skLineSegment(sketch, "E706.MirrorCS", {"start": v(-188.18, 163.2) * mm, "end": v(-210.03, 150.35) * mm});
            skLineSegment(sketch, "E707.MirrorCS", {"start": v(-188.18, 113.2) * mm, "end": v(-166.33, 126.06) * mm});
            skLineSegment(sketch, "E708.MirrorCS", {"start": v(-166.33, 150.35) * mm, "end": v(-188.18, 163.2) * mm});
            skLineSegment(sketch, "E709.MirrorCS", {"start": v(-166.33, 126.06) * mm, "end": v(-166.33, 150.35) * mm});
            skLineSegment(sketch, "E710.MirrorCS", {"start": v(-210.03, 150.35) * mm, "end": v(-210.03, 126.06) * mm});
            skLineSegment(sketch, "E711.MirrorCS", {"start": v(-210.03, 126.06) * mm, "end": v(-188.18, 113.2) * mm});
            skLineSegment(sketch, "E712", {"start": v(0, 116.67) * mm, "end": v(-21.85, 103.81) * mm});
            skLineSegment(sketch, "E713", {"start": v(-21.85, 103.81) * mm, "end": v(-21.85, 79.52) * mm});
            skLineSegment(sketch, "E714", {"start": v(-21.85, 79.52) * mm, "end": v(0, 66.67) * mm});
            skLineSegment(sketch, "E715", {"start": v(0, 66.67) * mm, "end": v(21.85, 79.52) * mm});
            skLineSegment(sketch, "E716", {"start": v(21.85, 79.52) * mm, "end": v(21.85, 103.81) * mm});
            skLineSegment(sketch, "E717", {"start": v(21.85, 103.81) * mm, "end": v(0, 116.67) * mm});
            skLineSegment(sketch, "E718.MirrorCS", {"start": v(-75.58, 79.81) * mm, "end": v(-75.58, 104.1) * mm});
            skLineSegment(sketch, "E719.MirrorCS", {"start": v(-31.85, 104.1) * mm, "end": v(-31.85, 79.8) * mm});
            skLineSegment(sketch, "E720.MirrorCS", {"start": v(-53.72, 66.96) * mm, "end": v(-75.58, 79.81) * mm});
            skLineSegment(sketch, "E721.MirrorCS", {"start": v(-75.58, 104.1) * mm, "end": v(-53.73, 116.96) * mm});
            skLineSegment(sketch, "E722.MirrorCS", {"start": v(-31.85, 79.8) * mm, "end": v(-53.72, 66.96) * mm});
            skLineSegment(sketch, "E723.MirrorCS", {"start": v(-53.73, 116.96) * mm, "end": v(-31.85, 104.1) * mm});
            skLineSegment(sketch, "E724.MirrorCS", {"start": v(-129.48, 79.88) * mm, "end": v(-107.53, 66.97) * mm});
            skLineSegment(sketch, "E725.MirrorCS", {"start": v(-107.62, 117.03) * mm, "end": v(-129.48, 104.18) * mm});
            skLineSegment(sketch, "E726.MirrorCS", {"start": v(-183.18, 104.2) * mm, "end": v(-161.33, 117.04) * mm});
            skLineSegment(sketch, "E727.MirrorCS", {"start": v(-139.48, 79.9) * mm, "end": v(-161.33, 67.04) * mm});
            skLineSegment(sketch, "E728.MirrorCS", {"start": v(-161.33, 67.04) * mm, "end": v(-183.18, 79.9) * mm});
            skLineSegment(sketch, "E729.MirrorCS", {"start": v(-107.53, 66.97) * mm, "end": v(-85.58, 79.88) * mm});
            skLineSegment(sketch, "E730.MirrorCS", {"start": v(-139.48, 104.2) * mm, "end": v(-139.48, 79.9) * mm});
            skLineSegment(sketch, "E731.MirrorCS", {"start": v(-85.58, 104.18) * mm, "end": v(-107.62, 117.03) * mm});
            skLineSegment(sketch, "E732.MirrorCS", {"start": v(-129.48, 104.18) * mm, "end": v(-129.48, 79.88) * mm});
            skLineSegment(sketch, "E733.MirrorCS", {"start": v(-183.18, 79.9) * mm, "end": v(-183.18, 104.2) * mm});
            skLineSegment(sketch, "E734.MirrorCS", {"start": v(-161.33, 117.04) * mm, "end": v(-139.48, 104.2) * mm});
            skLineSegment(sketch, "E735.MirrorCS", {"start": v(-85.58, 79.88) * mm, "end": v(-85.58, 104.18) * mm});
            skLineSegment(sketch, "E736.MirrorCS", {"start": v(192.93, 78.4) * mm, "end": v(214.78, 65.55) * mm});
            skLineSegment(sketch, "E737.MirrorCS", {"start": v(161.08, 65.85) * mm, "end": v(139.23, 78.7) * mm});
            skLineSegment(sketch, "E738.MirrorCS", {"start": v(214.78, 115.55) * mm, "end": v(192.93, 102.7) * mm});
            skLineSegment(sketch, "E739.MirrorCS", {"start": v(85.53, 79.01) * mm, "end": v(107.38, 66.16) * mm});
            skLineSegment(sketch, "E740.MirrorCS", {"start": v(182.93, 103) * mm, "end": v(182.93, 78.7) * mm});
            skLineSegment(sketch, "E741.MirrorCS", {"start": v(139.23, 78.7) * mm, "end": v(139.23, 103) * mm});
            skLineSegment(sketch, "E742.MirrorCS", {"start": v(107.38, 66.16) * mm, "end": v(129.23, 79.01) * mm});
            skLineSegment(sketch, "E743.MirrorCS", {"start": v(139.23, 103) * mm, "end": v(161.08, 115.85) * mm});
            skLineSegment(sketch, "E744.MirrorCS", {"start": v(192.93, 102.7) * mm, "end": v(192.93, 78.4) * mm});
            skLineSegment(sketch, "E745.MirrorCS", {"start": v(129.23, 103.3) * mm, "end": v(107.38, 116.16) * mm});
            skLineSegment(sketch, "E746.MirrorCS", {"start": v(129.23, 79.01) * mm, "end": v(129.23, 103.3) * mm});
            skLineSegment(sketch, "E747.MirrorCS", {"start": v(85.53, 103.3) * mm, "end": v(85.53, 79.01) * mm});
            skLineSegment(sketch, "E748.MirrorCS", {"start": v(53.68, 66.46) * mm, "end": v(31.85, 79.36) * mm});
            skLineSegment(sketch, "E749.MirrorCS", {"start": v(31.85, 79.36) * mm, "end": v(31.85, 103.65) * mm});
            skLineSegment(sketch, "E750.MirrorCS", {"start": v(31.85, 103.65) * mm, "end": v(53.7, 116.5) * mm});
            skLineSegment(sketch, "E751.MirrorCS", {"start": v(53.7, 116.5) * mm, "end": v(75.53, 103.65) * mm});
            skLineSegment(sketch, "E752.MirrorCS", {"start": v(107.38, 116.16) * mm, "end": v(85.53, 103.3) * mm});
            skLineSegment(sketch, "E753.MirrorCS", {"start": v(182.93, 78.7) * mm, "end": v(161.08, 65.85) * mm});
            skLineSegment(sketch, "E754.MirrorCS", {"start": v(161.08, 115.85) * mm, "end": v(182.93, 103) * mm});
            skLineSegment(sketch, "E755.MirrorCS", {"start": v(75.53, 79.32) * mm, "end": v(53.68, 66.46) * mm});
            skLineSegment(sketch, "E756.MirrorCS", {"start": v(75.53, 103.65) * mm, "end": v(75.53, 79.32) * mm});
            skLineSegment(sketch, "E757.MirrorCS", {"start": v(-215.03, 67.05) * mm, "end": v(-193.18, 79.9) * mm});
            skLineSegment(sketch, "E758.MirrorCS", {"start": v(-193.18, 104.2) * mm, "end": v(-215.03, 117.05) * mm});
            skLineSegment(sketch, "E759.MirrorCS", {"start": v(-193.18, 79.9) * mm, "end": v(-193.18, 104.2) * mm});
            skLineSegment(sketch, "E760", {"start": v(26.71, 70.78) * mm, "end": v(4.82, 57.9) * mm});
            skLineSegment(sketch, "E761", {"start": v(4.82, 57.9) * mm, "end": v(4.82, 33.6) * mm});
            skLineSegment(sketch, "E762", {"start": v(4.82, 33.6) * mm, "end": v(26.5, 20.78) * mm});
            skLineSegment(sketch, "E763", {"start": v(26.5, 20.78) * mm, "end": v(48.52, 33.6) * mm});
            skLineSegment(sketch, "E764", {"start": v(48.52, 33.6) * mm, "end": v(48.52, 57.9) * mm});
            skLineSegment(sketch, "E765", {"start": v(48.52, 57.9) * mm, "end": v(26.71, 70.78) * mm});
            skLineSegment(sketch, "E766.MirrorCS", {"start": v(-48.88, 33.9) * mm, "end": v(-48.88, 58.2) * mm});
            skLineSegment(sketch, "E767.MirrorCS", {"start": v(-5.33, 58.2) * mm, "end": v(-5.18, 33.9) * mm});
            skLineSegment(sketch, "E768.MirrorCS", {"start": v(-27.03, 21.05) * mm, "end": v(-48.88, 33.9) * mm});
            skLineSegment(sketch, "E769.MirrorCS", {"start": v(-48.88, 58.2) * mm, "end": v(-27.09, 71) * mm});
            skLineSegment(sketch, "E770.MirrorCS", {"start": v(-5.18, 33.9) * mm, "end": v(-27.03, 21.05) * mm});
            skLineSegment(sketch, "E771.MirrorCS", {"start": v(-27.09, 71) * mm, "end": v(-5.33, 58.2) * mm});
            skLineSegment(sketch, "E772.MirrorCS", {"start": v(-102.47, 34.05) * mm, "end": v(-80.62, 21.2) * mm});
            skLineSegment(sketch, "E773.MirrorCS", {"start": v(-80.64, 71.18) * mm, "end": v(-102.47, 58.34) * mm});
            skLineSegment(sketch, "E774.MirrorCS", {"start": v(-156.33, 58.38) * mm, "end": v(-134.49, 71.23) * mm});
            skLineSegment(sketch, "E775.MirrorCS", {"start": v(-112.63, 34.08) * mm, "end": v(-134.48, 21.23) * mm});
            skLineSegment(sketch, "E776.MirrorCS", {"start": v(-134.48, 21.23) * mm, "end": v(-156.33, 34.08) * mm});
            skLineSegment(sketch, "E777.MirrorCS", {"start": v(-80.62, 21.2) * mm, "end": v(-58.77, 34.05) * mm});
            skLineSegment(sketch, "E778.MirrorCS", {"start": v(-112.64, 58.38) * mm, "end": v(-112.63, 34.08) * mm});
            skLineSegment(sketch, "E779.MirrorCS", {"start": v(-58.8, 58.35) * mm, "end": v(-80.64, 71.18) * mm});
            skLineSegment(sketch, "E780.MirrorCS", {"start": v(-102.47, 58.34) * mm, "end": v(-102.47, 34.05) * mm});
            skLineSegment(sketch, "E781.MirrorCS", {"start": v(-156.33, 34.08) * mm, "end": v(-156.33, 58.38) * mm});
            skLineSegment(sketch, "E782.MirrorCS", {"start": v(-134.49, 71.23) * mm, "end": v(-112.64, 58.38) * mm});
            skLineSegment(sketch, "E783.MirrorCS", {"start": v(-58.77, 34.05) * mm, "end": v(-58.8, 58.35) * mm});
            skLineSegment(sketch, "E784.MirrorCS", {"start": v(187.74, 19.94) * mm, "end": v(165.9, 32.79) * mm});
            skLineSegment(sketch, "E785.MirrorCS", {"start": v(112.2, 33.1) * mm, "end": v(134.04, 20.24) * mm});
            skLineSegment(sketch, "E786.MirrorCS", {"start": v(209.44, 57.08) * mm, "end": v(209.6, 32.79) * mm});
            skLineSegment(sketch, "E787.MirrorCS", {"start": v(165.9, 32.79) * mm, "end": v(165.9, 57.08) * mm});
            skLineSegment(sketch, "E788.MirrorCS", {"start": v(134.04, 20.24) * mm, "end": v(155.9, 33.1) * mm});
            skLineSegment(sketch, "E789.MirrorCS", {"start": v(165.9, 57.08) * mm, "end": v(187.67, 69.9) * mm});
            skLineSegment(sketch, "E790.MirrorCS", {"start": v(155.74, 57.39) * mm, "end": v(133.97, 70.2) * mm});
            skLineSegment(sketch, "E791.MirrorCS", {"start": v(155.9, 33.1) * mm, "end": v(155.74, 57.39) * mm});
            skLineSegment(sketch, "E792.MirrorCS", {"start": v(112.2, 57.39) * mm, "end": v(112.2, 33.1) * mm});
            skLineSegment(sketch, "E793.MirrorCS", {"start": v(80.34, 20.55) * mm, "end": v(58.5, 33.4) * mm});
            skLineSegment(sketch, "E794.MirrorCS", {"start": v(58.5, 33.4) * mm, "end": v(58.5, 57.7) * mm});
            skLineSegment(sketch, "E795.MirrorCS", {"start": v(58.5, 57.7) * mm, "end": v(80.27, 70.5) * mm});
            skLineSegment(sketch, "E796.MirrorCS", {"start": v(80.27, 70.5) * mm, "end": v(102.04, 57.7) * mm});
            skLineSegment(sketch, "E797.MirrorCS", {"start": v(133.97, 70.2) * mm, "end": v(112.2, 57.39) * mm});
            skLineSegment(sketch, "E798.MirrorCS", {"start": v(209.6, 32.79) * mm, "end": v(187.74, 19.94) * mm});
            skLineSegment(sketch, "E799.MirrorCS", {"start": v(187.67, 69.9) * mm, "end": v(209.44, 57.08) * mm});
            skLineSegment(sketch, "E800.MirrorCS", {"start": v(102.2, 33.4) * mm, "end": v(80.34, 20.55) * mm});
            skLineSegment(sketch, "E801.MirrorCS", {"start": v(102.04, 57.7) * mm, "end": v(102.2, 33.4) * mm});
            skLineSegment(sketch, "E802.MirrorCS", {"start": v(-188.18, 71.24) * mm, "end": v(-210.03, 58.39) * mm});
            skLineSegment(sketch, "E803.MirrorCS", {"start": v(-188.18, 21.24) * mm, "end": v(-166.33, 34.09) * mm});
            skLineSegment(sketch, "E804.MirrorCS", {"start": v(-166.33, 58.39) * mm, "end": v(-188.18, 71.24) * mm});
            skLineSegment(sketch, "E805.MirrorCS", {"start": v(-166.33, 34.09) * mm, "end": v(-166.33, 58.39) * mm});
            skLineSegment(sketch, "E806.MirrorCS", {"start": v(-210.03, 58.39) * mm, "end": v(-210.03, 34.09) * mm});
            skLineSegment(sketch, "E807.MirrorCS", {"start": v(-210.03, 34.09) * mm, "end": v(-188.18, 21.24) * mm});
            skLineSegment(sketch, "E808", {"start": v(0, -157.89) * mm, "end": v(-21.85, -170.74) * mm});
            skLineSegment(sketch, "E809", {"start": v(-21.85, -170.74) * mm, "end": v(-21.85, -195.04) * mm});
            skLineSegment(sketch, "E810", {"start": v(-21.85, -195.04) * mm, "end": v(0, -207.89) * mm});
            skLineSegment(sketch, "E811", {"start": v(0, -207.89) * mm, "end": v(21.85, -195.04) * mm});
            skLineSegment(sketch, "E812", {"start": v(21.85, -195.04) * mm, "end": v(21.85, -170.74) * mm});
            skLineSegment(sketch, "E813", {"start": v(21.85, -170.74) * mm, "end": v(0, -157.89) * mm});
            skLineSegment(sketch, "E814.MirrorCS", {"start": v(-75.58, -194.74) * mm, "end": v(-75.58, -170.45) * mm});
            skLineSegment(sketch, "E815.MirrorCS", {"start": v(-31.85, -170.45) * mm, "end": v(-31.85, -194.76) * mm});
            skLineSegment(sketch, "E816.MirrorCS", {"start": v(-53.72, -207.6) * mm, "end": v(-75.58, -194.74) * mm});
            skLineSegment(sketch, "E817.MirrorCS", {"start": v(-75.58, -170.45) * mm, "end": v(-53.73, -157.6) * mm});
            skLineSegment(sketch, "E818.MirrorCS", {"start": v(-31.85, -194.76) * mm, "end": v(-53.72, -207.6) * mm});
            skLineSegment(sketch, "E819.MirrorCS", {"start": v(-53.73, -157.6) * mm, "end": v(-31.85, -170.45) * mm});
            skLineSegment(sketch, "E820.MirrorCS", {"start": v(-129.48, -194.68) * mm, "end": v(-107.53, -207.58) * mm});
            skLineSegment(sketch, "E821.MirrorCS", {"start": v(-107.62, -157.53) * mm, "end": v(-129.48, -170.38) * mm});
            skLineSegment(sketch, "E822.MirrorCS", {"start": v(-183.18, -170.36) * mm, "end": v(-161.33, -157.51) * mm});
            skLineSegment(sketch, "E823.MirrorCS", {"start": v(-139.48, -194.66) * mm, "end": v(-161.33, -207.51) * mm});
            skLineSegment(sketch, "E824.MirrorCS", {"start": v(-161.33, -207.51) * mm, "end": v(-183.18, -194.66) * mm});
            skLineSegment(sketch, "E825.MirrorCS", {"start": v(-107.53, -207.58) * mm, "end": v(-85.58, -194.68) * mm});
            skLineSegment(sketch, "E826.MirrorCS", {"start": v(-139.48, -170.36) * mm, "end": v(-139.48, -194.66) * mm});
            skLineSegment(sketch, "E827.MirrorCS", {"start": v(-85.58, -170.38) * mm, "end": v(-107.62, -157.53) * mm});
            skLineSegment(sketch, "E828.MirrorCS", {"start": v(-129.48, -170.38) * mm, "end": v(-129.48, -194.68) * mm});
            skLineSegment(sketch, "E829.MirrorCS", {"start": v(-183.18, -194.66) * mm, "end": v(-183.18, -170.36) * mm});
            skLineSegment(sketch, "E830.MirrorCS", {"start": v(-161.33, -157.51) * mm, "end": v(-139.48, -170.36) * mm});
            skLineSegment(sketch, "E831.MirrorCS", {"start": v(-85.58, -194.68) * mm, "end": v(-85.58, -170.38) * mm});
            skLineSegment(sketch, "E832.MirrorCS", {"start": v(192.93, -196.16) * mm, "end": v(214.78, -209) * mm});
            skLineSegment(sketch, "E833.MirrorCS", {"start": v(161.08, -208.7) * mm, "end": v(139.23, -195.85) * mm});
            skLineSegment(sketch, "E834.MirrorCS", {"start": v(214.78, -159) * mm, "end": v(192.93, -171.86) * mm});
            skLineSegment(sketch, "E835.MirrorCS", {"start": v(85.53, -195.54) * mm, "end": v(107.38, -208.4) * mm});
            skLineSegment(sketch, "E836.MirrorCS", {"start": v(182.93, -171.55) * mm, "end": v(182.93, -195.85) * mm});
            skLineSegment(sketch, "E837.MirrorCS", {"start": v(139.23, -195.85) * mm, "end": v(139.23, -171.55) * mm});
            skLineSegment(sketch, "E838.MirrorCS", {"start": v(107.38, -208.4) * mm, "end": v(129.23, -195.54) * mm});
            skLineSegment(sketch, "E839.MirrorCS", {"start": v(139.23, -171.55) * mm, "end": v(161.08, -158.7) * mm});
            skLineSegment(sketch, "E840.MirrorCS", {"start": v(192.93, -171.86) * mm, "end": v(192.93, -196.16) * mm});
            skLineSegment(sketch, "E841.MirrorCS", {"start": v(129.23, -171.25) * mm, "end": v(107.38, -158.4) * mm});
            skLineSegment(sketch, "E842.MirrorCS", {"start": v(129.23, -195.54) * mm, "end": v(129.23, -171.25) * mm});
            skLineSegment(sketch, "E843.MirrorCS", {"start": v(85.53, -171.25) * mm, "end": v(85.53, -195.54) * mm});
            skLineSegment(sketch, "E844.MirrorCS", {"start": v(53.68, -208.1) * mm, "end": v(31.85, -195.2) * mm});
            skLineSegment(sketch, "E845.MirrorCS", {"start": v(31.85, -195.2) * mm, "end": v(31.85, -170.9) * mm});
            skLineSegment(sketch, "E846.MirrorCS", {"start": v(31.85, -170.9) * mm, "end": v(53.7, -158.05) * mm});
            skLineSegment(sketch, "E847.MirrorCS", {"start": v(53.7, -158.05) * mm, "end": v(75.53, -170.9) * mm});
            skLineSegment(sketch, "E848.MirrorCS", {"start": v(107.38, -158.4) * mm, "end": v(85.53, -171.25) * mm});
            skLineSegment(sketch, "E849.MirrorCS", {"start": v(182.93, -195.85) * mm, "end": v(161.08, -208.7) * mm});
            skLineSegment(sketch, "E850.MirrorCS", {"start": v(161.08, -158.7) * mm, "end": v(182.93, -171.55) * mm});
            skLineSegment(sketch, "E851.MirrorCS", {"start": v(75.53, -195.24) * mm, "end": v(53.68, -208.1) * mm});
            skLineSegment(sketch, "E852.MirrorCS", {"start": v(75.53, -170.9) * mm, "end": v(75.53, -195.24) * mm});
            skLineSegment(sketch, "E853.MirrorCS", {"start": v(-215.03, -207.5) * mm, "end": v(-193.18, -194.66) * mm});
            skLineSegment(sketch, "E854.MirrorCS", {"start": v(-193.18, -170.36) * mm, "end": v(-215.03, -157.5) * mm});
            skLineSegment(sketch, "E855.MirrorCS", {"start": v(-193.18, -194.66) * mm, "end": v(-193.18, -170.36) * mm});
            skLineSegment(sketch, "E856", {"start": v(26.71, -203.78) * mm, "end": v(4.82, -216.66) * mm});
            skLineSegment(sketch, "E857", {"start": v(48.52, -216.66) * mm, "end": v(26.71, -203.78) * mm});
            skLineSegment(sketch, "E858.MirrorCS", {"start": v(-48.88, -216.35) * mm, "end": v(-27.09, -203.56) * mm});
            skLineSegment(sketch, "E859.MirrorCS", {"start": v(-27.09, -203.56) * mm, "end": v(-5.33, -216.35) * mm});
            skLineSegment(sketch, "E860.MirrorCS", {"start": v(-80.64, -203.37) * mm, "end": v(-102.47, -216.21) * mm});
            skLineSegment(sketch, "E861.MirrorCS", {"start": v(-156.33, -216.18) * mm, "end": v(-134.49, -203.33) * mm});
            skLineSegment(sketch, "E862.MirrorCS", {"start": v(-58.8, -216.2) * mm, "end": v(-80.64, -203.37) * mm});
            skLineSegment(sketch, "E863.MirrorCS", {"start": v(-134.49, -203.33) * mm, "end": v(-112.64, -216.18) * mm});
            skLineSegment(sketch, "E864.MirrorCS", {"start": v(165.9, -217.47) * mm, "end": v(187.67, -204.66) * mm});
            skLineSegment(sketch, "E865.MirrorCS", {"start": v(155.74, -217.17) * mm, "end": v(133.97, -204.36) * mm});
            skLineSegment(sketch, "E866.MirrorCS", {"start": v(58.5, -216.86) * mm, "end": v(80.27, -204.05) * mm});
            skLineSegment(sketch, "E867.MirrorCS", {"start": v(80.27, -204.05) * mm, "end": v(102.04, -216.86) * mm});
            skLineSegment(sketch, "E868.MirrorCS", {"start": v(133.97, -204.36) * mm, "end": v(112.2, -217.17) * mm});
            skLineSegment(sketch, "E869.MirrorCS", {"start": v(187.67, -204.66) * mm, "end": v(209.44, -217.47) * mm});
            skLineSegment(sketch, "E870.MirrorCS", {"start": v(-188.18, -203.32) * mm, "end": v(-210.03, -216.17) * mm});
            skLineSegment(sketch, "E871.MirrorCS", {"start": v(-166.33, -216.17) * mm, "end": v(-188.18, -203.32) * mm});
            skPoint(sketch, "E872", {"position": v(0, -158.5) * mm});
            skLineSegment(sketch, "E873", {"start": v(4.82, 216.57) * mm, "end": v(26.5, 203.74) * mm});
            skLineSegment(sketch, "E874", {"start": v(26.5, 203.74) * mm, "end": v(48.52, 216.57) * mm});
            skLineSegment(sketch, "E875.MirrorCS", {"start": v(-27.03, 204.02) * mm, "end": v(-48.88, 216.87) * mm});
            skLineSegment(sketch, "E876.MirrorCS", {"start": v(-5.18, 216.87) * mm, "end": v(-27.03, 204.02) * mm});
            skLineSegment(sketch, "E877.MirrorCS", {"start": v(-102.47, 217.02) * mm, "end": v(-80.62, 204.16) * mm});
            skLineSegment(sketch, "E878.MirrorCS", {"start": v(-112.63, 217.05) * mm, "end": v(-134.48, 204.2) * mm});
            skLineSegment(sketch, "E879.MirrorCS", {"start": v(-134.48, 204.2) * mm, "end": v(-156.33, 217.05) * mm});
            skLineSegment(sketch, "E880.MirrorCS", {"start": v(-80.62, 204.16) * mm, "end": v(-58.77, 217.02) * mm});
            skLineSegment(sketch, "E881.MirrorCS", {"start": v(187.74, 202.9) * mm, "end": v(165.9, 215.76) * mm});
            skLineSegment(sketch, "E882.MirrorCS", {"start": v(112.2, 216.06) * mm, "end": v(134.04, 203.2) * mm});
            skLineSegment(sketch, "E883.MirrorCS", {"start": v(134.04, 203.2) * mm, "end": v(155.9, 216.06) * mm});
            skLineSegment(sketch, "E884.MirrorCS", {"start": v(80.34, 203.51) * mm, "end": v(58.5, 216.37) * mm});
            skLineSegment(sketch, "E885.MirrorCS", {"start": v(209.6, 215.76) * mm, "end": v(187.74, 202.9) * mm});
            skLineSegment(sketch, "E886.MirrorCS", {"start": v(102.2, 216.37) * mm, "end": v(80.34, 203.51) * mm});
            skLineSegment(sketch, "E887.MirrorCS", {"start": v(-188.18, 204.2) * mm, "end": v(-166.33, 217.06) * mm});
            skLineSegment(sketch, "E888.MirrorCS", {"start": v(-210.03, 217.06) * mm, "end": v(-188.18, 204.2) * mm});
            skPoint(sketch, "E889", {"position": v(-27.09, 204.84) * mm});
            skLineSegment(sketch, "E890", {"start": v(0, 235) * mm, "end": v(-225, 235) * mm});
            skLineSegment(sketch, "E891", {"start": v(-225, 235) * mm, "end": v(-225, -235) * mm});
            skLineSegment(sketch, "E892", {"start": v(-225, -235) * mm, "end": v(225, -235) * mm});
            skLineSegment(sketch, "E893", {"start": v(225, 235) * mm, "end": v(0, 235) * mm});
            skLineSegment(sketch, "E894", {"start": v(225, 235) * mm, "end": v(225, -235) * mm});
            skLineSegment(sketch, "E895", {"start": v(-210.03, 225) * mm, "end": v(-166.33, 225) * mm});
            skLineSegment(sketch, "E896", {"start": v(209.44, -225) * mm, "end": v(165.9, -225) * mm});
            skLineSegment(sketch, "E897", {"start": v(-215, -24.6) * mm, "end": v(-215, 25.37) * mm});
            skLineSegment(sketch, "E898", {"start": v(-210.03, 217.06) * mm, "end": v(-210.03, 225) * mm});
            skLineSegment(sketch, "E899", {"start": v(-166.33, 217.06) * mm, "end": v(-166.33, 225) * mm});
            skLineSegment(sketch, "E900", {"start": v(-156.33, 217.05) * mm, "end": v(-156.33, 225) * mm});
            skLineSegment(sketch, "E901", {"start": v(-112.63, 217.05) * mm, "end": v(-112.63, 225) * mm});
            skLineSegment(sketch, "E902", {"start": v(-102.47, 217.02) * mm, "end": v(-102.47, 225) * mm});
            skLineSegment(sketch, "E903", {"start": v(-58.77, 217.02) * mm, "end": v(-58.77, 225) * mm});
            skLineSegment(sketch, "E904", {"start": v(-48.88, 216.87) * mm, "end": v(-48.88, 225) * mm});
            skLineSegment(sketch, "E905", {"start": v(-5.18, 216.87) * mm, "end": v(-5.18, 225) * mm});
            skLineSegment(sketch, "E906", {"start": v(4.82, 216.57) * mm, "end": v(4.82, 225) * mm});
            skLineSegment(sketch, "E907", {"start": v(48.52, 216.57) * mm, "end": v(48.52, 225) * mm});
            skLineSegment(sketch, "E908", {"start": v(58.5, 216.37) * mm, "end": v(58.5, 225) * mm});
            skLineSegment(sketch, "E909", {"start": v(102.2, 216.37) * mm, "end": v(102.2, 225) * mm});
            skLineSegment(sketch, "E910", {"start": v(112.2, 216.06) * mm, "end": v(112.2, 225) * mm});
            skLineSegment(sketch, "E911", {"start": v(155.9, 216.06) * mm, "end": v(155.9, 225) * mm});
            skLineSegment(sketch, "E912", {"start": v(165.9, 215.76) * mm, "end": v(165.9, 225) * mm});
            skLineSegment(sketch, "E913", {"start": v(209.6, 215.76) * mm, "end": v(209.6, 225) * mm});
            skLineSegment(sketch, "E914", {"start": v(-210.03, -216.17) * mm, "end": v(-210.03, -225) * mm});
            skLineSegment(sketch, "E915", {"start": v(-166.33, -216.17) * mm, "end": v(-166.33, -225) * mm});
            skLineSegment(sketch, "E916", {"start": v(-156.33, -216.18) * mm, "end": v(-156.33, -225) * mm});
            skLineSegment(sketch, "E917", {"start": v(-112.64, -216.18) * mm, "end": v(-112.64, -225) * mm});
            skLineSegment(sketch, "E918", {"start": v(-102.47, -216.21) * mm, "end": v(-102.47, -225) * mm});
            skLineSegment(sketch, "E919", {"start": v(-58.8, -216.2) * mm, "end": v(-58.8, -225) * mm});
            skLineSegment(sketch, "E920", {"start": v(-48.88, -216.35) * mm, "end": v(-48.88, -225) * mm});
            skLineSegment(sketch, "E921", {"start": v(-5.33, -216.35) * mm, "end": v(-5.33, -225) * mm});
            skLineSegment(sketch, "E922", {"start": v(4.82, -216.66) * mm, "end": v(4.82, -225) * mm});
            skLineSegment(sketch, "E923", {"start": v(48.52, -216.66) * mm, "end": v(48.52, -225) * mm});
            skLineSegment(sketch, "E924", {"start": v(58.5, -216.86) * mm, "end": v(58.5, -225) * mm});
            skLineSegment(sketch, "E925", {"start": v(102.04, -216.86) * mm, "end": v(102.04, -225) * mm});
            skLineSegment(sketch, "E926", {"start": v(112.2, -217.17) * mm, "end": v(112.2, -225) * mm});
            skLineSegment(sketch, "E927", {"start": v(155.74, -217.17) * mm, "end": v(155.74, -225) * mm});
            skLineSegment(sketch, "E928", {"start": v(165.9, -217.47) * mm, "end": v(165.9, -225) * mm});
            skLineSegment(sketch, "E929", {"start": v(209.44, -217.47) * mm, "end": v(209.44, -225) * mm});
            skPoint(sketch, "E930.orphan", {"position": v(-215, -225) * mm});
            skLineSegment(sketch, "E931.trimOffspring", {"start": v(-166.33, -225) * mm, "end": v(-210.03, -225) * mm});
            skLineSegment(sketch, "E932.trimOffspring", {"start": v(-112.64, -225) * mm, "end": v(-156.33, -225) * mm});
            skLineSegment(sketch, "E933.trimOffspring", {"start": v(-58.8, -225) * mm, "end": v(-102.47, -225) * mm});
            skLineSegment(sketch, "E934.trimOffspring", {"start": v(-5.33, -225) * mm, "end": v(-48.88, -225) * mm});
            skLineSegment(sketch, "E935.trimOffspring", {"start": v(48.52, -225) * mm, "end": v(4.82, -225) * mm});
            skLineSegment(sketch, "E936.trimOffspring", {"start": v(102.04, -225) * mm, "end": v(58.5, -225) * mm});
            skLineSegment(sketch, "E937.trimOffspring", {"start": v(155.74, -225) * mm, "end": v(112.2, -225) * mm});
            skLineSegment(sketch, "E938", {"start": v(214.78, -159) * mm, "end": v(214.78, -209) * mm});
            skLineSegment(sketch, "E939", {"start": v(214.78, -68.09) * mm, "end": v(214.78, -118.09) * mm});
            skLineSegment(sketch, "E940", {"start": v(-215.03, -157.5) * mm, "end": v(-215.03, -207.5) * mm});
            skLineSegment(sketch, "E941", {"start": v(-215.36, -66.56) * mm, "end": v(-215.03, -116.59) * mm});
            skLineSegment(sketch, "E942", {"start": v(214.78, 23.88) * mm, "end": v(214.78, -26.12) * mm});
            skLineSegment(sketch, "E943", {"start": v(214.59, 115.5) * mm, "end": v(214.78, 65.55) * mm});
            skLineSegment(sketch, "E944", {"start": v(214.78, 207.52) * mm, "end": v(214.78, 157.52) * mm});
            skLineSegment(sketch, "E945.trimOffspring", {"start": v(165.9, 225) * mm, "end": v(209.6, 225) * mm});
            skLineSegment(sketch, "E946.trimOffspring", {"start": v(112.2, 225) * mm, "end": v(155.9, 225) * mm});
            skLineSegment(sketch, "E947.trimOffspring", {"start": v(58.5, 225) * mm, "end": v(102.2, 225) * mm});
            skLineSegment(sketch, "E948.trimOffspring", {"start": v(4.82, 225) * mm, "end": v(48.52, 225) * mm});
            skLineSegment(sketch, "E949.trimOffspring", {"start": v(-48.88, 225) * mm, "end": v(-5.18, 225) * mm});
            skLineSegment(sketch, "E950.trimOffspring", {"start": v(-102.47, 225) * mm, "end": v(-58.77, 225) * mm});
            skLineSegment(sketch, "E951.trimOffspring", {"start": v(-156.33, 225) * mm, "end": v(-112.63, 225) * mm});
            skPoint(sketch, "E952.orphan", {"position": v(-215, 225) * mm});
            skLineSegment(sketch, "E953.trimOffspring", {"start": v(-215, 159.03) * mm, "end": v(-215, 209) * mm});
            skLineSegment(sketch, "E954.trimOffspring", {"start": v(-215, 67.06) * mm, "end": v(-215, 117.03) * mm});
            skLineSegment(sketch, "E955", {"start": v(-215, 25.37) * mm, "end": v(-215, -24.6) * mm});
            skLineSegment(sketch, "E956", {"start": v(-215.03, -66.59) * mm, "end": v(-215.03, -116.59) * mm});
            skSolve(sketch);
        }
        {
            var Q0;
            Q0 = qSketchRegion(id + "F6", true);
            extrude(context, id + "F7", {"entities" : qUnion([Q0]), "depth" : 25 * mm, "offsetDistance" : 25 * mm});
        }
        {
            var Q0;
            Q0=makeQuery(id+"F6.imprint","IMPRINT",FACE,{"disambiguationData":[TD([[makeQuery(id+"F6.imprint","IMPRINT",EDGE,{"derivedFrom":sQuery(id+"F6.wireOp",EDGE,"E424")}),-1.0]])]});
            extrude(context, id + "F8", {"entities" : qUnion([Q0]), "operationType" : NewBodyOperationType.ADD, "depth" : 10 * mm, "offsetDistance" : 25 * mm});
        }
        {
            var Q0;
            Q0=makeQuery(id+"F3.imprint","IMPRINT",FACE,{"disambiguationData":[TD([[makeQuery(id+"F3.imprint","IMPRINT",EDGE,{"derivedFrom":sQuery(id+"F3.wireOp",EDGE,"E8.bottom")}),1.0]])]});
            extrude(context, id + "F9", {"entities" : qUnion([Q0]), "depth" : 10 * mm, "offsetDistance" : 25 * mm});
        }
    });
